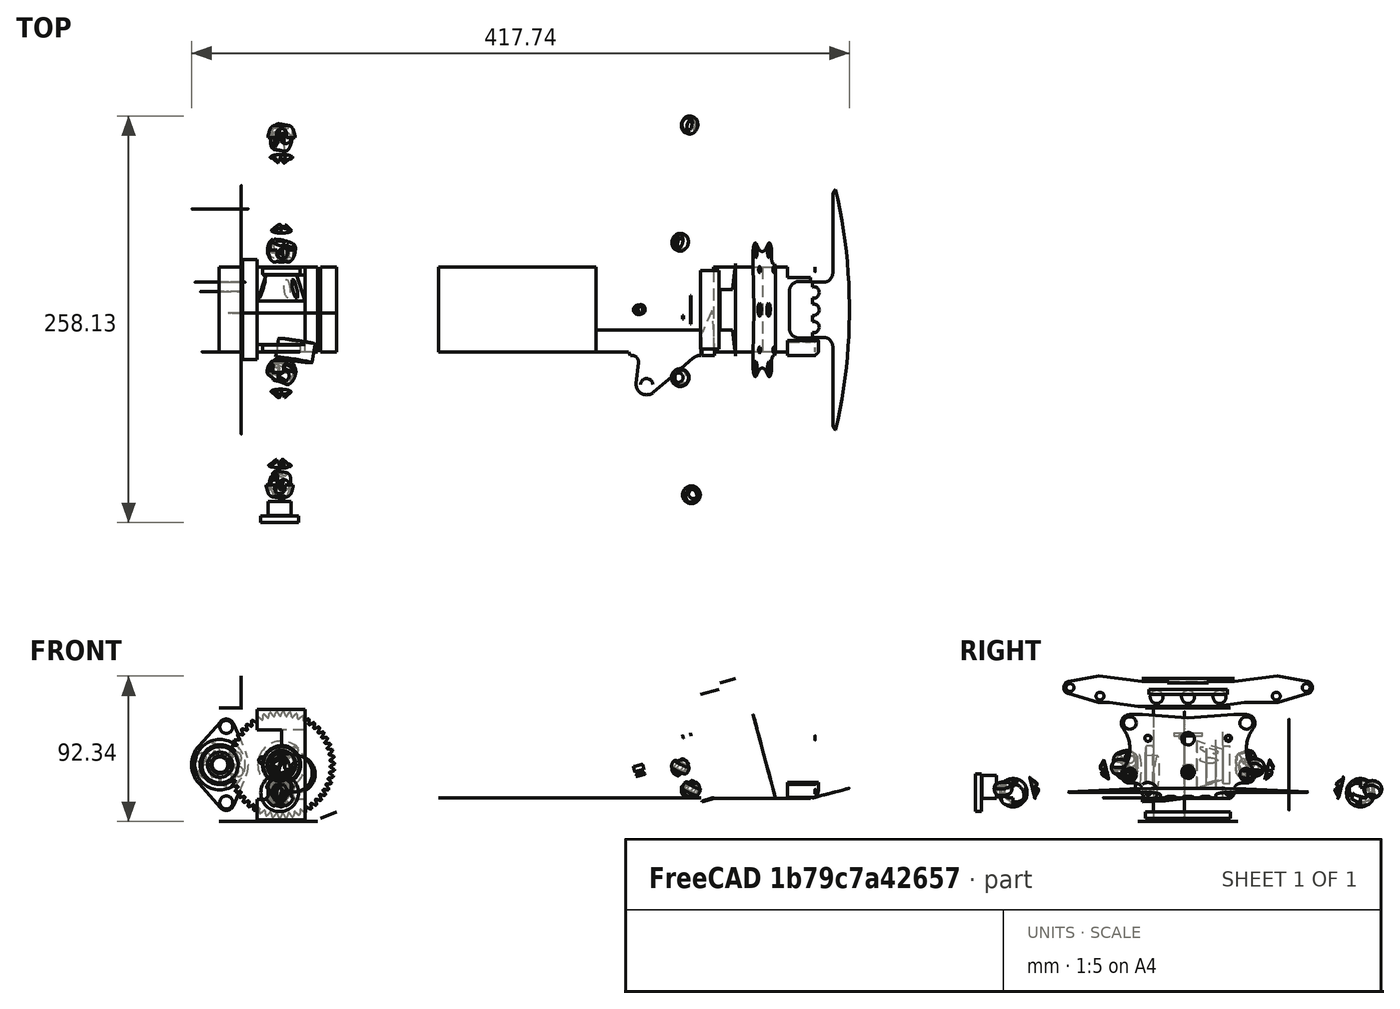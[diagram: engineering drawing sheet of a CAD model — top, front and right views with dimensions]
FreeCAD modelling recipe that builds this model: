
FCSTD DOCUMENT  (FreeCAD 2023.131R26244 +5365 (Git))
Label: Tarmo5
License: All rights reserved
LicenseURL: http://en.wikipedia.org/wiki/All_rights_reserved
objects: App::FeaturePython×327, Part::FeaturePython×279, App::Link×79, App::LinkElement×17, App::DocumentObjectGroupPython×15
note: 277 computed .brp shape members not serialized (recipe doc carries the construction recipe); baked Part::Feature solids carry a one-line shape summary decoded from their .brp
EXTERNAL_REF file=Tarmo5_parts/B03.fcstd obj=Solid
EXTERNAL_REF file=Tarmo5_parts/Part 1.fcstd obj=Solid
EXTERNAL_REF file=Tarmo5_parts/B08-T.fcstd obj=Solid
EXTERNAL_REF file=Tarmo5_parts/DRIVE ASSEMBLY _1_.fcstd obj=Link001
EXTERNAL_REF file=Tarmo5_parts/NOSE ASSEMBLY _1_.fcstd obj=Link
EXTERNAL_REF file=Tarmo5_parts/NOSE ASSEMBLY _1_.fcstd obj=Link002
EXTERNAL_REF file=Tarmo5_parts/NOSE ASSEMBLY _1_.fcstd obj=Link005
EXTERNAL_REF file=Tarmo5_parts/DRIVE ASSEMBLY _1_.fcstd obj=Link002
EXTERNAL_REF file=Tarmo5_parts/NOSE ASSEMBLY _1_.fcstd obj=Link015
EXTERNAL_REF file=Tarmo5_parts/DRIVE ASSEMBLY _1_.fcstd obj=Link009
EXTERNAL_REF file=Tarmo5_parts/DRIVE ASSEMBLY _1_.fcstd obj=Link024
EXTERNAL_REF file=Tarmo5_parts/DRIVE ASSEMBLY _1_.fcstd obj=Link027
EXTERNAL_REF file=Tarmo5_parts/NOSE ASSEMBLY _1__parts/Front Sus _1_.fcstd obj=Link001
EXTERNAL_REF file=Tarmo5_parts/NOSE ASSEMBLY _1__parts/Front Sus _1_.fcstd obj=Link005
EXTERNAL_REF file=Tarmo5_parts/DRIVE ASSEMBLY _1_.fcstd obj=Link
EXTERNAL_REF file=Tarmo5_parts/NOSE ASSEMBLY _1_.fcstd obj=Link008
EXTERNAL_REF file=Tarmo5_parts/DRIVE ASSEMBLY _1_.fcstd obj=Link004
EXTERNAL_REF file=Tarmo5_parts/DRIVE ASSEMBLY _1_.fcstd obj=Link012
EXTERNAL_REF file=Tarmo5_parts/DRIVE ASSEMBLY _1_.fcstd obj=Link029
EXTERNAL_REF file=Tarmo5_parts/DRIVE ASSEMBLY _1_.fcstd obj=Link011
EXTERNAL_REF file=Tarmo5_parts/DRIVE ASSEMBLY _1_.fcstd obj=Link019
EXTERNAL_REF file=Tarmo5_parts/DRIVE ASSEMBLY _1_.fcstd obj=Link005
EXTERNAL_REF file=Tarmo5_parts/DRIVE ASSEMBLY _1_.fcstd obj=Link007
EXTERNAL_REF file=Tarmo5_parts/DRIVE ASSEMBLY _1_.fcstd obj=Link018
EXTERNAL_REF file=Tarmo5_parts/DRIVE ASSEMBLY _1_.fcstd obj=Link016
EXTERNAL_REF file=Tarmo5_parts/DRIVE ASSEMBLY _1_.fcstd obj=Link014
EXTERNAL_REF file=Tarmo5_parts/NOSE ASSEMBLY _1__parts/Front Sus _1_.fcstd obj=Link012
EXTERNAL_REF file=Tarmo5_parts/NOSE ASSEMBLY _1__parts/Front Sus _1_.fcstd obj=Link013
EXTERNAL_REF file=Tarmo5_parts/NOSE ASSEMBLY _1__parts/Front Sus _1_.fcstd obj=Link019
EXTERNAL_REF file=Tarmo5_parts/NOSE ASSEMBLY _1__parts/Front Sus _1_.fcstd obj=Link010
EXTERNAL_REF file=Tarmo5_parts/NOSE ASSEMBLY _1__parts/Front Sus _1_.fcstd obj=Link004
EXTERNAL_REF file=Tarmo5_parts/NOSE ASSEMBLY _1__parts/Front Sus _1_.fcstd obj=Link003
EXTERNAL_REF file=Tarmo5_parts/DRIVE ASSEMBLY _1_.fcstd obj=Link015
EXTERNAL_REF file=Tarmo5_parts/NOSE ASSEMBLY _1__parts/Front Sus _1_.fcstd obj=Link015
EXTERNAL_REF file=Tarmo5_parts/NOSE ASSEMBLY _1__parts/Front Sus _1_.fcstd obj=Link008
EXTERNAL_REF file=Tarmo5_parts/NOSE ASSEMBLY _1_.fcstd obj=Link006
EXTERNAL_REF file=Tarmo5_parts/NOSE ASSEMBLY _1_.fcstd obj=Link011
EXTERNAL_REF file=Tarmo5_parts/NOSE ASSEMBLY _1__parts/Link Assembly _1_.fcstd obj=Link
EXTERNAL_REF file=Tarmo5_parts/NOSE ASSEMBLY _1__parts/Link Assembly _1_.fcstd obj=Link001
EXTERNAL_REF file=Tarmo5_parts/NOSE ASSEMBLY _1__parts/Link Assembly _1_.fcstd obj=Link002
EXTERNAL_REF file=Tarmo5_parts/NOSE ASSEMBLY _1__parts/Link Assembly _2_.fcstd obj=Link
EXTERNAL_REF file=Tarmo5_parts/NOSE ASSEMBLY _1__parts/Link Assembly _2_.fcstd obj=Link001
EXTERNAL_REF file=Tarmo5_parts/NOSE ASSEMBLY _1__parts/Link Assembly _2_.fcstd obj=Link002
EXTERNAL_REF file=Tarmo5_parts/NOSE ASSEMBLY _1_.fcstd obj=Link010
EXTERNAL_REF file=Tarmo5_parts/NOSE ASSEMBLY _1_.fcstd obj=Link003
EXTERNAL_REF file=Tarmo5_parts/NOSE ASSEMBLY _1_.fcstd obj=Link013
EXTERNAL_REF file=Tarmo5_parts/NOSE ASSEMBLY _1__parts/Front Sus _1_.fcstd obj=Link017
EXTERNAL_REF file=Tarmo5_parts/NOSE ASSEMBLY _1__parts/Front Sus _1_.fcstd obj=Link014
EXTERNAL_REF file=Tarmo5_parts/NOSE ASSEMBLY _1__parts/Front Sus _1_.fcstd obj=Link002
EXTERNAL_REF file=Tarmo5_parts/NOSE ASSEMBLY _1__parts/Front Sus _1_.fcstd obj=Link
EXTERNAL_REF file=Tarmo5_parts/NOSE ASSEMBLY _1__parts/Front Sus _1_.fcstd obj=Link018
EXTERNAL_REF file=Tarmo5_parts/NOSE ASSEMBLY _1__parts/Front Sus _1_.fcstd obj=Link011
EXTERNAL_REF file=Tarmo5_parts/NOSE ASSEMBLY _1__parts/Front Sus _1_.fcstd obj=Link007
EXTERNAL_REF file=Tarmo5_parts/NOSE ASSEMBLY _1__parts/Front Sus _1_.fcstd obj=Link006
EXTERNAL_REF file=Tarmo5_parts/DRIVE ASSEMBLY _1_.fcstd obj=Link017
EXTERNAL_REF file=Tarmo5_parts/DRIVE ASSEMBLY _1_.fcstd obj=Link010
EXTERNAL_REF file=Tarmo5_parts/DRIVE ASSEMBLY _1_.fcstd obj=Link006
EXTERNAL_REF file=Tarmo5_parts/DRIVE ASSEMBLY _1_.fcstd obj=Link003
EXTERNAL_REF file=Tarmo5_parts/DRIVE ASSEMBLY _1_.fcstd obj=Link022
EXTERNAL_REF file=Tarmo5_parts/DRIVE ASSEMBLY _1_.fcstd obj=Link032
EXTERNAL_REF file=Tarmo5_parts/DRIVE ASSEMBLY _1_.fcstd obj=Link008
EXTERNAL_REF file=Tarmo5_parts/DRIVE ASSEMBLY _1__parts/DOGBONE _1_.fcstd obj=Link
EXTERNAL_REF file=Tarmo5_parts/DRIVE ASSEMBLY _1__parts/DOGBONE _1_.fcstd obj=Link001
EXTERNAL_REF file=Tarmo5_parts/DRIVE ASSEMBLY _1__parts/DOGBONE _1_.fcstd obj=Link002
EXTERNAL_REF file=Tarmo5_parts/DRIVE ASSEMBLY _1__parts/DOGBONE _1_.fcstd obj=Link003
EXTERNAL_REF file=Tarmo5_parts/DRIVE ASSEMBLY _1__parts/DOGBONE _1_.fcstd obj=Link004
EXTERNAL_REF file=Tarmo5_parts/DRIVE ASSEMBLY _1__parts/DOGBONE _1_.fcstd obj=Link005
EXTERNAL_REF file=Tarmo5_parts/DRIVE ASSEMBLY _1__parts/DOGBONE _1_.fcstd obj=Link006
EXTERNAL_REF file=Tarmo5_parts/DRIVE ASSEMBLY _1_.fcstd obj=Link023
EXTERNAL_REF file=Tarmo5_parts/DRIVE ASSEMBLY _1_.fcstd obj=Link020
EXTERNAL_REF file=Tarmo5_parts/Fasteners/M4x16Screws.FCStd obj=Link
EXTERNAL_REF file=Tarmo5_parts/NOSE ASSEMBLY _1__parts/Front Sus _1_.fcstd obj=Link009
EXTERNAL_REF file=Tarmo5_parts/Fasteners/M4x35Screws.FCStd obj=Screw
EXTERNAL_REF file=Tarmo5_parts/Fasteners/M4xScrews.FCStd obj=Screw
EXTERNAL_REF file=Tarmo5_parts/Fasteners/M4x45Screws.FCStd obj=Screw
EXTERNAL_REF file=Tarmo5_parts/Fasteners/M4x16Screws.FCStd obj=Screw
EXTERNAL_REF file=Tarmo5_parts/Fasteners/M3_Nut.FCStd obj=Nut

FEATURE [App::Link] Link  label="B03"
  AutoLinkLabel = true
  AutoPlacement = true
  LinkPlacement = pos=(-50.1198,8.13855,-13.564) rot=(0,0,1;1.5708rad)
  LinkedObject = -> <external Tarmo5_parts/B03.fcstd>#Solid
  Placement = pos=(-50.1198,8.13855,-13.564) rot=(0,0,1;1.5708rad)
  SyncGroupVisibility = false
  TreeRank = 1
  _LinkVersion = 1
FEATURE [App::Link] Link001  label="Part 1"
  AutoLinkLabel = true
  AutoPlacement = true
  LinkPlacement = pos=(103.215,30.1385,-27.0233) rot=(0,0,-1;1.5708rad)
  LinkedObject = -> <external Tarmo5_parts/Part 1.fcstd>#Solid
  Placement = pos=(103.215,30.1385,-27.0233) rot=(0,0,-1;1.5708rad)
  SyncGroupVisibility = false
  TreeRank = 641
  _LinkVersion = 1
FEATURE [App::Link] Link002  label="B08-T"
  AutoLinkLabel = true
  AutoPlacement = true
  LinkPlacement = pos=(-32.1198,-28.8615,-5.56404) rot=(-0.57735,-0.57735,-0.57735;2.0944rad)
  LinkedObject = -> <external Tarmo5_parts/B08-T.fcstd>#Solid
  Placement = pos=(-32.1198,-28.8615,-5.56404) rot=(-0.57735,-0.57735,-0.57735;2.0944rad)
  SyncGroupVisibility = false
  TreeRank = 5
  _LinkVersion = 1
FEATURE [App::Link] Link005  label="B02"
  AutoLinkLabel = false
  AutoPlacement = true
  LinkPlacement = pos=(-105.52,8.13855,-13.564) rot=(0,0,1;1.5708rad)
  LinkedObject = -> <external Tarmo5_parts/DRIVE ASSEMBLY _1_.fcstd>#Link001
  Placement = pos=(-105.52,8.13855,-13.564) rot=(0,0,1;1.5708rad)
  SyncGroupVisibility = false
  TreeRank = 17
  _LinkOwner = 2515
  _LinkVersion = 1
FEATURE [App::Link] Link006  label="B04"
  AutoLinkLabel = false
  AutoPlacement = true
  LinkPlacement = pos=(127.88,8.13855,-9.06404) rot=(0,0,1;1.5708rad)
  LinkedObject = -> <external Tarmo5_parts/NOSE ASSEMBLY _1_.fcstd>#Link
  Placement = pos=(127.88,8.13855,-9.06404) rot=(0,0,1;1.5708rad)
  SyncGroupVisibility = false
  TreeRank = 18
  _LinkOwner = 2515
  _LinkVersion = 1
FEATURE [App::Link] Link007  label="B05"
  AutoLinkLabel = false
  AutoPlacement = true
  LinkPlacement = pos=(129.622,8.13853,-9.37807) rot=(0,0,1;1.5708rad)
  LinkedObject = -> <external Tarmo5_parts/NOSE ASSEMBLY _1_.fcstd>#Link002
  Placement = pos=(129.622,8.13853,-9.37807) rot=(0,0,1;1.5708rad)
  SyncGroupVisibility = false
  TreeRank = 19
  _LinkOwner = 2515
  _LinkVersion = 1
FEATURE [App::Link] Link008  label="B06"
  AutoLinkLabel = false
  AutoPlacement = true
  LinkPlacement = pos=(125.481,8.13853,-9.37807) rot=(0,0,1;1.5708rad)
  LinkedObject = -> <external Tarmo5_parts/NOSE ASSEMBLY _1_.fcstd>#Link005
  Placement = pos=(125.481,8.13853,-9.37807) rot=(0,0,1;1.5708rad)
  SyncGroupVisibility = false
  TreeRank = 20
  _LinkOwner = 2515
  _LinkVersion = 1
FEATURE [App::Link] Link009  label="A01"
  AutoLinkLabel = false
  AutoPlacement = true
  LinkPlacement = pos=(-110.52,40.1385,31.436) rot=(0,0,1;0rad)
  LinkedObject = -> <external Tarmo5_parts/DRIVE ASSEMBLY _1_.fcstd>#Link002
  Placement = pos=(-110.52,40.1385,31.436) rot=(0,0,1;0rad)
  SyncGroupVisibility = false
  TreeRank = 21
  _LinkOwner = 2515
  _LinkVersion = 1
FEATURE [App::Link] Link010  label="A002"
  AutoLinkLabel = false
  AutoPlacement = true
  LinkPlacement = pos=(195.547,-23.8615,32.0753) rot=(-0.130526,0,0.991445;3.14159rad)
  LinkedObject = -> <external Tarmo5_parts/NOSE ASSEMBLY _1_.fcstd>#Link015
  Placement = pos=(195.547,-23.8615,32.0753) rot=(-0.130526,0,0.991445;3.14159rad)
  SyncGroupVisibility = false
  TreeRank = 22
  _LinkOwner = 2515
  _LinkVersion = 1
FEATURE [App::Link] Link011  label="B13-T"
  AutoLinkLabel = false
  AutoPlacement = true
  LinkPlacement = pos=(-105.52,8.13855,-13.564) rot=(0,0,-1;1.5708rad)
  LinkedObject = -> <external Tarmo5_parts/DRIVE ASSEMBLY _1_.fcstd>#Link009
  Placement = pos=(-105.52,8.13855,-13.564) rot=(0,0,-1;1.5708rad)
  SyncGroupVisibility = false
  TreeRank = 23
  _LinkOwner = 2515
  _LinkVersion = 1
FEATURE [App::Link] Link012  label="B12-T"
  AutoLinkLabel = false
  AutoPlacement = true
  LinkPlacement = pos=(-65.1198,8.13855,-13.564) rot=(0,0,-1;1.5708rad)
  LinkedObject = -> <external Tarmo5_parts/DRIVE ASSEMBLY _1_.fcstd>#Link024
  Placement = pos=(-65.1198,8.13855,-13.564) rot=(0,0,-1;1.5708rad)
  SyncGroupVisibility = false
  TreeRank = 24
  _LinkOwner = 2515
  _LinkVersion = 1
FEATURE [App::Link] Link013  label="B01"
  AutoLinkLabel = false
  AutoPlacement = true
  LinkPlacement = pos=(-105.52,8.13855,-13.564) rot=(0,0,1;3.14159rad)
  LinkedObject = -> <external Tarmo5_parts/DRIVE ASSEMBLY _1_.fcstd>#Link027
  Placement = pos=(-105.52,8.13855,-13.564) rot=(0,0,1;3.14159rad)
  SyncGroupVisibility = false
  TreeRank = 25
  _LinkOwner = 2515
  _LinkVersion = 1
FEATURE [App::Link] Link014  label="B11-T"
  AutoLinkLabel = false
  AutoPlacement = true
  LinkPlacement = pos=(181.617,8.13853,-38.0407) rot=(0,1,0;6.02139rad)
  LinkedObject = -> <external Tarmo5_parts/NOSE ASSEMBLY _1__parts/Front Sus _1_.fcstd>#Link001
  Placement = pos=(181.617,8.13853,-38.0407) rot=(0,1,0;6.02139rad)
  SyncGroupVisibility = false
  TreeRank = 26
  _LinkOwner = 2515
  _LinkVersion = 1
FEATURE [App::Link] Link015  label="B10-T"
  AutoLinkLabel = false
  AutoPlacement = true
  LinkPlacement = pos=(220.627,8.13853,-38.3547) rot=(0,1,0;6.02139rad)
  LinkedObject = -> <external Tarmo5_parts/NOSE ASSEMBLY _1__parts/Front Sus _1_.fcstd>#Link005
  Placement = pos=(220.627,8.13853,-38.3547) rot=(0,1,0;6.02139rad)
  SyncGroupVisibility = false
  TreeRank = 27
  _LinkOwner = 2515
  _LinkVersion = 1
FEATURE [App::Link] Link016  label="B09"
  AutoLinkLabel = false
  AutoPlacement = true
  LinkPlacement = pos=(-129.02,72.1385,-13.564) rot=(0,0.707107,0.707107;3.14159rad)
  LinkedObject = -> <external Tarmo5_parts/DRIVE ASSEMBLY _1_.fcstd>#Link
  Placement = pos=(-129.02,72.1385,-13.564) rot=(0,0.707107,0.707107;3.14159rad)
  SyncGroupVisibility = false
  TreeRank = 28
  _LinkOwner = 2515
  _LinkVersion = 1
FEATURE [App::Link] Link017  label="B07-T"
  AutoLinkLabel = false
  AutoPlacement = true
  LinkPlacement = pos=(244.221,8.13853,-35.5564) rot=(-0.129428,0.129428,0.983106;4.69535rad)
  LinkedObject = -> <external Tarmo5_parts/NOSE ASSEMBLY _1_.fcstd>#Link008
  Placement = pos=(244.221,8.13853,-35.5564) rot=(-0.129428,0.129428,0.983106;4.69535rad)
  SyncGroupVisibility = false
  TreeRank = 29
  _LinkOwner = 2515
  _LinkVersion = 1
FEATURE [App::Link] Link019  label="Part 003"
  AutoLinkLabel = false
  AutoPlacement = true
  LinkPlacement = pos=(-101.02,33.6385,3.43596) rot=(-0.57735,-0.57735,-0.57735;4.18879rad)
  LinkedObject = -> <external Tarmo5_parts/DRIVE ASSEMBLY _1_.fcstd>#Link012
  Placement = pos=(-101.02,33.6385,3.43596) rot=(-0.57735,-0.57735,-0.57735;4.18879rad)
  SyncGroupVisibility = false
  TreeRank = 31
  _LinkOwner = 2515
  _LinkVersion = 1
FEATURE [App::Link] Link020  label="Part 004"
  AutoLinkLabel = false
  AutoPlacement = true
  LinkPlacement = pos=(-129.02,-13.6115,-13.564) rot=(0,1,0;3.14159rad)
  LinkedObject = -> <external Tarmo5_parts/DRIVE ASSEMBLY _1_.fcstd>#Link029
  Placement = pos=(-129.02,-13.6115,-13.564) rot=(0,1,0;3.14159rad)
  SyncGroupVisibility = false
  TreeRank = 32
  _LinkOwner = 2515
  _LinkVersion = 1
FEATURE [App::Link] Link021  label="Part 005"
  AutoLinkLabel = false
  AutoPlacement = true
  LinkPlacement = pos=(-90.0198,-18.8615,-13.564) rot=(0,0,1;3.14159rad)
  LinkedObject = -> <external Tarmo5_parts/DRIVE ASSEMBLY _1_.fcstd>#Link011
  Placement = pos=(-90.0198,-18.8615,-13.564) rot=(0,0,1;3.14159rad)
  SyncGroupVisibility = false
  TreeRank = 33
  _LinkOwner = 2515
  _LinkVersion = 1
FEATURE [App::Link] Link022  label="Part 006"
  AutoLinkLabel = false
  AutoPlacement = true
  LinkPlacement = pos=(-90.0198,35.1385,-13.564) rot=(0,0,1;0rad)
  LinkedObject = -> <external Tarmo5_parts/DRIVE ASSEMBLY _1_.fcstd>#Link019
  Placement = pos=(-90.0198,35.1385,-13.564) rot=(0,0,1;0rad)
  SyncGroupVisibility = false
  TreeRank = 34
  _LinkOwner = 2515
  _LinkVersion = 1
FEATURE [App::Link] Link026  label="A02"
  AutoLinkLabel = false
  AutoPlacement = true
  LinkPlacement = pos=(-105.52,-67.8076,-39.4513) rot=(-0.116949,0.116949,-0.986228;4.69852rad)
  LinkedObject = -> <external Tarmo5_parts/DRIVE ASSEMBLY _1_.fcstd>#Link005
  Placement = pos=(-105.52,-67.8076,-39.4513) rot=(-0.116949,0.116949,-0.986228;4.69852rad)
  SyncGroupVisibility = false
  TreeRank = 102
  _LinkOwner = 2604
  _LinkVersion = 1
FEATURE [App::Link] Link027  label="A003"
  AutoLinkLabel = false
  AutoPlacement = true
  LinkPlacement = pos=(-75.5198,84.0847,-5.45132) rot=(-0.116949,-0.116949,-0.986228;1.58466rad)
  LinkedObject = -> <external Tarmo5_parts/DRIVE ASSEMBLY _1_.fcstd>#Link007
  Placement = pos=(-75.5198,84.0847,-5.45132) rot=(-0.116949,-0.116949,-0.986228;1.58466rad)
  SyncGroupVisibility = false
  TreeRank = 113
  _LinkOwner = 2604
  _LinkVersion = 1
FEATURE [App::Link] Link028  label="A004"
  AutoLinkLabel = false
  AutoPlacement = true
  LinkPlacement = pos=(-105.52,84.0847,-39.4513) rot=(0.704634,-0.704634,0.083557;2.97487rad)
  LinkedObject = -> <external Tarmo5_parts/DRIVE ASSEMBLY _1_.fcstd>#Link018
  Placement = pos=(-105.52,84.0847,-39.4513) rot=(0.704634,-0.704634,0.083557;2.97487rad)
  SyncGroupVisibility = false
  TreeRank = 114
  _LinkOwner = 2604
  _LinkVersion = 1
FEATURE [App::Link] Link029  label="A03"
  AutoLinkLabel = false
  AutoPlacement = true
  LinkPlacement = pos=(-89.9198,137.031,-31.3386) rot=(0,0,-1;3.14159rad)
  LinkedObject = -> <external Tarmo5_parts/DRIVE ASSEMBLY _1_.fcstd>#Link016
  Placement = pos=(-89.9198,137.031,-31.3386) rot=(0,0,-1;3.14159rad)
  SyncGroupVisibility = false
  TreeRank = 117
  _LinkVersion = 1
FEATURE [App::Link] Link030  label="A005"
  AutoLinkLabel = false
  AutoPlacement = true
  LinkPlacement = pos=(-75.5198,-67.8076,-5.45132) rot=(-0.704634,-0.704634,-0.083557;2.97487rad)
  LinkedObject = -> <external Tarmo5_parts/DRIVE ASSEMBLY _1_.fcstd>#Link014
  Placement = pos=(-75.5198,-67.8076,-5.45132) rot=(-0.704634,-0.704634,-0.083557;2.97487rad)
  SyncGroupVisibility = false
  TreeRank = 116
  _LinkOwner = 2604
  _LinkVersion = 1
FEATURE [App::Link] Link031  label="A006"
  AutoLinkLabel = false
  AutoPlacement = true
  LinkPlacement = pos=(214.469,82.3563,-29.2816) rot=(-0.028523,0.22455,0.974045;4.65926rad)
  LinkedObject = -> <external Tarmo5_parts/NOSE ASSEMBLY _1__parts/Front Sus _1_.fcstd>#Link012
  Placement = pos=(214.469,82.3563,-29.2816) rot=(-0.028523,0.22455,0.974045;4.65926rad)
  SyncGroupVisibility = false
  TreeRank = 118
  _LinkOwner = 2604
  _LinkVersion = 1
FEATURE [App::Link] Link032  label="A007"
  AutoLinkLabel = false
  AutoPlacement = true
  LinkPlacement = pos=(176.691,82.3563,-4.20474) rot=(0.688224,-0.706955,0.162977;3.18299rad)
  LinkedObject = -> <external Tarmo5_parts/NOSE ASSEMBLY _1__parts/Front Sus _1_.fcstd>#Link013
  Placement = pos=(176.691,82.3563,-4.20474) rot=(0.688224,-0.706955,0.162977;3.18299rad)
  SyncGroupVisibility = false
  TreeRank = 119
  _LinkOwner = 2604
  _LinkVersion = 1
FEATURE [App::Link] Link033  label="A008"
  AutoLinkLabel = false
  AutoPlacement = true
  LinkPlacement = pos=(214.469,-66.0793,-29.2816) rot=(-0.688224,-0.706955,-0.162977;3.18299rad)
  LinkedObject = -> <external Tarmo5_parts/NOSE ASSEMBLY _1__parts/Front Sus _1_.fcstd>#Link019
  Placement = pos=(214.469,-66.0793,-29.2816) rot=(-0.688224,-0.706955,-0.162977;3.18299rad)
  SyncGroupVisibility = false
  TreeRank = 120
  _LinkOwner = 2604
  _LinkVersion = 1
FEATURE [App::Link] Link034  label="A009"
  AutoLinkLabel = false
  AutoPlacement = true
  LinkPlacement = pos=(176.691,-66.0793,-4.20474) rot=(0.028523,0.22455,-0.974045;4.65926rad)
  LinkedObject = -> <external Tarmo5_parts/NOSE ASSEMBLY _1__parts/Front Sus _1_.fcstd>#Link010
  Placement = pos=(176.691,-66.0793,-4.20474) rot=(0.028523,0.22455,-0.974045;4.65926rad)
  SyncGroupVisibility = false
  TreeRank = 121
  _LinkOwner = 2604
  _LinkVersion = 1
FEATURE [App::Link] Link035  label="A04"
  AutoLinkLabel = false
  AutoPlacement = true
  LinkPlacement = pos=(196.986,114.574,-24.3075) rot=(0.129428,-0.129428,-0.983106;1.58783rad)
  LinkedObject = -> <external Tarmo5_parts/NOSE ASSEMBLY _1__parts/Front Sus _1_.fcstd>#Link004
  Placement = pos=(196.986,114.574,-24.3075) rot=(0.129428,-0.129428,-0.983106;1.58783rad)
  SyncGroupVisibility = false
  TreeRank = 171
  _LinkOwner = 2604
  _LinkVersion = 1
FEATURE [App::Link] Link036  label="A010"
  AutoLinkLabel = false
  AutoPlacement = true
  LinkPlacement = pos=(198.145,-98.2971,-23.997) rot=(-0.129428,-0.129428,0.983106;1.58783rad)
  LinkedObject = -> <external Tarmo5_parts/NOSE ASSEMBLY _1__parts/Front Sus _1_.fcstd>#Link003
  Placement = pos=(198.145,-98.2971,-23.997) rot=(-0.129428,-0.129428,0.983106;1.58783rad)
  SyncGroupVisibility = false
  TreeRank = 172
  _LinkOwner = 2604
  _LinkVersion = 1
FEATURE [App::Link] Link037  label="A011"
  AutoLinkLabel = false
  AutoPlacement = true
  LinkPlacement = pos=(-91.1198,-120.754,-31.3386) rot=(0,0,1;0rad)
  LinkedObject = -> <external Tarmo5_parts/DRIVE ASSEMBLY _1_.fcstd>#Link015
  Placement = pos=(-91.1198,-120.754,-31.3386) rot=(0,0,1;0rad)
  SyncGroupVisibility = false
  TreeRank = 194
  _LinkOwner = 2604
  _LinkVersion = 1
FEATURE [App::Link] Link038  label="A06"
  AutoLinkLabel = false
  AutoPlacement = true
  LinkPlacement = pos=(197.199,153.573,-24.0435) rot=(-0.130526,-0.000714,0.991445;3.13074rad)
  LinkedObject = -> <external Tarmo5_parts/NOSE ASSEMBLY _1__parts/Front Sus _1_.fcstd>#Link015
  Placement = pos=(197.199,153.573,-24.0435) rot=(-0.130526,-0.000714,0.991445;3.13074rad)
  SyncGroupVisibility = false
  TreeRank = 217
  _LinkOwner = 2604
  _LinkVersion = 1
FEATURE [App::Link] Link039  label="A05"
  AutoLinkLabel = false
  AutoPlacement = true
  LinkPlacement = pos=(198.312,-125.295,-23.7451) rot=(0.130526,-0.001139,-0.991444;3.12429rad)
  LinkedObject = -> <external Tarmo5_parts/NOSE ASSEMBLY _1__parts/Front Sus _1_.fcstd>#Link008
  Placement = pos=(198.312,-125.295,-23.7451) rot=(0.130526,-0.001139,-0.991444;3.12429rad)
  SyncGroupVisibility = false
  TreeRank = 218
  _LinkOwner = 2604
  _LinkVersion = 1
FEATURE [App::Link] Link040  label="A08"
  AutoLinkLabel = false
  AutoPlacement = true
  LinkPlacement = pos=(143.307,55.6385,-39.5909) rot=(-0.763566,-0.637858,-0.100525;3.30915rad)
  LinkedObject = -> <external Tarmo5_parts/NOSE ASSEMBLY _1_.fcstd>#Link006
  Placement = pos=(143.307,55.6385,-39.5909) rot=(-0.763566,-0.637858,-0.100525;3.30915rad)
  SyncGroupVisibility = false
  TreeRank = 229
  _LinkOwner = 2604
  _LinkVersion = 1
FEATURE [App::Link] Link041  label="A07"
  AutoLinkLabel = false
  AutoPlacement = true
  LinkPlacement = pos=(136.707,-39.3615,-14.9598) rot=(0.128989,-0.153039,-0.979766;1.42083rad)
  LinkedObject = -> <external Tarmo5_parts/NOSE ASSEMBLY _1_.fcstd>#Link011
  Placement = pos=(136.707,-39.3615,-14.9598) rot=(0.128989,-0.153039,-0.979766;1.42083rad)
  SyncGroupVisibility = false
  TreeRank = 230
  _LinkOwner = 2604
  _LinkVersion = 1
FEATURE [App::Link] Link042  label="A10B"
  AutoLinkLabel = false
  AutoPlacement = true
  LinkPlacement = pos=(165.392,-102.99,-26.1097) rot=(-0.872256,0.482265,-0.081178;2.90119rad)
  LinkedObject = -> <external Tarmo5_parts/NOSE ASSEMBLY _1__parts/Link Assembly _1_.fcstd>#Link
  Placement = pos=(165.392,-102.99,-26.1097) rot=(-0.872256,0.482265,-0.081178;2.90119rad)
  SyncGroupVisibility = false
  TreeRank = 243
  _LinkOwner = 2604
  _LinkVersion = 1
FEATURE [App::Link] Link043  label="A10C"
  AutoLinkLabel = false
  AutoPlacement = true
  LinkPlacement = pos=(239.877,-64.8807,2.27137) rot=(-0.130489,-0.024029,0.991159;2.78053rad)
  LinkedObject = -> <external Tarmo5_parts/NOSE ASSEMBLY _1__parts/Link Assembly _1_.fcstd>#Link001
  Placement = pos=(239.877,-64.8807,2.27137) rot=(-0.130489,-0.024029,0.991159;2.78053rad)
  SyncGroupVisibility = false
  TreeRank = 244
  _LinkOwner = 2604
  _LinkVersion = 1
FEATURE [App::Link] Link044  label="A10A"
  AutoLinkLabel = false
  AutoPlacement = true
  LinkPlacement = pos=(169.83,-116.855,-32.9007) rot=(0.272191,0.12914,0.953538;1.75269rad)
  LinkedObject = -> <external Tarmo5_parts/NOSE ASSEMBLY _1__parts/Link Assembly _1_.fcstd>#Link002
  Placement = pos=(169.83,-116.855,-32.9007) rot=(0.272191,0.12914,0.953538;1.75269rad)
  SyncGroupVisibility = false
  TreeRank = 245
  _LinkOwner = 2604
  _LinkVersion = 1
FEATURE [App::Link] Link045  label="A10B001"
  AutoLinkLabel = false
  AutoPlacement = true
  LinkPlacement = pos=(169.064,117.99,-24.9878) rot=(0.672816,0.73881,0.038452;2.86114rad)
  LinkedObject = -> <external Tarmo5_parts/NOSE ASSEMBLY _1__parts/Link Assembly _2_.fcstd>#Link
  Placement = pos=(169.064,117.99,-24.9878) rot=(0.672816,0.73881,0.038452;2.86114rad)
  SyncGroupVisibility = false
  TreeRank = 266
  _LinkOwner = 2604
  _LinkVersion = 1
FEATURE [App::Link] Link046  label="A10A001"
  AutoLinkLabel = false
  AutoPlacement = true
  LinkPlacement = pos=(172.12,132.781,-32.4739) rot=(-0.288488,0.473392,0.832271;4.53461rad)
  LinkedObject = -> <external Tarmo5_parts/NOSE ASSEMBLY _1__parts/Link Assembly _2_.fcstd>#Link001
  Placement = pos=(172.12,132.781,-32.4739) rot=(-0.288488,0.473392,0.832271;4.53461rad)
  SyncGroupVisibility = false
  TreeRank = 267
  _LinkOwner = 2604
  _LinkVersion = 1
FEATURE [App::Link] Link047  label="A10C001"
  AutoLinkLabel = false
  AutoPlacement = true
  LinkPlacement = pos=(232.844,6.5176,0.386769) rot=(-0.130435,-0.037382,0.990752;2.58826rad)
  LinkedObject = -> <external Tarmo5_parts/NOSE ASSEMBLY _1__parts/Link Assembly _2_.fcstd>#Link002
  Placement = pos=(232.844,6.5176,0.386769) rot=(-0.130435,-0.037382,0.990752;2.58826rad)
  SyncGroupVisibility = false
  TreeRank = 268
  _LinkOwner = 2604
  _LinkVersion = 1
FEATURE [App::Link] Link048  label="A09"
  AutoLinkLabel = false
  AutoPlacement = true
  LinkPlacement = pos=(115.686,8.22588,-13.3971) rot=(-0.704063,0.704063,-0.092692;2.95674rad)
  LinkedObject = -> <external Tarmo5_parts/NOSE ASSEMBLY _1_.fcstd>#Link010
  Placement = pos=(115.686,8.22588,-13.3971) rot=(-0.704063,0.704063,-0.092692;2.95674rad)
  SyncGroupVisibility = false
  TreeRank = 289
  _LinkOwner = 2604
  _LinkVersion = 1
FEATURE [App::Link] Link049  label="Servo"
  AutoLinkLabel = false
  AutoPlacement = true
  LinkPlacement = pos=(136.466,8.13884,24.575) rot=(-0.991445,-6e-06,-0.130526;3.14159rad)
  LinkedObject = -> <external Tarmo5_parts/NOSE ASSEMBLY _1_.fcstd>#Link003
  Placement = pos=(136.466,8.13884,24.575) rot=(-0.991445,-6e-06,-0.130526;3.14159rad)
  SyncGroupVisibility = false
  TreeRank = 300
  _LinkOwner = 2604
  _LinkVersion = 1
FEATURE [App::Link] Link050  label="Servo Horn"
  AutoLinkLabel = false
  AutoPlacement = true
  LinkPlacement = pos=(137.108,8.39062,-16.4571) rot=(0.706946,-0.701117,0.093071;3.32568rad)
  LinkedObject = -> <external Tarmo5_parts/NOSE ASSEMBLY _1_.fcstd>#Link013
  Placement = pos=(137.108,8.39062,-16.4571) rot=(0.706946,-0.701117,0.093071;3.32568rad)
  SyncGroupVisibility = false
  TreeRank = 301
  _LinkOwner = 2604
  _LinkVersion = 1
FEATURE [App::Link] Link051  label="Part 007"
  AutoLinkLabel = false
  AutoPlacement = true
  LinkPlacement = pos=(198.338,-126.789,-23.7383) rot=(-0.008707,-0.997773,0.066137;0.262377rad)
  LinkedObject = -> <external Tarmo5_parts/NOSE ASSEMBLY _1__parts/Front Sus _1_.fcstd>#Link017
  Placement = pos=(198.338,-126.789,-23.7383) rot=(-0.008707,-0.997773,0.066137;0.262377rad)
  SyncGroupVisibility = false
  TreeRank = 329
  _LinkOwner = 2604
  _LinkVersion = 1
FEATURE [App::Link] Link052  label="C10"
  AutoLinkLabel = false
  AutoPlacement = true
  LinkPlacement = pos=(198.422,-131.788,-23.7157) rot=(0.982995,-0.120975,0.138151;1.58565rad)
  LinkedObject = -> <external Tarmo5_parts/NOSE ASSEMBLY _1__parts/Front Sus _1_.fcstd>#Link014
  Placement = pos=(198.422,-131.788,-23.7157) rot=(0.982995,-0.120975,0.138151;1.58565rad)
  SyncGroupVisibility = false
  TreeRank = 330
  _LinkOwner = 2604
  _LinkVersion = 1
FEATURE [App::Link] Link053  label="Part 008"
  AutoLinkLabel = false
  AutoPlacement = true
  LinkPlacement = pos=(198.287,-123.797,-23.7518) rot=(-0.991408,-0.008652,-0.130521;3.14387rad)
  LinkedObject = -> <external Tarmo5_parts/NOSE ASSEMBLY _1__parts/Front Sus _1_.fcstd>#Link002
  Placement = pos=(198.287,-123.797,-23.7518) rot=(-0.991408,-0.008652,-0.130521;3.14387rad)
  SyncGroupVisibility = false
  TreeRank = 331
  _LinkOwner = 2604
  _LinkVersion = 1
FEATURE [App::Link] Link054  label="C09"
  AutoLinkLabel = false
  AutoPlacement = true
  LinkPlacement = pos=(197.984,-105.8,-23.8331) rot=(0.982995,-0.120975,0.138151;1.58565rad)
  LinkedObject = -> <external Tarmo5_parts/NOSE ASSEMBLY _1__parts/Front Sus _1_.fcstd>#Link
  Placement = pos=(197.984,-105.8,-23.8331) rot=(0.982995,-0.120975,0.138151;1.58565rad)
  SyncGroupVisibility = false
  TreeRank = 332
  _LinkOwner = 2604
  _LinkVersion = 1
FEATURE [App::Link] Link055  label="Part 009"
  AutoLinkLabel = false
  AutoPlacement = true
  LinkPlacement = pos=(197.056,140.075,-24.0818) rot=(0.005468,-0.999122,-0.041536;0.262023rad)
  LinkedObject = -> <external Tarmo5_parts/NOSE ASSEMBLY _1__parts/Front Sus _1_.fcstd>#Link018
  Placement = pos=(197.056,140.075,-24.0818) rot=(0.005468,-0.999122,-0.041536;0.262023rad)
  SyncGroupVisibility = false
  TreeRank = 353
  _LinkOwner = 2604
  _LinkVersion = 1
FEATURE [App::Link] Link056  label="C011"
  AutoLinkLabel = false
  AutoPlacement = true
  LinkPlacement = pos=(196.866,122.076,-24.1328) rot=(-0.983054,-0.124129,-0.134897;1.58645rad)
  LinkedObject = -> <external Tarmo5_parts/NOSE ASSEMBLY _1__parts/Front Sus _1_.fcstd>#Link011
  Placement = pos=(196.866,122.076,-24.1328) rot=(-0.983054,-0.124129,-0.134897;1.58645rad)
  SyncGroupVisibility = false
  TreeRank = 354
  _LinkOwner = 2604
  _LinkVersion = 1
FEATURE [App::Link] Link057  label="C012"
  AutoLinkLabel = false
  AutoPlacement = true
  LinkPlacement = pos=(197.172,151.067,-24.0506) rot=(0.983101,-0.134709,0.123956;1.58928rad)
  LinkedObject = -> <external Tarmo5_parts/NOSE ASSEMBLY _1__parts/Front Sus _1_.fcstd>#Link007
  Placement = pos=(197.172,151.067,-24.0506) rot=(0.983101,-0.134709,0.123956;1.58928rad)
  SyncGroupVisibility = false
  TreeRank = 355
  _LinkOwner = 2604
  _LinkVersion = 1
FEATURE [App::Link] Link058  label="Part 010"
  AutoLinkLabel = false
  AutoPlacement = true
  LinkPlacement = pos=(197.087,143.068,-24.0733) rot=(0.991431,-0.005426,0.130522;3.14302rad)
  LinkedObject = -> <external Tarmo5_parts/NOSE ASSEMBLY _1__parts/Front Sus _1_.fcstd>#Link006
  Placement = pos=(197.087,143.068,-24.0733) rot=(0.991431,-0.005426,0.130522;3.14302rad)
  SyncGroupVisibility = false
  TreeRank = 356
  _LinkOwner = 2604
  _LinkVersion = 1
FEATURE [App::Link] Link059  label="C08"
  AutoLinkLabel = false
  AutoPlacement = true
  LinkPlacement = pos=(-129.02,7.63855,-13.564) rot=(0,1,0;3.24631rad)
  LinkedObject = -> <external Tarmo5_parts/DRIVE ASSEMBLY _1_.fcstd>#Link017
  Placement = pos=(-129.02,7.63855,-13.564) rot=(0,1,0;3.24631rad)
  SyncGroupVisibility = false
  TreeRank = 407
  _LinkOwner = 2604
  _LinkVersion = 1
FEATURE [App::Link] Link060  label="C07"
  AutoLinkLabel = false
  AutoPlacement = true
  LinkPlacement = pos=(-90.0198,5.93855,-13.564) rot=(0,-1,0;1.3439rad)
  LinkedObject = -> <external Tarmo5_parts/DRIVE ASSEMBLY _1_.fcstd>#Link010
  Placement = pos=(-90.0198,5.93855,-13.564) rot=(0,-1,0;1.3439rad)
  SyncGroupVisibility = false
  TreeRank = 408
  _LinkOwner = 2604
  _LinkVersion = 1
FEATURE [App::Link] Link061  label="C06"
  AutoLinkLabel = false
  AutoPlacement = true
  LinkPlacement = pos=(-90.0198,30.1385,-13.564) rot=(0.664391,-0.528481,0.528481;1.96874rad)
  LinkedObject = -> <external Tarmo5_parts/DRIVE ASSEMBLY _1_.fcstd>#Link006
  Placement = pos=(-90.0198,30.1385,-13.564) rot=(0.664391,-0.528481,0.528481;1.96874rad)
  SyncGroupVisibility = false
  TreeRank = 409
  _LinkOwner = 2604
  _LinkVersion = 1
FEATURE [App::Link] Link062  label="D3542 OUTRUNNER"
  AutoLinkLabel = false
  AutoPlacement = true
  LinkPlacement = pos=(-129.02,64.1385,-13.564) rot=(0.211541,-0.211541,-0.954201;1.61766rad)
  LinkedObject = -> <external Tarmo5_parts/DRIVE ASSEMBLY _1_.fcstd>#Link003
  Placement = pos=(-129.02,64.1385,-13.564) rot=(0.211541,-0.211541,-0.954201;1.61766rad)
  SyncGroupVisibility = false
  TreeRank = 410
  _LinkOwner = 2604
  _LinkVersion = 1
FEATURE [App::Link] Link065  label="Part 011"
  AutoLinkLabel = false
  AutoPlacement = true
  LinkPlacement = pos=(-91.1198,-119.006,-31.3386) rot=(-1,0,0;3.14159rad)
  LinkedObject = -> <external Tarmo5_parts/DRIVE ASSEMBLY _1_.fcstd>#Link022
  Placement = pos=(-91.1198,-119.006,-31.3386) rot=(-1,0,0;3.14159rad)
  SyncGroupVisibility = false
  TreeRank = 458
  _LinkOwner = 2604
  _LinkVersion = 1
FEATURE [App::Link] Link066  label="Part 012"
  AutoLinkLabel = false
  AutoPlacement = true
  LinkPlacement = pos=(-91.1198,-127.502,-31.3386) rot=(1,0,0;3.14159rad)
  LinkedObject = -> <external Tarmo5_parts/DRIVE ASSEMBLY _1_.fcstd>#Link032
  Placement = pos=(-91.1198,-127.502,-31.3386) rot=(1,0,0;3.14159rad)
  SyncGroupVisibility = false
  TreeRank = 459
  _LinkOwner = 2604
  _LinkVersion = 1
FEATURE [App::Link] Link067  label="C013"
  AutoLinkLabel = false
  AutoPlacement = true
  ElementCount = 2
  LinkPlacement = pos=(-91.1198,-131.308,-27.5677) rot=(1,0,0;4.71239rad)
  LinkedObject = -> <external Tarmo5_parts/DRIVE ASSEMBLY _1_.fcstd>#Link008
  Placement = pos=(-91.1198,-131.308,-27.5677) rot=(1,0,0;4.71239rad)
  PlacementList = 2 placements: [(6.23402e-10,3.7709,0.806459),(1.2,3.7709,275.087)]
  ScaleList = (2) [(1,1,1),(1,1,1)]
  ShowElement = false
  SyncGroupVisibility = false
  TreeRank = 465
  _LinkOwner = 2604
  _LinkVersion = 1
FEATURE [App::Link] Link068  label="C03"
  AutoLinkLabel = false
  AutoPlacement = true
  ElementCount = 2
  LinkPlacement = pos=(-90.0198,-31.6115,-13.564) rot=(0.08311,0.784722,-0.614251;3.61941rad)
  LinkedObject = -> <external Tarmo5_parts/DRIVE ASSEMBLY _1__parts/DOGBONE _1_.fcstd>#Link
  Placement = pos=(-90.0198,-31.6115,-13.564) rot=(0.08311,0.784722,-0.614251;3.61941rad)
  PlacementList = 2 placements: [(1.63425e-13,2.27374e-13,3.2685e-13),(31.5345,21.3507,-67.7848)]
  ScaleList = (2) [(1,1,1),(1,1,1)]
  ShowElement = false
  SyncGroupVisibility = false
  TreeRank = 487
  _LinkOwner = 2604
  _LinkVersion = 1
FEATURE [App::Link] Link069  label="C01"
  AutoLinkLabel = false
  AutoPlacement = true
  ElementCount = 2
  LinkPlacement = pos=(-78.9832,-182.181,-30.0249) rot=(-0.535007,-0.652659,0.536473;4.2015rad)
  LinkedObject = -> <external Tarmo5_parts/DRIVE ASSEMBLY _1__parts/DOGBONE _1_.fcstd>#Link001
  Placement = pos=(-78.9832,-182.181,-30.0249) rot=(-0.535007,-0.652659,0.536473;4.2015rad)
  PlacementList = 2 placements: [(6.28741,-0.124123,-81.8466),(-3.75052,21.6598,-230.123)]
  ScaleList = (2) [(1,1,1),(1,1,1)]
  ShowElement = false
  SyncGroupVisibility = false
  TreeRank = 488
  _LinkOwner = 2604
  _LinkVersion = 1
FEATURE [App::Link] Link070  label="C02"
  AutoLinkLabel = false
  AutoPlacement = true
  ElementCount = 2
  LinkPlacement = pos=(-71.0198,-78.6115,-13.564) rot=(0.57735,0.57735,0.57735;4.18879rad)
  LinkedObject = -> <external Tarmo5_parts/DRIVE ASSEMBLY _1__parts/DOGBONE _1_.fcstd>#Link002
  Placement = pos=(-71.0198,-78.6115,-13.564) rot=(0.57735,0.57735,0.57735;4.18879rad)
  PlacementList = 2 placements: [(-1.85986e-06,-19,45),(-17.7746,-18.9,194.144)]
  ScaleList = (2) [(1,1,1),(1,1,1)]
  ShowElement = false
  SyncGroupVisibility = false
  TreeRank = 489
  _LinkOwner = 2604
  _LinkVersion = 1
FEATURE [App::Link] Link071  label="C04"
  AutoLinkLabel = false
  AutoPlacement = true
  ElementCount = 2
  LinkPlacement = pos=(-35.6542,-70.9422,-31.2599) rot=(0.174827,0.03262,0.984059;1.61771rad)
  LinkedObject = -> <external Tarmo5_parts/DRIVE ASSEMBLY _1__parts/DOGBONE _1_.fcstd>#Link003
  Placement = pos=(-35.6542,-70.9422,-31.2599) rot=(0.174827,0.03262,0.984059;1.61771rad)
  PlacementList = 2 placements: [(9.89894,55.2841,-3.25512),(157.091,47.5022,-26.1414)]
  ScaleList = (2) [(1,1,1),(1,1,1)]
  ShowElement = false
  SyncGroupVisibility = false
  TreeRank = 490
  _LinkOwner = 2604
  _LinkVersion = 1
FEATURE [App::Link] Link072  label="C014"
  AutoLinkLabel = false
  AutoPlacement = true
  ElementCount = 2
  LinkPlacement = pos=(-89.0665,-94.904,-23.0056) rot=(0.71216,-0.69051,-0.126585;3.09426rad)
  LinkedObject = -> <external Tarmo5_parts/DRIVE ASSEMBLY _1__parts/DOGBONE _1_.fcstd>#Link004
  Placement = pos=(-89.0665,-94.904,-23.0056) rot=(0.71216,-0.69051,-0.126585;3.09426rad)
  PlacementList = 2 placements: [(-23.2067,0.356799,4.09623),(-170.988,-6.6925,23.0211)]
  ScaleList = (2) [(1,1,1),(1,1,1)]
  ShowElement = false
  SyncGroupVisibility = false
  TreeRank = 491
  _LinkOwner = 2604
  _LinkVersion = 1
FEATURE [App::Link] Link073  label="C05-T"
  AutoLinkLabel = false
  AutoPlacement = true
  ElementCount = 2
  LinkPlacement = pos=(-53.3169,-66.7774,-26.774) rot=(0.686881,-0.546101,0.47955;2.08315rad)
  LinkedObject = -> <external Tarmo5_parts/DRIVE ASSEMBLY _1__parts/DOGBONE _1_.fcstd>#Link005
  Placement = pos=(-53.3169,-66.7774,-26.774) rot=(0.686881,-0.546101,0.47955;2.08315rad)
  PlacementList = 2 placements: [(-3.69226,37.3216,-0.502317),(-24.5243,29.9171,-148.014)]
  ScaleList = (2) [(1,1,1),(1,1,1)]
  ShowElement = false
  SyncGroupVisibility = false
  TreeRank = 492
  _LinkOwner = 2604
  _LinkVersion = 1
FEATURE [App::Link] Link074  label="C015"
  AutoLinkLabel = false
  AutoPlacement = true
  ElementCount = 2
  LinkPlacement = pos=(-63.5869,-118.494,-34.4712) rot=(0.573172,0.471159,-0.670435;4.4733rad)
  LinkedObject = -> <external Tarmo5_parts/DRIVE ASSEMBLY _1__parts/DOGBONE _1_.fcstd>#Link006
  Placement = pos=(-63.5869,-118.494,-34.4712) rot=(0.573172,0.471159,-0.670435;4.4733rad)
  PlacementList = 2 placements: [(10.5396,6.35403,29.2626),(228.055,14.2978,64.7921)]
  ScaleList = (2) [(1,1,1),(1,1,1)]
  ShowElement = false
  SyncGroupVisibility = false
  TreeRank = 493
  _LinkOwner = 2604
  _LinkVersion = 1
FEATURE [App::Link] Link075  label="Part 013"
  AutoLinkLabel = false
  AutoPlacement = true
  LinkPlacement = pos=(-89.9198,143.779,-31.3386) rot=(0,0,1;0rad)
  LinkedObject = -> <external Tarmo5_parts/DRIVE ASSEMBLY _1_.fcstd>#Link023
  Placement = pos=(-89.9198,143.779,-31.3386) rot=(0,0,1;0rad)
  SyncGroupVisibility = false
  TreeRank = 543
  _LinkOwner = 2604
  _LinkVersion = 1
FEATURE [App::Link] Link076  label="Part 014"
  AutoLinkLabel = false
  AutoPlacement = true
  LinkPlacement = pos=(-89.9198,130.283,-31.3386) rot=(1,0,0;3.14159rad)
  LinkedObject = -> <external Tarmo5_parts/DRIVE ASSEMBLY _1_.fcstd>#Link020
  Placement = pos=(-89.9198,130.283,-31.3386) rot=(1,0,0;3.14159rad)
  SyncGroupVisibility = false
  TreeRank = 544
  _LinkOwner = 2604
  _LinkVersion = 1
FEATURE [App::LinkElement] Link078_i0
  LinkPlacement = pos=(-1.8135,46.0887,40.5345) rot=(-0.229004,-0.968754,-0.095249;0.538514rad)
  LinkedObject = -> <external Tarmo5_parts/Fasteners/M4x16Screws.FCStd>#Link
  Placement = pos=(-1.8135,46.0887,40.5345) rot=(-0.229004,-0.968754,-0.095249;0.538514rad)
  TreeRank = 613
  _LinkOwner = 3179
  _LinkVersion = 1
FEATURE [App::LinkElement] Link078_i1
  LinkPlacement = pos=(12.6572,119.041,22.0713) rot=(-0.150043,-0.814814,0.55997;0.635415rad)
  LinkedObject = -> <external Tarmo5_parts/Fasteners/M4x16Screws.FCStd>#Link
  Placement = pos=(12.6572,119.041,22.0713) rot=(-0.150043,-0.814814,0.55997;0.635415rad)
  TreeRank = 614
  _LinkOwner = 3179
  _LinkVersion = 1
FEATURE [App::LinkElement] Link078_i2
  LinkPlacement = pos=(-0.898395,277.98,41.2918) rot=(0.232064,-0.969116,0.083426;0.538761rad)
  LinkedObject = -> <external Tarmo5_parts/Fasteners/M4x16Screws.FCStd>#Link
  Placement = pos=(-0.898395,277.98,41.2918) rot=(0.232064,-0.969116,0.083426;0.538761rad)
  TreeRank = 615
  _LinkOwner = 3179
  _LinkVersion = 1
FEATURE [App::LinkElement] Link078_i3
  LinkPlacement = pos=(12.6915,205.011,22.0912) rot=(-0.192085,-0.670224,0.71687;0.760651rad)
  LinkedObject = -> <external Tarmo5_parts/Fasteners/M4x16Screws.FCStd>#Link
  Placement = pos=(12.6915,205.011,22.0912) rot=(-0.192085,-0.670224,0.71687;0.760651rad)
  TreeRank = 616
  _LinkOwner = 3179
  _LinkVersion = 1
FEATURE [App::Link] Link078  label="M4x16-Screw"
  AutoLinkLabel = false
  AutoPlacement = true
  ElementCount = 4
  ElementList = -> [Link078_i0,Link078_i1,Link078_i2,Link078_i3]
  LinkPlacement = pos=(182,-154,-2.20537e-06) rot=(0,1,0;3.40339rad)
  LinkedObject = -> <external Tarmo5_parts/Fasteners/M4x16Screws.FCStd>#Link
  Placement = pos=(182,-154,-2.20537e-06) rot=(0,1,0;3.40339rad)
  SyncGroupVisibility = false
  TreeRank = 612
  _LinkOwner = 2604
  _LinkVersion = 1
FEATURE [App::LinkElement] Link079_i0
  LinkPlacement = pos=(-47.1788,-14.9409,58.1246) rot=(2e-06,-1,-1.1e-05;0.276038rad)
  LinkedObject = -> <external Tarmo5_parts/NOSE ASSEMBLY _1__parts/Front Sus _1_.fcstd>#Link009
  Placement = pos=(-47.1788,-14.9409,58.1246) rot=(2e-06,-1,-1.1e-05;0.276038rad)
  TreeRank = 642
  _LinkOwner = 3207
  _LinkVersion = 1
FEATURE [App::LinkElement] Link079_i1
  LinkPlacement = pos=(-319.054,52.3243,-7.09025) rot=(0.093271,-0.708462,-0.699559;0.372036rad)
  LinkedObject = -> <external Tarmo5_parts/NOSE ASSEMBLY _1__parts/Front Sus _1_.fcstd>#Link009
  Placement = pos=(-319.054,52.3243,-7.09025) rot=(0.093271,-0.708462,-0.699559;0.372036rad)
  TreeRank = 643
  _LinkOwner = 3207
  _LinkVersion = 1
FEATURE [App::LinkElement] Link079_i2
  LinkPlacement = pos=(-133.46,-14.9409,381.686) rot=(0,-1,0;3.38923rad)
  LinkedObject = -> <external Tarmo5_parts/NOSE ASSEMBLY _1__parts/Front Sus _1_.fcstd>#Link009
  Placement = pos=(-133.46,-14.9409,381.686) rot=(0,-1,0;3.38923rad)
  TreeRank = 644
  _LinkOwner = 3207
  _LinkVersion = 1
FEATURE [App::LinkElement] Link079_i3
  LinkPlacement = pos=(-404.479,52.6349,303.15) rot=(-0.130506,-0.991295,-0.0174;3.4044rad)
  LinkedObject = -> <external Tarmo5_parts/NOSE ASSEMBLY _1__parts/Front Sus _1_.fcstd>#Link009
  Placement = pos=(-404.479,52.6349,303.15) rot=(-0.130506,-0.991295,-0.0174;3.4044rad)
  TreeRank = 645
  _LinkOwner = 3207
  _LinkVersion = 1
FEATURE [App::Link] Link079  label="Wheel 110mm"
  AutoLinkLabel = false
  AutoPlacement = true
  ElementCount = 4
  ElementList = -> [Link079_i0,Link079_i1,Link079_i2,Link079_i3]
  LinkPlacement = pos=(222.834,244.028,-1.70666) rot=(0.965497,0.001647,0.260409;1.5708rad)
  LinkedObject = -> <external Tarmo5_parts/NOSE ASSEMBLY _1__parts/Front Sus _1_.fcstd>#Link009
  Placement = pos=(222.834,244.028,-1.70666) rot=(0.965497,0.001647,0.260409;1.5708rad)
  SyncGroupVisibility = false
  TreeRank = 640
  _LinkOwner = 2604
  _LinkVersion = 1
FEATURE [App::Link] Link080  label="Link080(M4x35-Screw)"
  AutoLinkLabel = true
  AutoPlacement = true
  ElementCount = 5
  LinkPlacement = pos=(246.532,19.1385,-28.7256) rot=(0.704063,0.704063,0.092692;2.95674rad)
  LinkedObject = -> <external Tarmo5_parts/Fasteners/M4x35Screws.FCStd>#Screw
  Placement = pos=(246.532,19.1385,-28.7256) rot=(0.704063,0.704063,0.092692;2.95674rad)
  PlacementList = 5 placements: [(-5.68434e-14,2.84217e-14,5.68434e-14),(-11,0,7.10543e-14),(-22,-2.84217e-14,7.10543e-14),(-16.5,-7.5,7.10543e-14),(-5.5,-7.5,5.68434e-14)]
  ScaleList = (5) [(1,1,1),(1,1,1),(1,1,1),(1,1,1),(1,1,1)]
  ShowElement = false
  SyncGroupVisibility = false
  TreeRank = 666
  _LinkVersion = 1
FEATURE [App::Link] Link081  label="Link081(M4x45-Screw)"
  AutoLinkLabel = true
  AutoPlacement = true
  ElementCount = 4
  LinkPlacement = pos=(205.229,-28.8615,11.383) rot=(0.519988,0.519988,0.677661;1.95044rad)
  LinkedObject = -> <external Tarmo5_parts/Fasteners/M4xScrews.FCStd>#Screw
  Placement = pos=(205.229,-28.8615,11.383) rot=(0.519988,0.519988,0.677661;1.95044rad)
  PlacementList = 4 placements: [(0,0,0),(74,-34,0),(74,-1.37052e-06,2.84217e-14),(7.10543e-15,-34,-2.84217e-14)]
  ScaleList = (4) [(1,1,1),(1,1,1),(1,1,1),(1,1,1)]
  ShowElement = false
  SyncGroupVisibility = false
  TreeRank = 689
  _LinkVersion = 1
FEATURE [App::LinkElement] Link082_i0
  LinkPlacement = pos=(8.53e-14,78,2.8137e-12) rot=(0,0,1;0rad)
  LinkedObject = -> <external Tarmo5_parts/Fasteners/M4x45Screws.FCStd>#Screw
  Placement = pos=(8.53e-14,78,2.8137e-12) rot=(0,0,1;0rad)
  TreeRank = 729
  _LinkOwner = 3291
  _LinkVersion = 1
FEATURE [App::LinkElement] Link082_i1
  LinkPlacement = pos=(-34,78,2.8137e-12) rot=(0,0,1;0rad)
  LinkedObject = -> <external Tarmo5_parts/Fasteners/M4x45Screws.FCStd>#Screw
  Placement = pos=(-34,78,2.8137e-12) rot=(0,0,1;0rad)
  TreeRank = 730
  _LinkOwner = 3291
  _LinkVersion = 1
FEATURE [App::LinkElement] Link082_i2
  LinkPlacement = pos=(7.1e-15,7.1e-15,1.42e-14) rot=(0,0,1;0rad)
  LinkedObject = -> <external Tarmo5_parts/Fasteners/M4x45Screws.FCStd>#Screw
  Placement = pos=(7.1e-15,7.1e-15,1.42e-14) rot=(0,0,1;0rad)
  TreeRank = 731
  _LinkOwner = 3291
  _LinkVersion = 1
FEATURE [App::LinkElement] Link082_i3
  LinkPlacement = pos=(-34,3.55e-14,1.42e-14) rot=(0,0,1;0rad)
  LinkedObject = -> <external Tarmo5_parts/Fasteners/M4x45Screws.FCStd>#Screw
  Placement = pos=(-34,3.55e-14,1.42e-14) rot=(0,0,1;0rad)
  TreeRank = 732
  _LinkOwner = 3291
  _LinkVersion = 1
FEATURE [App::Link] Link082  label="Link082(M4x50-Screw)"
  AutoLinkLabel = true
  AutoPlacement = true
  ElementCount = 4
  ElementList = -> [Link082_i0,Link082_i1,Link082_i2,Link082_i3]
  LinkPlacement = pos=(-110.52,-30.8615,3.43596) rot=(0,-1,0;1.5708rad)
  LinkedObject = -> <external Tarmo5_parts/Fasteners/M4x45Screws.FCStd>#Screw
  Placement = pos=(-110.52,-30.8615,3.43596) rot=(0,-1,0;1.5708rad)
  SyncGroupVisibility = false
  TreeRank = 720
  _LinkVersion = 1
FEATURE [App::Link] Link083  label="Link083(M4x16-Screw)"
  AutoLinkLabel = true
  AutoPlacement = true
  ElementCount = 3
  LinkPlacement = pos=(-111.52,-11.8615,29.436) rot=(0,-1,0;1.5708rad)
  LinkedObject = -> <external Tarmo5_parts/Fasteners/M4x16Screws.FCStd>#Screw
  Placement = pos=(-111.52,-11.8615,29.436) rot=(0,-1,0;1.5708rad)
  PlacementList = 3 placements: [(-1.24345e-13,-1.77636e-14,-1.93268e-12),(-9.23706e-14,20,-1.1795e-12),(-1.42109e-14,40,-4.9738e-13)]
  ScaleList = (3) [(1,1,1),(1,1,1),(1,1,1)]
  ShowElement = false
  SyncGroupVisibility = false
  TreeRank = 738
  _LinkVersion = 1
FEATURE [App::Link] Link084  label="Link084(M4x16-Screw)"
  AutoLinkLabel = true
  AutoPlacement = true
  ElementCount = 3
  LinkPlacement = pos=(197.03,-11.8615,30.4023) rot=(0.608761,0,0.793353;3.14159rad)
  LinkedObject = -> <external Tarmo5_parts/Fasteners/M4x16Screws.FCStd>#Screw
  Placement = pos=(197.03,-11.8615,30.4023) rot=(0.608761,0,0.793353;3.14159rad)
  PlacementList = 3 placements: [(-2.84217e-14,-40,-2.84217e-14),(-1.1724e-13,-20,2.84217e-14),(-2.84217e-14,1.77636e-15,-2.84217e-14)]
  ScaleList = (3) [(1,1,1),(1,1,1),(1,1,1)]
  ShowElement = false
  SyncGroupVisibility = false
  TreeRank = 747
  _LinkVersion = 1
FEATURE [App::LinkElement] Link018_i0
  LinkedObject = -> <external Tarmo5_parts/DRIVE ASSEMBLY _1_.fcstd>#Link004
  TreeRank = 758
  _LinkOwner = 2529
  _LinkVersion = 1
FEATURE [App::LinkElement] Link018_i1
  LinkPlacement = pos=(51,-0.25,0) rot=(0,0,1;0rad)
  LinkedObject = -> <external Tarmo5_parts/DRIVE ASSEMBLY _1_.fcstd>#Link004
  Placement = pos=(51,-0.25,0) rot=(0,0,1;0rad)
  TreeRank = 759
  _LinkOwner = 2529
  _LinkVersion = 1
FEATURE [App::Link] Link018  label="Part 002"
  AutoLinkLabel = false
  AutoPlacement = true
  ElementCount = 2
  ElementList = -> [Link018_i0,Link018_i1]
  LinkPlacement = pos=(-101.02,-17.3615,-30.564) rot=(0.57735,0.57735,0.57735;2.0944rad)
  LinkedObject = -> <external Tarmo5_parts/DRIVE ASSEMBLY _1_.fcstd>#Link004
  Placement = pos=(-101.02,-17.3615,-30.564) rot=(0.57735,0.57735,0.57735;2.0944rad)
  SyncGroupVisibility = false
  TreeRank = 30
  _LinkOwner = 2515
  _LinkVersion = 1
FEATURE [Part::FeaturePython] Parts  # WARN: FeaturePython — macro-defined, semantics opaque (R4)
  Group = -> [Link,Link002,Link005,Link006,Link007,Link008,Link009,Link010,Link011,Link012,Link013,Link014,Link015,Link016,Link017,Link018,Link019,Link020,Link021,Link022]
  GroupMode = 0
  InvalidShape = false
  TreeRank = 16
  ValidateShape = true
  _LinkVersion = 1
FEATURE [App::LinkElement] Link085_i0
  LinkedObject = -> <external Tarmo5_parts/Fasteners/M3_Nut.FCStd>#Nut
  TreeRank = 770
  _LinkOwner = 3338
  _LinkVersion = 1
FEATURE [App::LinkElement] Link085_i1
  LinkPlacement = pos=(34,51,-1.42e-14) rot=(0,1,0;3.14159rad)
  LinkedObject = -> <external Tarmo5_parts/Fasteners/M3_Nut.FCStd>#Nut
  Placement = pos=(34,51,-1.42e-14) rot=(0,1,0;3.14159rad)
  TreeRank = 771
  _LinkOwner = 3338
  _LinkVersion = 1
FEATURE [App::LinkElement] Link085_i2
  LinkPlacement = pos=(0,51,-1.42e-14) rot=(0,0,1;0rad)
  LinkedObject = -> <external Tarmo5_parts/Fasteners/M3_Nut.FCStd>#Nut
  Placement = pos=(0,51,-1.42e-14) rot=(0,0,1;0rad)
  TreeRank = 772
  _LinkOwner = 3338
  _LinkVersion = 1
FEATURE [App::Link] Link085  label="Link085(M3-Nut)"
  AutoLinkLabel = true
  AutoPlacement = true
  ElementCount = 3
  ElementList = -> [Link085_i0,Link085_i1,Link085_i2]
  LinkPlacement = pos=(-86.0198,-17.3615,-30.564) rot=(0,-1,0;1.5708rad)
  LinkedObject = -> <external Tarmo5_parts/Fasteners/M3_Nut.FCStd>#Nut
  Placement = pos=(-86.0198,-17.3615,-30.564) rot=(0,-1,0;1.5708rad)
  SyncGroupVisibility = false
  TreeRank = 760
  _LinkVersion = 1
FEATURE [App::Link] Link086  label="Link086(Chassis)"
  AutoLinkLabel = true
  AutoPlacement = true
  LinkedObject = -> Assembly
  SyncGroupVisibility = false
  TreeRank = 802
  _LinkVersion = 1
FEATURE [Part::FeaturePython] Assembly  label="Chassis"  # WARN: FeaturePython — macro-defined, semantics opaque (R4)
  AutoRelax = true
  BuildShape = 1
  Freeze = false
  Group = -> [Constraints,Elements,Parts]
  InvalidShape = false
  TreeRank = 13
  ValidateShape = true
  Verbose = false
  _LinkVersion = 1
  _SolverType = 1
  _Version = 1
FEATURE [App::FeaturePython] Constraints  # WARN: FeaturePython — macro-defined, semantics opaque (R4)
  Group = -> [Constraint,Constraint001,Constraint002,Constraint003,Constraint004,Constraint005,Constraint006,Constraint007,Constraint008,Constraint009,Constraint010,Constraint011,Constraint060,Constraint061]
  TreeRank = 14
  _LinkVersion = 1
  _Version = 1
FEATURE [App::FeaturePython] Elements  # WARN: FeaturePython — macro-defined, semantics opaque (R4)
  Group = -> [_Element,_Element001,_Element002,_Element003,_Element004,_Element005,_Element006,_Element007,_Element008,_Element009,_Element010,_Element011,_Element012,_Element013,_Element014,_Element015,_Element016,_Element017,_Element018,_Element019,_Element020,Element,Element001,Element002,Element003,Element004,Element005,Element006,Element007,Element008,Element009,Element010,Element011,Element012,Element013,+36 more]
  TreeRank = 15
  _LinkVersion = 1
FEATURE [App::FeaturePython] Constraint  label="Locked"  # WARN: FeaturePython — macro-defined, semantics opaque (R4)
  Disabled = false
  Group = -> [ElementLink]
  TreeRank = 38
  _ConstraintType = 0
  _LinkVersion = 1
  _Parent = -> Constraints
FEATURE [App::FeaturePython] ElementLink  label="_Element"  # link proxy (typed FeaturePython)
  LinkTransform = true
  LinkedObject = -> _Element
  TreeRank = 39
  _LinkVersion = 1
  _Parent = -> Constraint
FEATURE [Part::FeaturePython] _Element  # link proxy (typed FeaturePython)
  Detach = false
  InvalidShape = false
  LinkTransform = true
  LinkedObject = -> Link [Face17]
  TreeRank = 40
  ValidateShape = true
  _LinkVersion = 1
  _Parent = -> Elements
FEATURE [App::FeaturePython] Constraint001  label="AttachmentOffset"  # WARN: FeaturePython — macro-defined, semantics opaque (R4)
  Cascade = false
  Disabled = false
  Group = -> [ElementLink001,ElementLink002]
  Multiply = false
  TreeRank = 41
  _ConstraintType = 0
  _LinkVersion = 1
  _Parent = -> Constraints
FEATURE [App::FeaturePython] ElementLink001  label="_Element"  # link proxy (typed FeaturePython)
  LinkTransform = true
  LinkedObject = -> _Element
  TreeRank = 42
  _LinkVersion = 1
  _Parent = -> Constraint001
FEATURE [App::FeaturePython] ElementLink002  label="_Element001"  # link proxy (typed FeaturePython)
  LinkTransform = true
  LinkedObject = -> _Element001
  Offset = pos=(-33.5,83.3327,-1.42e-14) rot=(0,0,1;0rad)
  Placement = pos=(-83.3327,33.5,3.34e-13) rot=(0,0,1;0rad)
  TreeRank = 43
  _LinkVersion = 1
  _OffsetAdded = true
  _Parent = -> Constraint001
FEATURE [Part::FeaturePython] _Element001  # link proxy (typed FeaturePython)
  Detach = false
  InvalidShape = false
  LinkTransform = true
  LinkedObject = -> Link006 [Face4]
  TreeRank = 44
  ValidateShape = true
  _LinkVersion = 1
  _Parent = -> Elements
FEATURE [App::FeaturePython] Constraint002  label="AttachmentOffset001"  # WARN: FeaturePython — macro-defined, semantics opaque (R4)
  Cascade = false
  Disabled = false
  Group = -> [ElementLink003,ElementLink004]
  Multiply = false
  TreeRank = 45
  _ConstraintType = 0
  _LinkVersion = 1
  _Parent = -> Constraints
FEATURE [App::FeaturePython] ElementLink003  label="_Element002"  # link proxy (typed FeaturePython)
  LinkTransform = true
  LinkedObject = -> _Element002
  TreeRank = 46
  _LinkVersion = 1
  _Parent = -> Constraint002
FEATURE [Part::FeaturePython] _Element002  # link proxy (typed FeaturePython)
  Detach = false
  InvalidShape = false
  LinkTransform = true
  LinkedObject = -> Link [Face63]
  TreeRank = 47
  ValidateShape = true
  _LinkVersion = 1
  _Parent = -> Elements
FEATURE [App::FeaturePython] ElementLink004  label="_Element003"  # link proxy (typed FeaturePython)
  LinkTransform = true
  LinkedObject = -> _Element003
  Offset = pos=(-1.78e-14,11,-4) rot=(-0.185814,-0.185814,-0.964856;1.60657rad)
  Placement = pos=(-70.971,79.2584,3.4776) rot=(-0.185814,-0.185814,0.964856;1.60657rad)
  TreeRank = 48
  _LinkVersion = 1
  _OffsetAdded = true
  _Parent = -> Constraint002
FEATURE [Part::FeaturePython] _Element003  # link proxy (typed FeaturePython)
  Detach = false
  InvalidShape = false
  LinkTransform = true
  LinkedObject = -> Link012 [Face12]
  TreeRank = 49
  ValidateShape = true
  _LinkVersion = 1
  _Parent = -> Elements
FEATURE [App::FeaturePython] Constraint003  label="AttachmentOffset002"  # WARN: FeaturePython — macro-defined, semantics opaque (R4)
  Cascade = false
  Disabled = false
  Group = -> [ElementLink005,ElementLink006]
  Multiply = false
  TreeRank = 50
  _ConstraintType = 0
  _LinkVersion = 1
  _Parent = -> Constraints
FEATURE [App::FeaturePython] ElementLink005  label="_Element002"  # link proxy (typed FeaturePython)
  LinkTransform = true
  LinkedObject = -> _Element002
  TreeRank = 51
  _LinkVersion = 1
  _Parent = -> Constraint003
FEATURE [App::FeaturePython] ElementLink006  label="_Element004"  # link proxy (typed FeaturePython)
  LinkTransform = true
  LinkedObject = -> _Element004
  Offset = pos=(-4.796e-13,-30.2,-4) rot=(0.185814,-0.185814,0.964856;1.60657rad)
  Placement = pos=(-86.0839,-82.1813,-2.56756) rot=(0.185814,-0.185814,-0.964856;1.60657rad)
  TreeRank = 52
  _LinkVersion = 1
  _OffsetAdded = true
  _Parent = -> Constraint003
FEATURE [Part::FeaturePython] _Element004  # link proxy (typed FeaturePython)
  Detach = false
  InvalidShape = false
  LinkTransform = true
  LinkedObject = -> Link005 [Face17]
  TreeRank = 53
  ValidateShape = true
  _LinkVersion = 1
  _Parent = -> Elements
FEATURE [App::FeaturePython] Constraint004  label="AttachmentOffset003"  # WARN: FeaturePython — macro-defined, semantics opaque (R4)
  Cascade = false
  Disabled = false
  Group = -> [ElementLink007,ElementLink008]
  Multiply = false
  TreeRank = 54
  _ConstraintType = 0
  _LinkVersion = 1
  _Parent = -> Constraints
FEATURE [App::FeaturePython] ElementLink007  label="_Element002"  # link proxy (typed FeaturePython)
  LinkTransform = true
  LinkedObject = -> _Element002
  TreeRank = 55
  _LinkVersion = 1
  _Parent = -> Constraint004
FEATURE [App::FeaturePython] ElementLink008  label="_Element005"  # link proxy (typed FeaturePython)
  LinkTransform = true
  LinkedObject = -> _Element005
  Offset = pos=(4.814e-13,49.9,-4) rot=(-0.185814,-0.185814,-0.964856;1.60657rad)
  Placement = pos=(-70.971,118.158,3.4776) rot=(-0.185814,-0.185814,0.964856;1.60657rad)
  TreeRank = 56
  _LinkVersion = 1
  _OffsetAdded = true
  _Parent = -> Constraint004
FEATURE [Part::FeaturePython] _Element005  # link proxy (typed FeaturePython)
  Detach = false
  InvalidShape = false
  LinkTransform = true
  LinkedObject = -> Link011 [Face14]
  TreeRank = 57
  ValidateShape = true
  _LinkVersion = 1
  _Parent = -> Elements
FEATURE [App::FeaturePython] Constraint005  label="AttachmentOffset004"  # WARN: FeaturePython — macro-defined, semantics opaque (R4)
  Cascade = false
  Disabled = false
  Group = -> [ElementLink009,ElementLink010]
  Multiply = false
  TreeRank = 58
  _ConstraintType = 0
  _LinkVersion = 1
  _Parent = -> Constraints
FEATURE [App::FeaturePython] ElementLink009  label="_Element002"  # link proxy (typed FeaturePython)
  LinkTransform = true
  LinkedObject = -> _Element002
  TreeRank = 59
  _LinkVersion = 1
  _Parent = -> Constraint005
FEATURE [App::FeaturePython] ElementLink010  label="_Element006"  # link proxy (typed FeaturePython)
  LinkTransform = true
  LinkedObject = -> _Element006
  Offset = pos=(61.9,-4.885e-13,-4) rot=(0.189108,0,0.981956;3.14159rad)
  Placement = pos=(-191.82,16.2771,-44.862) rot=(-0.189108,0,0.981956;3.14159rad)
  TreeRank = 60
  _LinkVersion = 1
  _OffsetAdded = true
  _Parent = -> Constraint005
FEATURE [Part::FeaturePython] _Element006  # link proxy (typed FeaturePython)
  Detach = false
  InvalidShape = false
  LinkTransform = true
  LinkedObject = -> Link013 [Face2]
  TreeRank = 61
  ValidateShape = true
  _LinkVersion = 1
  _Parent = -> Elements
FEATURE [App::FeaturePython] Constraint006  label="AttachmentOffset005"  # WARN: FeaturePython — macro-defined, semantics opaque (R4)
  Cascade = false
  Disabled = false
  Group = -> [ElementLink011,ElementLink012]
  Multiply = false
  TreeRank = 62
  _ConstraintType = 0
  _LinkVersion = 1
  _Parent = -> Constraints
FEATURE [App::FeaturePython] ElementLink011  label="_Element002"  # link proxy (typed FeaturePython)
  LinkTransform = true
  LinkedObject = -> _Element002
  TreeRank = 63
  _LinkVersion = 1
  _Parent = -> Constraint006
FEATURE [App::FeaturePython] ElementLink012  label="_Element007"  # link proxy (typed FeaturePython)
  LinkTransform = true
  LinkedObject = -> _Element007
  Offset = pos=(-68.9,-32,-64) rot=(0.964856,-0.185814,-0.185814;1.60657rad)
  Placement = pos=(32.8805,21.7026,69.3317) rot=(-0.964856,-0.185814,-0.185814;1.60657rad)
  TreeRank = 64
  _LinkVersion = 1
  _OffsetAdded = true
  _Parent = -> Constraint006
FEATURE [Part::FeaturePython] _Element007  # link proxy (typed FeaturePython)
  Detach = false
  InvalidShape = false
  LinkTransform = true
  LinkedObject = -> Link016 [Face14]
  TreeRank = 65
  ValidateShape = true
  _LinkVersion = 1
  _Parent = -> Elements
FEATURE [App::FeaturePython] Constraint007  label="AttachmentOffset006"  # WARN: FeaturePython — macro-defined, semantics opaque (R4)
  Cascade = false
  Disabled = false
  Group = -> [ElementLink013,ElementLink014]
  Multiply = false
  TreeRank = 66
  _ConstraintType = 0
  _LinkVersion = 1
  _Parent = -> Constraints
FEATURE [App::FeaturePython] ElementLink013  label="_Element008"  # link proxy (typed FeaturePython)
  LinkTransform = true
  LinkedObject = -> _Element008
  TreeRank = 67
  _LinkVersion = 1
  _Parent = -> Constraint007
FEATURE [Part::FeaturePython] _Element008  # link proxy (typed FeaturePython)
  Detach = false
  InvalidShape = false
  LinkTransform = true
  LinkedObject = -> Link009 [Face3]
  TreeRank = 68
  ValidateShape = true
  _LinkVersion = 1
  _Parent = -> Elements
FEATURE [App::FeaturePython] ElementLink014  label="_Element009"  # link proxy (typed FeaturePython)
  LinkTransform = true
  LinkedObject = -> _Element009
  Offset = pos=(-6.5,-1.0338e-12,10.6723) rot=(0.707107,0,-0.707107;3.14159rad)
  Placement = pos=(-137.956,16.2771,155.128) rot=(0.707107,0,0.707107;3.14159rad)
  TreeRank = 69
  _LinkVersion = 1
  _OffsetAdded = true
  _Parent = -> Constraint007
FEATURE [Part::FeaturePython] _Element009  # link proxy (typed FeaturePython)
  Detach = false
  InvalidShape = false
  LinkTransform = true
  LinkedObject = -> Link013 [Face22]
  TreeRank = 70
  ValidateShape = true
  _LinkVersion = 1
  _Parent = -> Elements
FEATURE [App::FeaturePython] Constraint008  label="AttachmentOffset007"  # WARN: FeaturePython — macro-defined, semantics opaque (R4)
  Cascade = false
  Disabled = false
  Group = -> [ElementLink015,ElementLink016,ElementLink017,ElementLink018,ElementLink019,ElementLink020]
  Multiply = false
  TreeRank = 71
  _ConstraintType = 0
  _LinkVersion = 1
  _Parent = -> Constraints
FEATURE [App::FeaturePython] ElementLink015  label="_Element"  # link proxy (typed FeaturePython)
  LinkTransform = true
  LinkedObject = -> _Element
  TreeRank = 72
  _LinkVersion = 1
  _Parent = -> Constraint008
FEATURE [App::FeaturePython] ElementLink016  label="_Element010"  # link proxy (typed FeaturePython)
  LinkTransform = true
  LinkedObject = -> _Element010
  Offset = pos=(15.6373,-116.689,-31.9246) rot=(0.013687,0.130514,-0.991352;3.13799rad)
  Placement = pos=(225.463,-0.712898,46.4511) rot=(-0.130514,-0.013687,0.991352;3.13799rad)
  TreeRank = 73
  _LinkVersion = 1
  _OffsetAdded = true
  _Parent = -> Constraint008
FEATURE [Part::FeaturePython] _Element010  # link proxy (typed FeaturePython)
  Detach = false
  InvalidShape = false
  LinkTransform = true
  LinkedObject = -> Link014 [Face12]
  TreeRank = 74
  ValidateShape = true
  _LinkVersion = 1
  _Parent = -> Elements
FEATURE [App::FeaturePython] ElementLink017  label="_Element011"  # link proxy (typed FeaturePython)
  LinkTransform = true
  LinkedObject = -> _Element011
  Offset = pos=(-1.28836e-05,140.148,-0.314032) rot=(0,0,1;0rad)
  Placement = pos=(-140.148,1.28836e-05,0.314032) rot=(0,0,1;0rad)
  TreeRank = 75
  _LinkVersion = 1
  _OffsetAdded = true
  _Parent = -> Constraint008
FEATURE [Part::FeaturePython] _Element011  # link proxy (typed FeaturePython)
  Detach = false
  InvalidShape = false
  LinkTransform = true
  LinkedObject = -> Link007 [Face7]
  TreeRank = 76
  ValidateShape = true
  _LinkVersion = 1
  _Parent = -> Elements
FEATURE [App::FeaturePython] ElementLink018  label="_Element012"  # link proxy (typed FeaturePython)
  LinkTransform = true
  LinkedObject = -> _Element012
  Offset = pos=(159.815,1.28836e-05,-0.312925) rot=(0,0,-1;1.5708rad)
  Placement = pos=(68.0187,-211.557,0.312925) rot=(0,0,1;1.5708rad)
  TreeRank = 77
  _LinkVersion = 1
  _OffsetAdded = true
  _Parent = -> Constraint008
FEATURE [Part::FeaturePython] _Element012  # link proxy (typed FeaturePython)
  Detach = false
  InvalidShape = false
  LinkTransform = true
  LinkedObject = -> Link015 [Face3]
  TreeRank = 78
  ValidateShape = true
  _LinkVersion = 1
  _Parent = -> Elements
FEATURE [App::FeaturePython] ElementLink019  label="_Element013"  # link proxy (typed FeaturePython)
  LinkTransform = true
  LinkedObject = -> _Element013
  Offset = pos=(-1.28836e-05,175.03,-0.314032) rot=(0,0,1;0rad)
  Placement = pos=(-175.03,1.28836e-05,0.314032) rot=(0,0,1;0rad)
  TreeRank = 79
  _LinkVersion = 1
  _OffsetAdded = true
  _Parent = -> Constraint008
FEATURE [Part::FeaturePython] _Element013  # link proxy (typed FeaturePython)
  Detach = false
  InvalidShape = false
  LinkTransform = true
  LinkedObject = -> Link008 [Face4]
  TreeRank = 80
  ValidateShape = true
  _LinkVersion = 1
  _Parent = -> Elements
FEATURE [App::FeaturePython] ElementLink020  label="_Element014"  # link proxy (typed FeaturePython)
  LinkTransform = true
  LinkedObject = -> _Element014
  Offset = pos=(-1.28836e-05,-193.096,48.6694) rot=(-1,0,0;3.40339rad)
  Placement = pos=(301.87,1.28836e-05,-132.118) rot=(0,1,0;3.40339rad)
  TreeRank = 81
  _LinkVersion = 1
  _OffsetAdded = true
  _Parent = -> Constraint008
FEATURE [Part::FeaturePython] _Element014  # link proxy (typed FeaturePython)
  Detach = false
  InvalidShape = false
  LinkTransform = true
  LinkedObject = -> Link017 [Face1]
  TreeRank = 82
  ValidateShape = true
  _LinkVersion = 1
  _Parent = -> Elements
FEATURE [App::FeaturePython] Constraint009  label="AttachmentOffset008"  # WARN: FeaturePython — macro-defined, semantics opaque (R4)
  Cascade = false
  Disabled = false
  Group = -> [ElementLink021,ElementLink022]
  Multiply = false
  TreeRank = 83
  _ConstraintType = 0
  _LinkVersion = 1
  _Parent = -> Constraints
FEATURE [App::FeaturePython] ElementLink021  label="_Element015"  # link proxy (typed FeaturePython)
  LinkTransform = true
  LinkedObject = -> _Element015
  TreeRank = 84
  _LinkVersion = 1
  _Parent = -> Constraint009
FEATURE [Part::FeaturePython] _Element015  # link proxy (typed FeaturePython)
  Detach = false
  InvalidShape = false
  LinkTransform = true
  LinkedObject = -> Link007 [Face11]
  TreeRank = 85
  ValidateShape = true
  _LinkVersion = 1
  _Parent = -> Elements
FEATURE [App::FeaturePython] ElementLink022  label="_Element016"  # link proxy (typed FeaturePython)
  LinkTransform = true
  LinkedObject = -> _Element016
  Offset = pos=(-12.9409,-9.24e-14,4) rot=(0,0,1;3.14159rad)
  Placement = pos=(369.468,16.2771,94.8576) rot=(-0.258819,0,0.965926;3.14159rad)
  TreeRank = 86
  _LinkVersion = 1
  _OffsetAdded = true
  _Parent = -> Constraint009
FEATURE [Part::FeaturePython] _Element016  # link proxy (typed FeaturePython)
  Detach = false
  InvalidShape = false
  LinkTransform = true
  LinkedObject = -> Link010 [Face1]
  TreeRank = 87
  ValidateShape = true
  _LinkVersion = 1
  _Parent = -> Elements
FEATURE [App::FeaturePython] Constraint010  label="AttachmentOffset009"  # WARN: FeaturePython — macro-defined, semantics opaque (R4)
  Cascade = false
  Disabled = false
  Group = -> [ElementLink023,ElementLink024]
  Multiply = false
  TreeRank = 88
  _ConstraintType = 0
  _LinkVersion = 1
  _Parent = -> Constraints
FEATURE [App::FeaturePython] ElementLink023  label="_Element017"  # link proxy (typed FeaturePython)
  LinkTransform = true
  LinkedObject = -> _Element017
  TreeRank = 89
  _LinkVersion = 1
  _Parent = -> Constraint010
FEATURE [Part::FeaturePython] _Element017  # link proxy (typed FeaturePython)
  Detach = false
  InvalidShape = false
  LinkTransform = true
  LinkedObject = -> Link019 [Face2]
  TreeRank = 90
  ValidateShape = true
  _LinkVersion = 1
  _Parent = -> Elements
FEATURE [App::FeaturePython] ElementLink024  label="_Element018"  # link proxy (typed FeaturePython)
  LinkTransform = true
  LinkedObject = -> _Element018
  Offset = pos=(-25.5,3,-34.2031) rot=(0,0.991445,-0.130526;3.14159rad)
  Placement = pos=(456.163,41.7771,67.5579) rot=(-0.130526,0,0.991445;3.14159rad)
  TreeRank = 91
  _LinkVersion = 1
  _OffsetAdded = true
  _Parent = -> Constraint010
FEATURE [Part::FeaturePython] _Element018  # link proxy (typed FeaturePython)
  Detach = false
  InvalidShape = false
  LinkTransform = true
  LinkedObject = -> Link015 [Face5]
  TreeRank = 92
  ValidateShape = true
  _LinkVersion = 1
  _Parent = -> Elements
FEATURE [App::FeaturePython] Constraint011  label="AttachmentOffset010"  # WARN: FeaturePython — macro-defined, semantics opaque (R4)
  Cascade = false
  Disabled = false
  Group = -> [ElementLink025,ElementLink026]
  Multiply = false
  TreeRank = 93
  _ConstraintType = 0
  _LinkVersion = 1
  _Parent = -> Constraints
FEATURE [App::FeaturePython] ElementLink025  label="_Element019"  # link proxy (typed FeaturePython)
  LinkTransform = true
  LinkedObject = -> _Element019
  TreeRank = 94
  _LinkVersion = 1
  _Parent = -> Constraint011
FEATURE [Part::FeaturePython] _Element019  # link proxy (typed FeaturePython)
  Detach = false
  InvalidShape = false
  LinkTransform = true
  LinkedObject = -> Link018 [Face2]
  TreeRank = 95
  ValidateShape = true
  _LinkVersion = 1
  _Parent = -> Elements
FEATURE [App::FeaturePython] ElementLink026  label="_Element020"  # link proxy (typed FeaturePython)
  LinkTransform = true
  LinkedObject = -> _Element020
  Offset = pos=(-0.314032,1.28836e-05,17.4991) rot=(0,0,1;1.5708rad)
  Placement = pos=(17.4991,-48.2395,-13.2026) rot=(1,0,0;1.5708rad)
  TreeRank = 96
  _LinkVersion = 1
  _OffsetAdded = true
  _Parent = -> Constraint011
FEATURE [Part::FeaturePython] _Element020  # link proxy (typed FeaturePython)
  Detach = false
  InvalidShape = false
  LinkTransform = true
  LinkedObject = -> Link008 [Face15]
  TreeRank = 97
  ValidateShape = true
  _LinkVersion = 1
  _Parent = -> Elements
FEATURE [Part::FeaturePython] Assembly001  label="tarmo5"  # WARN: FeaturePython — macro-defined, semantics opaque (R4)
  AutoRelax = true
  BuildShape = 0
  Freeze = false
  Group = -> [Constraints001,Elements001,Parts001]
  InvalidShape = false
  TreeRank = 98
  ValidateShape = true
  Verbose = false
  _LinkVersion = 1
  _SolverType = 1
  _Version = 1
FEATURE [App::FeaturePython] Constraints001  # WARN: FeaturePython — macro-defined, semantics opaque (R4)
  Group = -> [Constraint012,Constraint013,Group001,Group002,Group004,Group007,Group008,Group010,Group012,Group014,Constraint107,Constraint110,Constraint111]
  TreeRank = 99
  _LinkVersion = 1
  _Version = 1
FEATURE [App::FeaturePython] Elements001  # WARN: FeaturePython — macro-defined, semantics opaque (R4)
  Group = -> [_Element021,_Element022,_Element023,_Element024,_Element025,_Element026,_Element027,_Element028,_Element029,_Element030,_Element031,_Element032,_Element033,_Element034,_Element035,_Element036,_Element037,_Element038,_Element039,_Element040,_Element041,_Element042,_Element043,_Element044,_Element045,_Element046,_Element047,_Element048,_Element049,_Element050,_Element051,_Element052,_Element053,+171 more]
  TreeRank = 100
  _LinkVersion = 1
FEATURE [Part::FeaturePython] Parts001  # WARN: FeaturePython — macro-defined, semantics opaque (R4)
  Group = -> [Assembly,Group,Group003,Group005,Group006,Group009,Group011,Group013]
  GroupMode = 0
  InvalidShape = false
  TreeRank = 101
  ValidateShape = true
  _LinkVersion = 1
FEATURE [App::FeaturePython] Constraint012  label="PlaneCoincident"  # WARN: FeaturePython — macro-defined, semantics opaque (R4)
  Angle = 0
  AnglePitch = 0
  AngleRoll = 0
  Cascade = false
  Disabled = false
  Group = -> [ElementLink027,ElementLink028]
  LockAngle = false
  Multiply = false
  OffsetX = 0
  OffsetY = 0
  TreeRank = 112
  _ConstraintType = 35
  _LinkVersion = 1
  _Parent = -> Constraints001
FEATURE [App::FeaturePython] ElementLink027  label="_Element021"  # link proxy (typed FeaturePython)
  LinkTransform = true
  LinkedObject = -> _Element021
  TreeRank = 104
  _LinkVersion = 1
  _Parent = -> Constraint012
FEATURE [Part::FeaturePython] _Element021  # link proxy (typed FeaturePython)
  Detach = false
  InvalidShape = false
  LinkTransform = true
  LinkedObject = -> Link026 [Edge39]
  TreeRank = 105
  ValidateShape = true
  _LinkVersion = 1
  _Parent = -> Elements001
FEATURE [App::FeaturePython] ElementLink028  label="_Element022"  # link proxy (typed FeaturePython)
  LinkTransform = true
  LinkedObject = -> _Element022
  TreeRank = 106
  _LinkVersion = 1
  _Parent = -> Constraint012
FEATURE [Part::FeaturePython] Element  # link proxy (typed FeaturePython)
  Detach = false
  InvalidShape = false
  LinkTransform = true
  LinkedObject = -> Link011 [Edge63]
  TreeRank = 107
  ValidateShape = true
  _LinkVersion = 1
  _Parent = -> Elements
FEATURE [Part::FeaturePython] _Element022  # link proxy (typed FeaturePython)
  Detach = false
  InvalidShape = false
  LinkTransform = true
  LinkedObject = -> Assembly [1.$Element.]
  TreeRank = 108
  ValidateShape = true
  _LinkVersion = 1
  _Parent = -> Elements001
FEATURE [App::FeaturePython] Constraint013  label="Locked001"  # WARN: FeaturePython — macro-defined, semantics opaque (R4)
  Disabled = false
  Group = -> [ElementLink029]
  TreeRank = 109
  _ConstraintType = 0
  _LinkVersion = 1
  _Parent = -> Constraints001
FEATURE [App::FeaturePython] ElementLink029  label="_Element023"  # link proxy (typed FeaturePython)
  LinkTransform = true
  LinkedObject = -> _Element023
  TreeRank = 110
  _LinkVersion = 1
  _Parent = -> Constraint013
FEATURE [Part::FeaturePython] _Element023  # link proxy (typed FeaturePython)
  Detach = false
  InvalidShape = false
  LinkTransform = true
  LinkedObject = -> Assembly [1.$_Element.]
  TreeRank = 111
  ValidateShape = true
  _LinkVersion = 1
  _Parent = -> Elements001
FEATURE [App::FeaturePython] Constraint014  label="PlaneCoincident001"  # WARN: FeaturePython — macro-defined, semantics opaque (R4)
  Angle = 0
  AnglePitch = 0
  AngleRoll = 0
  Cascade = false
  Disabled = false
  Group = -> [ElementLink030,ElementLink031]
  LockAngle = false
  Multiply = false
  OffsetX = 0
  OffsetY = 0
  TreeRank = 122
  _ConstraintType = 35
  _LinkVersion = 1
  _Parent = -> Constraints001
FEATURE [App::FeaturePython] ElementLink030  label="_Element024"  # link proxy (typed FeaturePython)
  LinkTransform = true
  LinkedObject = -> _Element024
  TreeRank = 123
  _LinkVersion = 1
  _Parent = -> Constraint014
FEATURE [Part::FeaturePython] _Element024  # link proxy (typed FeaturePython)
  Detach = false
  InvalidShape = false
  LinkTransform = true
  LinkedObject = -> Link030 [Edge38]
  TreeRank = 124
  ValidateShape = true
  _LinkVersion = 1
  _Parent = -> Elements001
FEATURE [App::FeaturePython] ElementLink031  label="_Element025"  # link proxy (typed FeaturePython)
  LinkTransform = true
  LinkedObject = -> _Element025
  TreeRank = 125
  _LinkVersion = 1
  _Parent = -> Constraint014
FEATURE [Part::FeaturePython] Element001  # link proxy (typed FeaturePython)
  Detach = false
  InvalidShape = false
  LinkTransform = true
  LinkedObject = -> Link011 [Edge61]
  TreeRank = 126
  ValidateShape = true
  _LinkVersion = 1
  _Parent = -> Elements
FEATURE [Part::FeaturePython] _Element025  # link proxy (typed FeaturePython)
  Detach = false
  InvalidShape = false
  LinkTransform = true
  LinkedObject = -> Assembly [1.$Element001.]
  TreeRank = 127
  ValidateShape = true
  _LinkVersion = 1
  _Parent = -> Elements001
FEATURE [App::FeaturePython] Constraint015  label="PlaneCoincident002"  # WARN: FeaturePython — macro-defined, semantics opaque (R4)
  Angle = 0
  AnglePitch = 0
  AngleRoll = 0
  Cascade = false
  Disabled = false
  Group = -> [ElementLink032,ElementLink033]
  LockAngle = false
  Multiply = false
  OffsetX = 0
  OffsetY = 0
  TreeRank = 128
  _ConstraintType = 35
  _LinkVersion = 1
  _Parent = -> Constraints001
FEATURE [App::FeaturePython] ElementLink032  label="_Element026"  # link proxy (typed FeaturePython)
  LinkTransform = true
  LinkedObject = -> _Element026
  TreeRank = 129
  _LinkVersion = 1
  _Parent = -> Constraint015
FEATURE [Part::FeaturePython] _Element026  # link proxy (typed FeaturePython)
  Detach = false
  InvalidShape = false
  LinkTransform = true
  LinkedObject = -> Link027 [Edge38]
  TreeRank = 130
  ValidateShape = true
  _LinkVersion = 1
  _Parent = -> Elements001
FEATURE [App::FeaturePython] ElementLink033  label="_Element027"  # link proxy (typed FeaturePython)
  LinkTransform = true
  LinkedObject = -> _Element027
  TreeRank = 131
  _LinkVersion = 1
  _Parent = -> Constraint015
FEATURE [Part::FeaturePython] Element002  # link proxy (typed FeaturePython)
  Detach = false
  InvalidShape = false
  LinkTransform = true
  LinkedObject = -> Link011 [Edge64]
  TreeRank = 132
  ValidateShape = true
  _LinkVersion = 1
  _Parent = -> Elements
FEATURE [Part::FeaturePython] _Element027  # link proxy (typed FeaturePython)
  Detach = false
  InvalidShape = false
  LinkTransform = true
  LinkedObject = -> Assembly [1.$Element002.]
  TreeRank = 133
  ValidateShape = true
  _LinkVersion = 1
  _Parent = -> Elements001
FEATURE [App::FeaturePython] Constraint016  label="PlaneCoincident003"  # WARN: FeaturePython — macro-defined, semantics opaque (R4)
  Angle = 0
  AnglePitch = 0
  AngleRoll = 0
  Cascade = false
  Disabled = false
  Group = -> [ElementLink034,ElementLink035]
  LockAngle = false
  Multiply = false
  OffsetX = 0
  OffsetY = 0
  TreeRank = 134
  _ConstraintType = 35
  _LinkVersion = 1
  _Parent = -> Constraints001
FEATURE [App::FeaturePython] ElementLink034  label="_Element028"  # link proxy (typed FeaturePython)
  LinkTransform = true
  LinkedObject = -> _Element028
  TreeRank = 135
  _LinkVersion = 1
  _Parent = -> Constraint016
FEATURE [Part::FeaturePython] Element003  # link proxy (typed FeaturePython)
  Detach = false
  InvalidShape = false
  LinkTransform = true
  LinkedObject = -> Link011 [Edge66]
  TreeRank = 136
  ValidateShape = true
  _LinkVersion = 1
  _Parent = -> Elements
FEATURE [Part::FeaturePython] _Element028  # link proxy (typed FeaturePython)
  Detach = false
  InvalidShape = false
  LinkTransform = true
  LinkedObject = -> Assembly [1.$Element003.]
  TreeRank = 137
  ValidateShape = true
  _LinkVersion = 1
  _Parent = -> Elements001
FEATURE [App::FeaturePython] ElementLink035  label="_Element029"  # link proxy (typed FeaturePython)
  LinkTransform = true
  LinkedObject = -> _Element029
  TreeRank = 138
  _LinkVersion = 1
  _Parent = -> Constraint016
FEATURE [Part::FeaturePython] _Element029  # link proxy (typed FeaturePython)
  Detach = false
  InvalidShape = false
  LinkTransform = true
  LinkedObject = -> Link028 [Edge39]
  TreeRank = 139
  ValidateShape = true
  _LinkVersion = 1
  _Parent = -> Elements001
FEATURE [App::FeaturePython] Constraint017  label="PlaneCoincident004"  # WARN: FeaturePython — macro-defined, semantics opaque (R4)
  Angle = 0
  AnglePitch = 0
  AngleRoll = 0
  Cascade = false
  Disabled = false
  Group = -> [ElementLink036,ElementLink037]
  LockAngle = false
  Multiply = false
  OffsetX = 0
  OffsetY = 0
  TreeRank = 140
  _ConstraintType = 35
  _LinkVersion = 1
  _Parent = -> Constraints001
FEATURE [App::FeaturePython] ElementLink036  label="_Element030"  # link proxy (typed FeaturePython)
  LinkTransform = true
  LinkedObject = -> _Element030
  TreeRank = 141
  _LinkVersion = 1
  _Parent = -> Constraint017
FEATURE [Part::FeaturePython] _Element030  # link proxy (typed FeaturePython)
  Detach = false
  InvalidShape = false
  LinkTransform = true
  LinkedObject = -> Link034 [Edge39]
  TreeRank = 142
  ValidateShape = true
  _LinkVersion = 1
  _Parent = -> Elements001
FEATURE [App::FeaturePython] ElementLink037  label="_Element031"  # link proxy (typed FeaturePython)
  LinkTransform = true
  LinkedObject = -> _Element031
  TreeRank = 143
  _LinkVersion = 1
  _Parent = -> Constraint017
FEATURE [Part::FeaturePython] Element004  # link proxy (typed FeaturePython)
  Detach = false
  InvalidShape = false
  LinkTransform = true
  LinkedObject = -> Link014 [Edge81]
  TreeRank = 144
  ValidateShape = true
  _LinkVersion = 1
  _Parent = -> Elements
FEATURE [Part::FeaturePython] _Element031  # link proxy (typed FeaturePython)
  Detach = false
  InvalidShape = false
  LinkTransform = true
  LinkedObject = -> Assembly [1.$Element004.]
  TreeRank = 145
  ValidateShape = true
  _LinkVersion = 1
  _Parent = -> Elements001
FEATURE [App::FeaturePython] Constraint018  label="PlaneCoincident005"  # WARN: FeaturePython — macro-defined, semantics opaque (R4)
  Angle = 0
  AnglePitch = 0
  AngleRoll = 0
  Cascade = false
  Disabled = false
  Group = -> [ElementLink038,ElementLink039]
  LockAngle = false
  Multiply = false
  OffsetX = 0
  OffsetY = 0
  TreeRank = 146
  _ConstraintType = 35
  _LinkVersion = 1
  _Parent = -> Constraints001
FEATURE [App::FeaturePython] ElementLink038  label="_Element032"  # link proxy (typed FeaturePython)
  LinkTransform = true
  LinkedObject = -> _Element032
  TreeRank = 147
  _LinkVersion = 1
  _Parent = -> Constraint018
FEATURE [Part::FeaturePython] _Element032  # link proxy (typed FeaturePython)
  Detach = false
  InvalidShape = false
  LinkTransform = true
  LinkedObject = -> Link033 [Edge38]
  TreeRank = 148
  ValidateShape = true
  _LinkVersion = 1
  _Parent = -> Elements001
FEATURE [App::FeaturePython] ElementLink039  label="_Element033"  # link proxy (typed FeaturePython)
  LinkTransform = true
  LinkedObject = -> _Element033
  TreeRank = 149
  _LinkVersion = 1
  _Parent = -> Constraint018
FEATURE [Part::FeaturePython] Element005  # link proxy (typed FeaturePython)
  Detach = false
  InvalidShape = false
  LinkTransform = true
  LinkedObject = -> Link014 [Edge82]
  TreeRank = 150
  ValidateShape = true
  _LinkVersion = 1
  _Parent = -> Elements
FEATURE [Part::FeaturePython] _Element033  # link proxy (typed FeaturePython)
  Detach = false
  InvalidShape = false
  LinkTransform = true
  LinkedObject = -> Assembly [1.$Element005.]
  TreeRank = 151
  ValidateShape = true
  _LinkVersion = 1
  _Parent = -> Elements001
FEATURE [App::FeaturePython] Constraint019  label="PlaneCoincident006"  # WARN: FeaturePython — macro-defined, semantics opaque (R4)
  Angle = 0
  AnglePitch = 0
  AngleRoll = 0
  Cascade = false
  Disabled = false
  Group = -> [ElementLink040,ElementLink041]
  LockAngle = false
  Multiply = false
  OffsetX = 0
  OffsetY = 0
  TreeRank = 152
  _ConstraintType = 35
  _LinkVersion = 1
  _Parent = -> Constraints001
FEATURE [App::FeaturePython] ElementLink040  label="_Element034"  # link proxy (typed FeaturePython)
  LinkTransform = true
  LinkedObject = -> _Element034
  TreeRank = 153
  _LinkVersion = 1
  _Parent = -> Constraint019
FEATURE [Part::FeaturePython] _Element034  # link proxy (typed FeaturePython)
  Detach = false
  InvalidShape = false
  LinkTransform = true
  LinkedObject = -> Link032 [Edge39]
  TreeRank = 154
  ValidateShape = true
  _LinkVersion = 1
  _Parent = -> Elements001
FEATURE [App::FeaturePython] ElementLink041  label="_Element035"  # link proxy (typed FeaturePython)
  LinkTransform = true
  LinkedObject = -> _Element035
  TreeRank = 155
  _LinkVersion = 1
  _Parent = -> Constraint019
FEATURE [Part::FeaturePython] Element006  # link proxy (typed FeaturePython)
  Detach = false
  InvalidShape = false
  LinkTransform = true
  LinkedObject = -> Link014 [Edge85]
  TreeRank = 156
  ValidateShape = true
  _LinkVersion = 1
  _Parent = -> Elements
FEATURE [Part::FeaturePython] _Element035  # link proxy (typed FeaturePython)
  Detach = false
  InvalidShape = false
  LinkTransform = true
  LinkedObject = -> Assembly [1.$Element006.]
  TreeRank = 157
  ValidateShape = true
  _LinkVersion = 1
  _Parent = -> Elements001
FEATURE [App::FeaturePython] Constraint020  label="PlaneCoincident007"  # WARN: FeaturePython — macro-defined, semantics opaque (R4)
  Angle = 0
  AnglePitch = 0
  AngleRoll = 0
  Cascade = false
  Disabled = false
  Group = -> [ElementLink042,ElementLink043]
  LockAngle = false
  Multiply = false
  OffsetX = 0
  OffsetY = 0
  TreeRank = 158
  _ConstraintType = 35
  _LinkVersion = 1
  _Parent = -> Constraints001
FEATURE [App::FeaturePython] ElementLink042  label="_Element036"  # link proxy (typed FeaturePython)
  LinkTransform = true
  LinkedObject = -> _Element036
  TreeRank = 159
  _LinkVersion = 1
  _Parent = -> Constraint020
FEATURE [Part::FeaturePython] _Element036  # link proxy (typed FeaturePython)
  Detach = false
  InvalidShape = false
  LinkTransform = true
  LinkedObject = -> Link031 [Edge38]
  TreeRank = 160
  ValidateShape = true
  _LinkVersion = 1
  _Parent = -> Elements001
FEATURE [App::FeaturePython] ElementLink043  label="_Element037"  # link proxy (typed FeaturePython)
  LinkTransform = true
  LinkedObject = -> _Element037
  TreeRank = 161
  _LinkVersion = 1
  _Parent = -> Constraint020
FEATURE [Part::FeaturePython] Element007  # link proxy (typed FeaturePython)
  Detach = false
  InvalidShape = false
  LinkTransform = true
  LinkedObject = -> Link014 [Edge86]
  TreeRank = 162
  ValidateShape = true
  _LinkVersion = 1
  _Parent = -> Elements
FEATURE [Part::FeaturePython] _Element037  # link proxy (typed FeaturePython)
  Detach = false
  InvalidShape = false
  LinkTransform = true
  LinkedObject = -> Assembly [1.$Element007.]
  TreeRank = 163
  ValidateShape = true
  _LinkVersion = 1
  _Parent = -> Elements001
FEATURE [Part::FeaturePython] Element008  # link proxy (typed FeaturePython)
  Detach = false
  InvalidShape = false
  LinkTransform = true
  LinkedObject = -> Link009 [Edge37]
  TreeRank = 166
  ValidateShape = true
  _LinkVersion = 1
  _Parent = -> Elements
FEATURE [Part::FeaturePython] _Element038  # link proxy (typed FeaturePython)
  Detach = false
  InvalidShape = false
  LinkTransform = true
  LinkedObject = -> Assembly [1.$Element008.]
  TreeRank = 167
  ValidateShape = true
  _LinkVersion = 1
  _Parent = -> Elements001
FEATURE [Part::FeaturePython] _Element039  label="_Element009"  # link proxy (typed FeaturePython)
  Detach = false
  InvalidShape = false
  LinkTransform = true
  LinkedObject = -> Link026 [Edge98]
  TreeRank = 169
  ValidateShape = true
  _LinkVersion = 1
  _Parent = -> Elements001
FEATURE [App::DocumentObjectGroupPython] Group  label="Suspension Arm"  # scripted group (container) (typed FeaturePython)
  ClaimAllChildren = true
  ExportMode = 0
  Group = -> [Link026,Link027,Link028,Link030,Link031,Link032,Link033,Link034]
  TreeRank = 170
  _GroupVersion = 1
  _Parent = -> Parts001
FEATURE [App::FeaturePython] Constraint021  label="PlaneCoincident008"  # WARN: FeaturePython — macro-defined, semantics opaque (R4)
  Angle = 0
  AnglePitch = 0
  AngleRoll = 0
  Cascade = false
  Disabled = false
  Group = -> [ElementLink044,ElementLink045]
  LockAngle = false
  Multiply = false
  OffsetX = 0
  OffsetY = 0
  TreeRank = 173
  _ConstraintType = 35
  _LinkVersion = 1
  _Parent = -> Constraints001
FEATURE [App::FeaturePython] ElementLink044  label="_Element040"  # link proxy (typed FeaturePython)
  LinkTransform = true
  LinkedObject = -> _Element040
  TreeRank = 174
  _LinkVersion = 1
  _Parent = -> Constraint021
FEATURE [Part::FeaturePython] _Element040  # link proxy (typed FeaturePython)
  Detach = false
  InvalidShape = false
  LinkTransform = true
  LinkedObject = -> Link036 [Edge32]
  TreeRank = 175
  ValidateShape = true
  _LinkVersion = 1
  _Parent = -> Elements001
FEATURE [App::FeaturePython] ElementLink045  label="_Element041"  # link proxy (typed FeaturePython)
  LinkTransform = true
  LinkedObject = -> _Element041
  TreeRank = 176
  _LinkVersion = 1
  _Parent = -> Constraint021
FEATURE [Part::FeaturePython] _Element041  # link proxy (typed FeaturePython)
  Detach = false
  InvalidShape = false
  LinkTransform = true
  LinkedObject = -> Link034 [Edge109]
  TreeRank = 177
  ValidateShape = true
  _LinkVersion = 1
  _Parent = -> Elements001
FEATURE [App::FeaturePython] Constraint022  label="PlaneCoincident009"  # WARN: FeaturePython — macro-defined, semantics opaque (R4)
  Angle = 0
  AnglePitch = 0
  AngleRoll = 0
  Cascade = false
  Disabled = false
  Group = -> [ElementLink046,ElementLink047]
  LockAngle = false
  Multiply = false
  OffsetX = 0
  OffsetY = 0
  TreeRank = 178
  _ConstraintType = 35
  _LinkVersion = 1
  _Parent = -> Constraints001
FEATURE [App::FeaturePython] ElementLink046  label="_Element042"  # link proxy (typed FeaturePython)
  LinkTransform = true
  LinkedObject = -> _Element042
  TreeRank = 179
  _LinkVersion = 1
  _Parent = -> Constraint022
FEATURE [Part::FeaturePython] _Element042  # link proxy (typed FeaturePython)
  Detach = false
  InvalidShape = false
  LinkTransform = true
  LinkedObject = -> Link036 [Edge31]
  TreeRank = 180
  ValidateShape = true
  _LinkVersion = 1
  _Parent = -> Elements001
FEATURE [App::FeaturePython] ElementLink047  label="_Element043"  # link proxy (typed FeaturePython)
  LinkTransform = true
  LinkedObject = -> _Element043
  TreeRank = 181
  _LinkVersion = 1
  _Parent = -> Constraint022
FEATURE [Part::FeaturePython] _Element043  # link proxy (typed FeaturePython)
  Detach = false
  InvalidShape = false
  LinkTransform = true
  LinkedObject = -> Link033 [Edge105]
  TreeRank = 182
  ValidateShape = true
  _LinkVersion = 1
  _Parent = -> Elements001
FEATURE [App::FeaturePython] Constraint023  label="PlaneCoincident010"  # WARN: FeaturePython — macro-defined, semantics opaque (R4)
  Angle = 0
  AnglePitch = 0
  AngleRoll = 0
  Cascade = false
  Disabled = false
  Group = -> [ElementLink048,ElementLink049]
  LockAngle = false
  Multiply = false
  OffsetX = 0
  OffsetY = 0
  TreeRank = 183
  _ConstraintType = 35
  _LinkVersion = 1
  _Parent = -> Constraints001
FEATURE [App::FeaturePython] ElementLink048  label="_Element044"  # link proxy (typed FeaturePython)
  LinkTransform = true
  LinkedObject = -> _Element044
  TreeRank = 184
  _LinkVersion = 1
  _Parent = -> Constraint023
FEATURE [Part::FeaturePython] _Element044  # link proxy (typed FeaturePython)
  Detach = false
  InvalidShape = false
  LinkTransform = true
  LinkedObject = -> Link035 [Edge32]
  TreeRank = 185
  ValidateShape = true
  _LinkVersion = 1
  _Parent = -> Elements001
FEATURE [App::FeaturePython] ElementLink049  label="_Element045"  # link proxy (typed FeaturePython)
  LinkTransform = true
  LinkedObject = -> _Element045
  TreeRank = 186
  _LinkVersion = 1
  _Parent = -> Constraint023
FEATURE [Part::FeaturePython] _Element045  # link proxy (typed FeaturePython)
  Detach = false
  InvalidShape = false
  LinkTransform = true
  LinkedObject = -> Link032 [Edge105]
  TreeRank = 187
  ValidateShape = true
  _LinkVersion = 1
  _Parent = -> Elements001
FEATURE [App::FeaturePython] Constraint024  label="PlaneCoincident011"  # WARN: FeaturePython — macro-defined, semantics opaque (R4)
  Angle = 0
  AnglePitch = 0
  AngleRoll = 0
  Cascade = false
  Disabled = false
  Group = -> [ElementLink050,ElementLink051]
  LockAngle = false
  Multiply = false
  OffsetX = 0
  OffsetY = 0
  TreeRank = 188
  _ConstraintType = 35
  _LinkVersion = 1
  _Parent = -> Constraints001
FEATURE [App::FeaturePython] ElementLink050  label="_Element046"  # link proxy (typed FeaturePython)
  LinkTransform = true
  LinkedObject = -> _Element046
  TreeRank = 189
  _LinkVersion = 1
  _Parent = -> Constraint024
FEATURE [Part::FeaturePython] _Element046  # link proxy (typed FeaturePython)
  Detach = false
  InvalidShape = false
  LinkTransform = true
  LinkedObject = -> Link035 [Edge31]
  TreeRank = 190
  ValidateShape = true
  _LinkVersion = 1
  _Parent = -> Elements001
FEATURE [App::FeaturePython] ElementLink051  label="_Element047"  # link proxy (typed FeaturePython)
  LinkTransform = true
  LinkedObject = -> _Element047
  TreeRank = 191
  _LinkVersion = 1
  _Parent = -> Constraint024
FEATURE [Part::FeaturePython] _Element047  # link proxy (typed FeaturePython)
  Detach = false
  InvalidShape = false
  LinkTransform = true
  LinkedObject = -> Link031 [Edge109]
  TreeRank = 192
  ValidateShape = true
  _LinkVersion = 1
  _Parent = -> Elements001
FEATURE [App::DocumentObjectGroupPython] Group001  label="Suspension Arm Cstr"  # scripted group (container) (typed FeaturePython)
  ClaimAllChildren = true
  ExportMode = 0
  Group = -> [Constraint020,Constraint014,Constraint015,Constraint016,Constraint017,Constraint018,Constraint019]
  TreeRank = 193
  _GroupVersion = 1
  _Parent = -> Constraints001
FEATURE [App::FeaturePython] Constraint025  label="PlaneCoincident012"  # WARN: FeaturePython — macro-defined, semantics opaque (R4)
  Angle = 0
  AnglePitch = 0
  AngleRoll = 0
  Cascade = false
  Disabled = false
  Group = -> [ElementLink052,ElementLink053]
  LockAngle = false
  Multiply = false
  OffsetX = 0
  OffsetY = 0
  TreeRank = 195
  _ConstraintType = 35
  _LinkVersion = 1
  _Parent = -> Constraints001
FEATURE [App::FeaturePython] ElementLink052  label="_Element048"  # link proxy (typed FeaturePython)
  LinkTransform = true
  LinkedObject = -> _Element048
  TreeRank = 196
  _LinkVersion = 1
  _Parent = -> Constraint025
FEATURE [Part::FeaturePython] _Element048  # link proxy (typed FeaturePython)
  Detach = false
  InvalidShape = false
  LinkTransform = true
  LinkedObject = -> Link029 [Edge41]
  TreeRank = 197
  ValidateShape = true
  _LinkVersion = 1
  _Parent = -> Elements001
FEATURE [App::FeaturePython] ElementLink053  label="_Element049"  # link proxy (typed FeaturePython)
  LinkTransform = true
  LinkedObject = -> _Element049
  TreeRank = 198
  _LinkVersion = 1
  _Parent = -> Constraint025
FEATURE [Part::FeaturePython] _Element049  # link proxy (typed FeaturePython)
  Detach = false
  InvalidShape = false
  LinkTransform = true
  LinkedObject = -> Link027 [Edge105]
  TreeRank = 199
  ValidateShape = true
  _LinkVersion = 1
  _Parent = -> Elements001
FEATURE [App::FeaturePython] Constraint026  label="PlaneCoincident013"  # WARN: FeaturePython — macro-defined, semantics opaque (R4)
  Angle = 0
  AnglePitch = 0
  AngleRoll = 0
  Cascade = false
  Disabled = false
  Group = -> [ElementLink054,ElementLink055]
  LockAngle = false
  Multiply = false
  OffsetX = 0
  OffsetY = 0
  TreeRank = 200
  _ConstraintType = 35
  _LinkVersion = 1
  _Parent = -> Constraints001
FEATURE [App::FeaturePython] ElementLink054  label="_Element050"  # link proxy (typed FeaturePython)
  LinkTransform = true
  LinkedObject = -> _Element050
  TreeRank = 201
  _LinkVersion = 1
  _Parent = -> Constraint026
FEATURE [Part::FeaturePython] _Element050  # link proxy (typed FeaturePython)
  Detach = false
  InvalidShape = false
  LinkTransform = true
  LinkedObject = -> Link028 [Edge109]
  TreeRank = 202
  ValidateShape = true
  _LinkVersion = 1
  _Parent = -> Elements001
FEATURE [App::FeaturePython] ElementLink055  label="_Element051"  # link proxy (typed FeaturePython)
  LinkTransform = true
  LinkedObject = -> _Element051
  TreeRank = 203
  _LinkVersion = 1
  _Parent = -> Constraint026
FEATURE [Part::FeaturePython] _Element051  # link proxy (typed FeaturePython)
  Detach = false
  InvalidShape = false
  LinkTransform = true
  LinkedObject = -> Link029 [Edge51]
  TreeRank = 204
  ValidateShape = true
  _LinkVersion = 1
  _Parent = -> Elements001
FEATURE [App::FeaturePython] Constraint027  label="PlaneCoincident014"  # WARN: FeaturePython — macro-defined, semantics opaque (R4)
  Angle = 0
  AnglePitch = 0
  AngleRoll = 0
  Cascade = false
  Disabled = false
  Group = -> [ElementLink056,ElementLink057]
  LockAngle = false
  Multiply = false
  OffsetX = 0
  OffsetY = 0
  TreeRank = 205
  _ConstraintType = 35
  _LinkVersion = 1
  _Parent = -> Constraints001
FEATURE [App::FeaturePython] ElementLink056  label="_Element052"  # link proxy (typed FeaturePython)
  LinkTransform = true
  LinkedObject = -> _Element052
  TreeRank = 206
  _LinkVersion = 1
  _Parent = -> Constraint027
FEATURE [Part::FeaturePython] _Element052  # link proxy (typed FeaturePython)
  Detach = false
  InvalidShape = false
  LinkTransform = true
  LinkedObject = -> Link037 [Edge41]
  TreeRank = 207
  ValidateShape = true
  _LinkVersion = 1
  _Parent = -> Elements001
FEATURE [App::FeaturePython] ElementLink057  label="_Element053"  # link proxy (typed FeaturePython)
  LinkTransform = true
  LinkedObject = -> _Element053
  TreeRank = 208
  _LinkVersion = 1
  _Parent = -> Constraint027
FEATURE [Part::FeaturePython] _Element053  # link proxy (typed FeaturePython)
  Detach = false
  InvalidShape = false
  LinkTransform = true
  LinkedObject = -> Link030 [Edge109]
  TreeRank = 209
  ValidateShape = true
  _LinkVersion = 1
  _Parent = -> Elements001
FEATURE [App::FeaturePython] Constraint028  label="PlaneCoincident015"  # WARN: FeaturePython — macro-defined, semantics opaque (R4)
  Angle = 0
  AnglePitch = 0
  AngleRoll = 0
  Cascade = false
  Disabled = false
  Group = -> [ElementLink058,ElementLink059]
  LockAngle = false
  Multiply = false
  OffsetX = 0
  OffsetY = 0
  TreeRank = 210
  _ConstraintType = 35
  _LinkVersion = 1
  _Parent = -> Constraints001
FEATURE [App::FeaturePython] ElementLink058  label="_Element054"  # link proxy (typed FeaturePython)
  LinkTransform = true
  LinkedObject = -> _Element054
  TreeRank = 211
  _LinkVersion = 1
  _Parent = -> Constraint028
FEATURE [Part::FeaturePython] _Element054  # link proxy (typed FeaturePython)
  Detach = false
  InvalidShape = false
  LinkTransform = true
  LinkedObject = -> Link037 [Edge51]
  TreeRank = 212
  ValidateShape = true
  _LinkVersion = 1
  _Parent = -> Elements001
FEATURE [App::FeaturePython] ElementLink059  label="_Element055"  # link proxy (typed FeaturePython)
  LinkTransform = true
  LinkedObject = -> _Element055
  TreeRank = 213
  _LinkVersion = 1
  _Parent = -> Constraint028
FEATURE [Part::FeaturePython] _Element055  # link proxy (typed FeaturePython)
  Detach = false
  InvalidShape = false
  LinkTransform = true
  LinkedObject = -> Link026 [Edge105]
  TreeRank = 214
  ValidateShape = true
  _LinkVersion = 1
  _Parent = -> Elements001
FEATURE [App::DocumentObjectGroupPython] Group002  label="moyeux Cstr"  # scripted group (container) (typed FeaturePython)
  ClaimAllChildren = true
  ExportMode = 0
  Group = -> [Constraint021,Constraint022,Constraint023,Constraint024,Constraint025,Constraint026,Constraint027,Constraint028,Constraint065,Constraint066,Constraint067]
  TreeRank = 215
  _GroupVersion = 1
  _Parent = -> Constraints001
FEATURE [App::DocumentObjectGroupPython] Group003  label="Moyeux"  # scripted group (container) (typed FeaturePython)
  ClaimAllChildren = true
  ExportMode = 0
  Group = -> [Link035,Link036,Link029,Link037,Link065,Link066]
  TreeRank = 216
  _GroupVersion = 1
  _Parent = -> Parts001
FEATURE [App::FeaturePython] Constraint029  label="Direction angle"  # WARN: FeaturePython — macro-defined, semantics opaque (R4)
  Angle = 1
  AnglePitch = 0
  AngleRoll = 0
  Cascade = false
  Disabled = false
  Group = -> [ElementLink060,ElementLink061]
  LockAngle = true
  Multiply = false
  OffsetX = 0
  OffsetY = 0
  TreeRank = 219
  _ConstraintType = 35
  _LinkVersion = 1
  _Parent = -> Constraints001
FEATURE [App::FeaturePython] ElementLink060  label="_Element056"  # link proxy (typed FeaturePython)
  LinkTransform = true
  LinkedObject = -> _Element056
  TreeRank = 220
  _LinkVersion = 1
  _Parent = -> Constraint029
FEATURE [Part::FeaturePython] _Element056  # link proxy (typed FeaturePython)
  Detach = false
  InvalidShape = false
  LinkTransform = true
  LinkedObject = -> Link036 [Edge61]
  TreeRank = 221
  ValidateShape = true
  _LinkVersion = 1
  _Parent = -> Elements001
FEATURE [App::FeaturePython] ElementLink061  label="_Element057"  # link proxy (typed FeaturePython)
  LinkTransform = true
  LinkedObject = -> _Element057
  TreeRank = 222
  _LinkVersion = 1
  _Parent = -> Constraint029
FEATURE [Part::FeaturePython] _Element057  # link proxy (typed FeaturePython)
  Detach = false
  InvalidShape = false
  LinkTransform = true
  LinkedObject = -> Link039 [Edge31]
  TreeRank = 223
  ValidateShape = true
  _LinkVersion = 1
  _Parent = -> Elements001
FEATURE [App::FeaturePython] Constraint030  label="PlaneCoincident017"  # WARN: FeaturePython — macro-defined, semantics opaque (R4)
  Angle = 0
  AnglePitch = 0
  AngleRoll = 0
  Cascade = false
  Disabled = false
  Group = -> [ElementLink062,ElementLink063]
  LockAngle = false
  Multiply = false
  OffsetX = 0
  OffsetY = 0
  TreeRank = 224
  _ConstraintType = 35
  _LinkVersion = 1
  _Parent = -> Constraints001
FEATURE [App::FeaturePython] ElementLink062  label="_Element058"  # link proxy (typed FeaturePython)
  LinkTransform = true
  LinkedObject = -> _Element058
  TreeRank = 225
  _LinkVersion = 1
  _Parent = -> Constraint030
FEATURE [Part::FeaturePython] _Element058  # link proxy (typed FeaturePython)
  Detach = false
  InvalidShape = false
  LinkTransform = true
  LinkedObject = -> Link038 [Edge31]
  TreeRank = 226
  ValidateShape = true
  _LinkVersion = 1
  _Parent = -> Elements001
FEATURE [App::FeaturePython] ElementLink063  label="_Element059"  # link proxy (typed FeaturePython)
  LinkTransform = true
  LinkedObject = -> _Element059
  TreeRank = 227
  _LinkVersion = 1
  _Parent = -> Constraint030
FEATURE [Part::FeaturePython] _Element059  # link proxy (typed FeaturePython)
  Detach = false
  InvalidShape = false
  LinkTransform = true
  LinkedObject = -> Link035 [Edge61]
  TreeRank = 228
  ValidateShape = true
  _LinkVersion = 1
  _Parent = -> Elements001
FEATURE [App::FeaturePython] Constraint031  label="PlaneCoincident018"  # WARN: FeaturePython — macro-defined, semantics opaque (R4)
  Angle = 0
  AnglePitch = 0
  AngleRoll = 0
  Cascade = false
  Disabled = false
  Group = -> [ElementLink064,ElementLink065]
  LockAngle = false
  Multiply = false
  OffsetX = 0
  OffsetY = 0
  TreeRank = 231
  _ConstraintType = 35
  _LinkVersion = 1
  _Parent = -> Constraints001
FEATURE [App::FeaturePython] ElementLink064  label="_Element060"  # link proxy (typed FeaturePython)
  LinkTransform = true
  LinkedObject = -> _Element060
  TreeRank = 232
  _LinkVersion = 1
  _Parent = -> Constraint031
FEATURE [Part::FeaturePython] _Element060  # link proxy (typed FeaturePython)
  Detach = false
  InvalidShape = false
  LinkTransform = true
  LinkedObject = -> Link041 [Edge27]
  TreeRank = 233
  ValidateShape = true
  _LinkVersion = 1
  _Parent = -> Elements001
FEATURE [App::FeaturePython] ElementLink065  label="_Element061"  # link proxy (typed FeaturePython)
  LinkTransform = true
  LinkedObject = -> _Element061
  TreeRank = 234
  _LinkVersion = 1
  _Parent = -> Constraint031
FEATURE [Part::FeaturePython] Element009  # link proxy (typed FeaturePython)
  Detach = false
  InvalidShape = false
  LinkTransform = true
  LinkedObject = -> Link006 [Edge133]
  TreeRank = 235
  ValidateShape = true
  _LinkVersion = 1
  _Parent = -> Elements
FEATURE [Part::FeaturePython] _Element061  # link proxy (typed FeaturePython)
  Detach = false
  InvalidShape = false
  LinkTransform = true
  LinkedObject = -> Assembly [1.$Element009.]
  TreeRank = 236
  ValidateShape = true
  _LinkVersion = 1
  _Parent = -> Elements001
FEATURE [App::FeaturePython] Constraint032  label="PlaneCoincident019"  # WARN: FeaturePython — macro-defined, semantics opaque (R4)
  Angle = 0
  AnglePitch = 0
  AngleRoll = 0
  Cascade = false
  Disabled = false
  Group = -> [ElementLink066,ElementLink067]
  LockAngle = false
  Multiply = false
  OffsetX = 0
  OffsetY = 0
  TreeRank = 237
  _ConstraintType = 35
  _LinkVersion = 1
  _Parent = -> Constraints001
FEATURE [App::FeaturePython] ElementLink066  label="_Element062"  # link proxy (typed FeaturePython)
  LinkTransform = true
  LinkedObject = -> _Element062
  TreeRank = 238
  _LinkVersion = 1
  _Parent = -> Constraint032
FEATURE [Part::FeaturePython] _Element062  # link proxy (typed FeaturePython)
  Detach = false
  InvalidShape = false
  LinkTransform = true
  LinkedObject = -> Link040 [Edge27]
  TreeRank = 239
  ValidateShape = true
  _LinkVersion = 1
  _Parent = -> Elements001
FEATURE [App::FeaturePython] ElementLink067  label="_Element063"  # link proxy (typed FeaturePython)
  LinkTransform = true
  LinkedObject = -> _Element063
  TreeRank = 240
  _LinkVersion = 1
  _Parent = -> Constraint032
FEATURE [Part::FeaturePython] Element010  # link proxy (typed FeaturePython)
  Detach = false
  InvalidShape = false
  LinkTransform = true
  LinkedObject = -> Link006 [Edge150]
  TreeRank = 241
  ValidateShape = true
  _LinkVersion = 1
  _Parent = -> Elements
FEATURE [Part::FeaturePython] _Element063  # link proxy (typed FeaturePython)
  Detach = false
  InvalidShape = false
  LinkTransform = true
  LinkedObject = -> Assembly [1.$Element010.]
  TreeRank = 242
  ValidateShape = true
  _LinkVersion = 1
  _Parent = -> Elements001
FEATURE [App::FeaturePython] Constraint033  label="PlaneCoincident020"  # WARN: FeaturePython — macro-defined, semantics opaque (R4)
  Angle = 0
  AnglePitch = 0
  AngleRoll = 0
  Cascade = false
  Disabled = false
  Group = -> [ElementLink068,ElementLink069]
  LockAngle = false
  Multiply = false
  OffsetX = 0
  OffsetY = 0
  TreeRank = 246
  _ConstraintType = 35
  _LinkVersion = 1
  _Parent = -> Constraints001
FEATURE [App::FeaturePython] ElementLink068  label="_Element064"  # link proxy (typed FeaturePython)
  LinkTransform = true
  LinkedObject = -> _Element064
  TreeRank = 247
  _LinkVersion = 1
  _Parent = -> Constraint033
FEATURE [Part::FeaturePython] _Element064  # link proxy (typed FeaturePython)
  Detach = false
  InvalidShape = false
  LinkTransform = true
  LinkedObject = -> Link043 [Edge6]
  TreeRank = 248
  ValidateShape = true
  _LinkVersion = 1
  _Parent = -> Elements001
FEATURE [App::FeaturePython] ElementLink069  label="_Element065"  # link proxy (typed FeaturePython)
  LinkTransform = true
  LinkedObject = -> _Element065
  TreeRank = 249
  _LinkVersion = 1
  _Parent = -> Constraint033
FEATURE [Part::FeaturePython] _Element065  # link proxy (typed FeaturePython)
  Detach = false
  InvalidShape = false
  LinkTransform = true
  LinkedObject = -> Link041 [Edge58]
  TreeRank = 250
  ValidateShape = true
  _LinkVersion = 1
  _Parent = -> Elements001
FEATURE [App::FeaturePython] Constraint034  label="PointsCoincident"  # WARN: FeaturePython — macro-defined, semantics opaque (R4)
  Disabled = false
  Group = -> [ElementLink070,ElementLink071]
  TreeRank = 251
  _ConstraintType = 1
  _LinkVersion = 1
  _Parent = -> Constraints001
FEATURE [App::FeaturePython] ElementLink070  label="_Element066"  # link proxy (typed FeaturePython)
  LinkTransform = true
  LinkedObject = -> _Element066
  TreeRank = 252
  _LinkVersion = 1
  _Parent = -> Constraint034
FEATURE [Part::FeaturePython] _Element066  # link proxy (typed FeaturePython)
  Detach = false
  InvalidShape = false
  LinkTransform = true
  LinkedObject = -> Link044 [Face6]
  TreeRank = 253
  ValidateShape = true
  _LinkVersion = 1
  _Parent = -> Elements001
FEATURE [App::FeaturePython] ElementLink071  label="_Element067"  # link proxy (typed FeaturePython)
  LinkTransform = true
  LinkedObject = -> _Element067
  TreeRank = 254
  _LinkVersion = 1
  _Parent = -> Constraint034
FEATURE [Part::FeaturePython] _Element067  # link proxy (typed FeaturePython)
  Detach = false
  InvalidShape = false
  LinkTransform = true
  LinkedObject = -> Link043 [Face1]
  TreeRank = 255
  ValidateShape = true
  _LinkVersion = 1
  _Parent = -> Elements001
FEATURE [App::FeaturePython] Constraint035  label="PlaneCoincident021"  # WARN: FeaturePython — macro-defined, semantics opaque (R4)
  Angle = 0
  AnglePitch = 0
  AngleRoll = 0
  Cascade = false
  Disabled = false
  Group = -> [ElementLink072,ElementLink073]
  LockAngle = false
  Multiply = false
  OffsetX = 0
  OffsetY = 0
  TreeRank = 256
  _ConstraintType = 35
  _LinkVersion = 1
  _Parent = -> Constraints001
FEATURE [App::FeaturePython] ElementLink072  label="_Element068"  # link proxy (typed FeaturePython)
  LinkTransform = true
  LinkedObject = -> _Element068
  TreeRank = 257
  _LinkVersion = 1
  _Parent = -> Constraint035
FEATURE [Part::FeaturePython] _Element068  # link proxy (typed FeaturePython)
  Detach = false
  InvalidShape = false
  LinkTransform = true
  LinkedObject = -> Link042 [Edge6]
  TreeRank = 258
  ValidateShape = true
  _LinkVersion = 1
  _Parent = -> Elements001
FEATURE [App::FeaturePython] ElementLink073  label="_Element069"  # link proxy (typed FeaturePython)
  LinkTransform = true
  LinkedObject = -> _Element069
  TreeRank = 259
  _LinkVersion = 1
  _Parent = -> Constraint035
FEATURE [Part::FeaturePython] _Element069  # link proxy (typed FeaturePython)
  Detach = false
  InvalidShape = false
  LinkTransform = true
  LinkedObject = -> Link039 [Edge124]
  TreeRank = 260
  ValidateShape = true
  _LinkVersion = 1
  _Parent = -> Elements001
FEATURE [App::FeaturePython] Constraint036  label="PointsCoincident001"  # WARN: FeaturePython — macro-defined, semantics opaque (R4)
  Disabled = false
  Group = -> [ElementLink074,ElementLink075]
  TreeRank = 261
  _ConstraintType = 1
  _LinkVersion = 1
  _Parent = -> Constraints001
FEATURE [App::FeaturePython] ElementLink074  label="_Element070"  # link proxy (typed FeaturePython)
  LinkTransform = true
  LinkedObject = -> _Element070
  TreeRank = 262
  _LinkVersion = 1
  _Parent = -> Constraint036
FEATURE [Part::FeaturePython] _Element070  # link proxy (typed FeaturePython)
  Detach = false
  InvalidShape = false
  LinkTransform = true
  LinkedObject = -> Link044 [Face3]
  TreeRank = 263
  ValidateShape = true
  _LinkVersion = 1
  _Parent = -> Elements001
FEATURE [App::FeaturePython] ElementLink075  label="_Element071"  # link proxy (typed FeaturePython)
  LinkTransform = true
  LinkedObject = -> _Element071
  TreeRank = 264
  _LinkVersion = 1
  _Parent = -> Constraint036
FEATURE [Part::FeaturePython] _Element071  # link proxy (typed FeaturePython)
  Detach = false
  InvalidShape = false
  LinkTransform = true
  LinkedObject = -> Link042 [Face1]
  TreeRank = 265
  ValidateShape = true
  _LinkVersion = 1
  _Parent = -> Elements001
FEATURE [App::FeaturePython] Constraint037  label="PlaneCoincident022"  # WARN: FeaturePython — macro-defined, semantics opaque (R4)
  Angle = 0
  AnglePitch = 0
  AngleRoll = 0
  Cascade = false
  Disabled = false
  Group = -> [ElementLink076,ElementLink077]
  LockAngle = false
  Multiply = false
  OffsetX = 0
  OffsetY = 0
  TreeRank = 269
  _ConstraintType = 35
  _LinkVersion = 1
  _Parent = -> Constraints001
FEATURE [App::FeaturePython] ElementLink076  label="_Element072"  # link proxy (typed FeaturePython)
  LinkTransform = true
  LinkedObject = -> _Element072
  TreeRank = 270
  _LinkVersion = 1
  _Parent = -> Constraint037
FEATURE [Part::FeaturePython] _Element072  # link proxy (typed FeaturePython)
  Detach = false
  InvalidShape = false
  LinkTransform = true
  LinkedObject = -> Link045 [Edge6]
  TreeRank = 271
  ValidateShape = true
  _LinkVersion = 1
  _Parent = -> Elements001
FEATURE [App::FeaturePython] ElementLink077  label="_Element073"  # link proxy (typed FeaturePython)
  LinkTransform = true
  LinkedObject = -> _Element073
  TreeRank = 272
  _LinkVersion = 1
  _Parent = -> Constraint037
FEATURE [Part::FeaturePython] _Element073  # link proxy (typed FeaturePython)
  Detach = false
  InvalidShape = false
  LinkTransform = true
  LinkedObject = -> Link038 [Edge124]
  TreeRank = 273
  ValidateShape = true
  _LinkVersion = 1
  _Parent = -> Elements001
FEATURE [App::FeaturePython] Constraint038  label="PlaneCoincident023"  # WARN: FeaturePython — macro-defined, semantics opaque (R4)
  Angle = 0
  AnglePitch = 0
  AngleRoll = 0
  Cascade = false
  Disabled = false
  Group = -> [ElementLink078,ElementLink079]
  LockAngle = false
  Multiply = false
  OffsetX = 0
  OffsetY = 0
  TreeRank = 274
  _ConstraintType = 35
  _LinkVersion = 1
  _Parent = -> Constraints001
FEATURE [App::FeaturePython] ElementLink078  label="_Element074"  # link proxy (typed FeaturePython)
  LinkTransform = true
  LinkedObject = -> _Element074
  TreeRank = 275
  _LinkVersion = 1
  _Parent = -> Constraint038
FEATURE [Part::FeaturePython] _Element074  # link proxy (typed FeaturePython)
  Detach = false
  InvalidShape = false
  LinkTransform = true
  LinkedObject = -> Link047 [Edge6]
  TreeRank = 276
  ValidateShape = true
  _LinkVersion = 1
  _Parent = -> Elements001
FEATURE [App::FeaturePython] ElementLink079  label="_Element075"  # link proxy (typed FeaturePython)
  LinkTransform = true
  LinkedObject = -> _Element075
  TreeRank = 277
  _LinkVersion = 1
  _Parent = -> Constraint038
FEATURE [Part::FeaturePython] _Element075  # link proxy (typed FeaturePython)
  Detach = false
  InvalidShape = false
  LinkTransform = true
  LinkedObject = -> Link040 [Edge58]
  TreeRank = 278
  ValidateShape = true
  _LinkVersion = 1
  _Parent = -> Elements001
FEATURE [App::FeaturePython] Constraint039  label="PointsCoincident002"  # WARN: FeaturePython — macro-defined, semantics opaque (R4)
  Disabled = false
  Group = -> [ElementLink080,ElementLink081]
  TreeRank = 279
  _ConstraintType = 1
  _LinkVersion = 1
  _Parent = -> Constraints001
FEATURE [App::FeaturePython] ElementLink080  label="_Element076"  # link proxy (typed FeaturePython)
  LinkTransform = true
  LinkedObject = -> _Element076
  TreeRank = 280
  _LinkVersion = 1
  _Parent = -> Constraint039
FEATURE [Part::FeaturePython] _Element076  # link proxy (typed FeaturePython)
  Detach = false
  InvalidShape = false
  LinkTransform = true
  LinkedObject = -> Link046 [Face3]
  TreeRank = 281
  ValidateShape = true
  _LinkVersion = 1
  _Parent = -> Elements001
FEATURE [App::FeaturePython] ElementLink081  label="_Element077"  # link proxy (typed FeaturePython)
  LinkTransform = true
  LinkedObject = -> _Element077
  TreeRank = 282
  _LinkVersion = 1
  _Parent = -> Constraint039
FEATURE [Part::FeaturePython] _Element077  # link proxy (typed FeaturePython)
  Detach = false
  InvalidShape = false
  LinkTransform = true
  LinkedObject = -> Link045 [Face1]
  TreeRank = 283
  ValidateShape = true
  _LinkVersion = 1
  _Parent = -> Elements001
FEATURE [App::FeaturePython] Constraint040  label="PointsCoincident003"  # WARN: FeaturePython — macro-defined, semantics opaque (R4)
  Disabled = false
  Group = -> [ElementLink082,ElementLink083]
  TreeRank = 284
  _ConstraintType = 1
  _LinkVersion = 1
  _Parent = -> Constraints001
FEATURE [App::FeaturePython] ElementLink082  label="_Element078"  # link proxy (typed FeaturePython)
  LinkTransform = true
  LinkedObject = -> _Element078
  TreeRank = 285
  _LinkVersion = 1
  _Parent = -> Constraint040
FEATURE [Part::FeaturePython] _Element078  # link proxy (typed FeaturePython)
  Detach = false
  InvalidShape = false
  LinkTransform = true
  LinkedObject = -> Link046 [Face6]
  TreeRank = 286
  ValidateShape = true
  _LinkVersion = 1
  _Parent = -> Elements001
FEATURE [App::FeaturePython] ElementLink083  label="_Element079"  # link proxy (typed FeaturePython)
  LinkTransform = true
  LinkedObject = -> _Element079
  TreeRank = 287
  _LinkVersion = 1
  _Parent = -> Constraint040
FEATURE [Part::FeaturePython] _Element079  # link proxy (typed FeaturePython)
  Detach = false
  InvalidShape = false
  LinkTransform = true
  LinkedObject = -> Link047 [Face1]
  TreeRank = 288
  ValidateShape = true
  _LinkVersion = 1
  _Parent = -> Elements001
FEATURE [App::FeaturePython] Constraint041  label="PlaneCoincident024"  # WARN: FeaturePython — macro-defined, semantics opaque (R4)
  Angle = 0
  AnglePitch = 0
  AngleRoll = 0
  Cascade = false
  Disabled = false
  Group = -> [ElementLink084,ElementLink085]
  LockAngle = false
  Multiply = false
  OffsetX = 0
  OffsetY = 0
  TreeRank = 290
  _ConstraintType = 35
  _LinkVersion = 1
  _Parent = -> Constraints001
FEATURE [App::FeaturePython] ElementLink084  label="_Element080"  # link proxy (typed FeaturePython)
  LinkTransform = true
  LinkedObject = -> _Element080
  TreeRank = 291
  _LinkVersion = 1
  _Parent = -> Constraint041
FEATURE [Part::FeaturePython] _Element080  # link proxy (typed FeaturePython)
  Detach = false
  InvalidShape = false
  LinkTransform = true
  LinkedObject = -> Link048 [Edge17]
  TreeRank = 292
  ValidateShape = true
  _LinkVersion = 1
  _Parent = -> Elements001
FEATURE [App::FeaturePython] ElementLink085  label="_Element081"  # link proxy (typed FeaturePython)
  LinkTransform = true
  LinkedObject = -> _Element081
  TreeRank = 293
  _LinkVersion = 1
  _Parent = -> Constraint041
FEATURE [Part::FeaturePython] _Element081  # link proxy (typed FeaturePython)
  Detach = false
  InvalidShape = false
  LinkTransform = true
  LinkedObject = -> Link040 [Edge16]
  TreeRank = 294
  ValidateShape = true
  _LinkVersion = 1
  _Parent = -> Elements001
FEATURE [App::FeaturePython] Constraint042  label="PointsCoincident004"  # WARN: FeaturePython — macro-defined, semantics opaque (R4)
  Disabled = false
  Group = -> [ElementLink086,ElementLink087]
  TreeRank = 295
  _ConstraintType = 1
  _LinkVersion = 1
  _Parent = -> Constraints001
FEATURE [App::FeaturePython] ElementLink086  label="_Element082"  # link proxy (typed FeaturePython)
  LinkTransform = true
  LinkedObject = -> _Element082
  TreeRank = 296
  _LinkVersion = 1
  _Parent = -> Constraint042
FEATURE [Part::FeaturePython] _Element082  # link proxy (typed FeaturePython)
  Detach = false
  InvalidShape = false
  LinkTransform = true
  LinkedObject = -> Link048 [Edge20]
  TreeRank = 297
  ValidateShape = true
  _LinkVersion = 1
  _Parent = -> Elements001
FEATURE [App::FeaturePython] ElementLink087  label="_Element083"  # link proxy (typed FeaturePython)
  LinkTransform = true
  LinkedObject = -> _Element083
  TreeRank = 298
  _LinkVersion = 1
  _Parent = -> Constraint042
FEATURE [Part::FeaturePython] _Element083  # link proxy (typed FeaturePython)
  Detach = false
  InvalidShape = false
  LinkTransform = true
  LinkedObject = -> Link041 [Edge16]
  TreeRank = 299
  ValidateShape = true
  _LinkVersion = 1
  _Parent = -> Elements001
FEATURE [App::FeaturePython] Constraint043  label="PlaneCoincident025"  # WARN: FeaturePython — macro-defined, semantics opaque (R4)
  Angle = 0
  AnglePitch = 0
  AngleRoll = 0
  Cascade = false
  Disabled = false
  Group = -> [ElementLink088,ElementLink089]
  LockAngle = false
  Multiply = false
  OffsetX = 0
  OffsetY = 0
  TreeRank = 302
  _ConstraintType = 35
  _LinkVersion = 1
  _Parent = -> Constraints001
FEATURE [App::FeaturePython] ElementLink088  label="_Element084"  # link proxy (typed FeaturePython)
  LinkTransform = true
  LinkedObject = -> _Element084
  TreeRank = 303
  _LinkVersion = 1
  _Parent = -> Constraint043
FEATURE [Part::FeaturePython] _Element084  # link proxy (typed FeaturePython)
  Detach = false
  InvalidShape = false
  LinkTransform = true
  LinkedObject = -> Link050 [Edge20]
  TreeRank = 304
  ValidateShape = true
  _LinkVersion = 1
  _Parent = -> Elements001
FEATURE [App::FeaturePython] ElementLink089  label="_Element085"  # link proxy (typed FeaturePython)
  LinkTransform = true
  LinkedObject = -> _Element085
  TreeRank = 305
  _LinkVersion = 1
  _Parent = -> Constraint043
FEATURE [Part::FeaturePython] _Element085  # link proxy (typed FeaturePython)
  Detach = false
  InvalidShape = false
  LinkTransform = true
  LinkedObject = -> Link048 [Edge4]
  TreeRank = 306
  ValidateShape = true
  _LinkVersion = 1
  _Parent = -> Elements001
FEATURE [App::FeaturePython] Constraint044  label="PlaneCoincident026"  # WARN: FeaturePython — macro-defined, semantics opaque (R4)
  Angle = 0
  AnglePitch = 0
  AngleRoll = 0
  Cascade = false
  Disabled = false
  Group = -> [ElementLink090,ElementLink091]
  LockAngle = false
  Multiply = false
  OffsetX = 0
  OffsetY = 0
  TreeRank = 307
  _ConstraintType = 35
  _LinkVersion = 1
  _Parent = -> Constraints001
FEATURE [App::FeaturePython] ElementLink090  label="_Element086"  # link proxy (typed FeaturePython)
  LinkTransform = true
  LinkedObject = -> _Element086
  TreeRank = 308
  _LinkVersion = 1
  _Parent = -> Constraint044
FEATURE [Part::FeaturePython] _Element086  # link proxy (typed FeaturePython)
  Detach = false
  InvalidShape = false
  LinkTransform = true
  LinkedObject = -> Link049 [Edge97]
  TreeRank = 309
  ValidateShape = true
  _LinkVersion = 1
  _Parent = -> Elements001
FEATURE [App::FeaturePython] ElementLink091  label="_Element087"  # link proxy (typed FeaturePython)
  LinkTransform = true
  LinkedObject = -> _Element087
  TreeRank = 310
  _LinkVersion = 1
  _Parent = -> Constraint044
FEATURE [Part::FeaturePython] Element011  # link proxy (typed FeaturePython)
  Detach = false
  InvalidShape = false
  LinkTransform = true
  LinkedObject = -> Link006 [Edge51]
  TreeRank = 311
  ValidateShape = true
  _LinkVersion = 1
  _Parent = -> Elements
FEATURE [Part::FeaturePython] _Element087  # link proxy (typed FeaturePython)
  Detach = false
  InvalidShape = false
  LinkTransform = true
  LinkedObject = -> Assembly [1.$Element011.]
  TreeRank = 312
  ValidateShape = true
  _LinkVersion = 1
  _Parent = -> Elements001
FEATURE [Part::FeaturePython] _Element088  # link proxy (typed FeaturePython)
  Detach = false
  InvalidShape = false
  LinkTransform = true
  LinkedObject = -> Link049 [Face16]
  TreeRank = 315
  ValidateShape = true
  _LinkVersion = 1
  _Parent = -> Elements001
FEATURE [Part::FeaturePython] Element012  # link proxy (typed FeaturePython)
  Detach = false
  InvalidShape = false
  LinkTransform = true
  LinkedObject = -> Link006 [Vertex238]
  TreeRank = 318
  ValidateShape = true
  _LinkVersion = 1
  _Parent = -> Elements
FEATURE [Part::FeaturePython] _Element089  # link proxy (typed FeaturePython)
  Detach = false
  InvalidShape = false
  LinkTransform = true
  LinkedObject = -> Assembly [1.$Element012.]
  TreeRank = 319
  ValidateShape = true
  _LinkVersion = 1
  _Parent = -> Elements001
FEATURE [Part::FeaturePython] _Element090  # link proxy (typed FeaturePython)
  Detach = false
  InvalidShape = false
  LinkTransform = true
  LinkedObject = -> Link049 [Face3]
  TreeRank = 321
  ValidateShape = true
  _LinkVersion = 1
  _Parent = -> Elements001
FEATURE [Part::FeaturePython] _Element091  # link proxy (typed FeaturePython)
  Detach = false
  InvalidShape = false
  LinkTransform = true
  LinkedObject = -> Link050 [Face20]
  TreeRank = 324
  ValidateShape = true
  _LinkVersion = 1
  _Parent = -> Elements001
FEATURE [Part::FeaturePython] _Element092  # link proxy (typed FeaturePython)
  Detach = false
  InvalidShape = false
  LinkTransform = true
  LinkedObject = -> Link049 [Face1]
  TreeRank = 326
  ValidateShape = true
  _LinkVersion = 1
  _Parent = -> Elements001
FEATURE [App::DocumentObjectGroupPython] Group004  label="Direction Cstr"  # scripted group (container) (typed FeaturePython)
  ClaimAllChildren = true
  ExportMode = 0
  Group = -> [Constraint030,Constraint031,Constraint032,Constraint033,Constraint034,Constraint035,Constraint036,Constraint037,Constraint038,Constraint039,Constraint040,Constraint041,Constraint042,Constraint043,Constraint044]
  TreeRank = 327
  _GroupVersion = 1
  _Parent = -> Constraints001
FEATURE [App::DocumentObjectGroupPython] Group005  label="Direction"  # scripted group (container) (typed FeaturePython)
  ClaimAllChildren = true
  ExportMode = 0
  Group = -> [Link038,Link039,Link040,Link041,Link042,Link043,Link044,Link045,Link046,Link047,Link048,Link049,Link050]
  TreeRank = 328
  _GroupVersion = 1
  _Parent = -> Parts001
FEATURE [App::FeaturePython] Constraint045  label="PlaneCoincident027"  # WARN: FeaturePython — macro-defined, semantics opaque (R4)
  Angle = 0
  AnglePitch = 0
  AngleRoll = 0
  Cascade = false
  Disabled = false
  Group = -> [ElementLink092,ElementLink093]
  LockAngle = false
  Multiply = false
  OffsetX = 0
  OffsetY = 0
  TreeRank = 333
  _ConstraintType = 35
  _LinkVersion = 1
  _Parent = -> Constraints001
FEATURE [App::FeaturePython] ElementLink092  label="_Element093"  # link proxy (typed FeaturePython)
  LinkTransform = true
  LinkedObject = -> _Element093
  TreeRank = 334
  _LinkVersion = 1
  _Parent = -> Constraint045
FEATURE [Part::FeaturePython] _Element093  # link proxy (typed FeaturePython)
  Detach = false
  InvalidShape = false
  LinkTransform = true
  LinkedObject = -> Link039 [Edge107]
  TreeRank = 335
  ValidateShape = true
  _LinkVersion = 1
  _Parent = -> Elements001
FEATURE [App::FeaturePython] ElementLink093  label="_Element094"  # link proxy (typed FeaturePython)
  LinkTransform = true
  LinkedObject = -> _Element094
  TreeRank = 336
  _LinkVersion = 1
  _Parent = -> Constraint045
FEATURE [Part::FeaturePython] _Element094  # link proxy (typed FeaturePython)
  Detach = false
  InvalidShape = false
  LinkTransform = true
  LinkedObject = -> Link053 [Edge10]
  TreeRank = 337
  ValidateShape = true
  _LinkVersion = 1
  _Parent = -> Elements001
FEATURE [App::FeaturePython] Constraint046  label="PlaneCoincident028"  # WARN: FeaturePython — macro-defined, semantics opaque (R4)
  Angle = 0
  AnglePitch = 0
  AngleRoll = 0
  Cascade = false
  Disabled = false
  Group = -> [ElementLink094,ElementLink095]
  LockAngle = false
  Multiply = false
  OffsetX = 0
  OffsetY = 0
  TreeRank = 338
  _ConstraintType = 35
  _LinkVersion = 1
  _Parent = -> Constraints001
FEATURE [App::FeaturePython] ElementLink094  label="_Element095"  # link proxy (typed FeaturePython)
  LinkTransform = true
  LinkedObject = -> _Element095
  TreeRank = 339
  _LinkVersion = 1
  _Parent = -> Constraint046
FEATURE [Part::FeaturePython] _Element095  # link proxy (typed FeaturePython)
  Detach = false
  InvalidShape = false
  LinkTransform = true
  LinkedObject = -> Link039 [Edge48]
  TreeRank = 340
  ValidateShape = true
  _LinkVersion = 1
  _Parent = -> Elements001
FEATURE [App::FeaturePython] ElementLink095  label="_Element096"  # link proxy (typed FeaturePython)
  LinkTransform = true
  LinkedObject = -> _Element096
  TreeRank = 341
  _LinkVersion = 1
  _Parent = -> Constraint046
FEATURE [Part::FeaturePython] _Element096  # link proxy (typed FeaturePython)
  Detach = false
  InvalidShape = false
  LinkTransform = true
  LinkedObject = -> Link051 [Edge10]
  TreeRank = 342
  ValidateShape = true
  _LinkVersion = 1
  _Parent = -> Elements001
FEATURE [App::FeaturePython] Constraint047  label="PlaneCoincident029"  # WARN: FeaturePython — macro-defined, semantics opaque (R4)
  Angle = 0
  AnglePitch = 0
  AngleRoll = 0
  Cascade = false
  Disabled = false
  Group = -> [ElementLink096,ElementLink097]
  LockAngle = false
  Multiply = false
  OffsetX = 0
  OffsetY = 0
  TreeRank = 343
  _ConstraintType = 35
  _LinkVersion = 1
  _Parent = -> Constraints001
FEATURE [App::FeaturePython] ElementLink096  label="_Element097"  # link proxy (typed FeaturePython)
  LinkTransform = true
  LinkedObject = -> _Element097
  TreeRank = 344
  _LinkVersion = 1
  _Parent = -> Constraint047
FEATURE [Part::FeaturePython] _Element097  # link proxy (typed FeaturePython)
  Detach = false
  InvalidShape = false
  LinkTransform = true
  LinkedObject = -> Link054 [Edge2]
  TreeRank = 345
  ValidateShape = true
  _LinkVersion = 1
  _Parent = -> Elements001
FEATURE [App::FeaturePython] ElementLink097  label="_Element098"  # link proxy (typed FeaturePython)
  LinkTransform = true
  LinkedObject = -> _Element098
  TreeRank = 346
  _LinkVersion = 1
  _Parent = -> Constraint047
FEATURE [Part::FeaturePython] _Element098  # link proxy (typed FeaturePython)
  Detach = false
  InvalidShape = false
  LinkTransform = true
  LinkedObject = -> Link053 [Edge8]
  TreeRank = 347
  ValidateShape = true
  _LinkVersion = 1
  _Parent = -> Elements001
FEATURE [App::FeaturePython] Constraint048  label="PlaneCoincident030"  # WARN: FeaturePython — macro-defined, semantics opaque (R4)
  Angle = 0
  AnglePitch = 0
  AngleRoll = 0
  Cascade = false
  Disabled = false
  Group = -> [ElementLink098,ElementLink099]
  LockAngle = false
  Multiply = false
  OffsetX = 0
  OffsetY = 0
  TreeRank = 348
  _ConstraintType = 35
  _LinkVersion = 1
  _Parent = -> Constraints001
FEATURE [App::FeaturePython] ElementLink098  label="_Element099"  # link proxy (typed FeaturePython)
  LinkTransform = true
  LinkedObject = -> _Element099
  TreeRank = 349
  _LinkVersion = 1
  _Parent = -> Constraint048
FEATURE [Part::FeaturePython] _Element099  # link proxy (typed FeaturePython)
  Detach = false
  InvalidShape = false
  LinkTransform = true
  LinkedObject = -> Link052 [Edge27]
  TreeRank = 350
  ValidateShape = true
  _LinkVersion = 1
  _Parent = -> Elements001
FEATURE [App::FeaturePython] ElementLink099  label="_Element100"  # link proxy (typed FeaturePython)
  LinkTransform = true
  LinkedObject = -> _Element100
  TreeRank = 351
  _LinkVersion = 1
  _Parent = -> Constraint048
FEATURE [Part::FeaturePython] _Element100  # link proxy (typed FeaturePython)
  Detach = false
  InvalidShape = false
  LinkTransform = true
  LinkedObject = -> Link051 [Edge8]
  TreeRank = 352
  ValidateShape = true
  _LinkVersion = 1
  _Parent = -> Elements001
FEATURE [App::FeaturePython] Constraint049  label="PlaneCoincident031"  # WARN: FeaturePython — macro-defined, semantics opaque (R4)
  Angle = 0
  AnglePitch = 0
  AngleRoll = 0
  Cascade = false
  Disabled = false
  Group = -> [ElementLink100,ElementLink101]
  LockAngle = false
  Multiply = false
  OffsetX = 0
  OffsetY = 0
  TreeRank = 357
  _ConstraintType = 35
  _LinkVersion = 1
  _Parent = -> Constraints001
FEATURE [App::FeaturePython] ElementLink100  label="_Element101"  # link proxy (typed FeaturePython)
  LinkTransform = true
  LinkedObject = -> _Element101
  TreeRank = 358
  _LinkVersion = 1
  _Parent = -> Constraint049
FEATURE [Part::FeaturePython] _Element101  # link proxy (typed FeaturePython)
  Detach = false
  InvalidShape = false
  LinkTransform = true
  LinkedObject = -> Link055 [Edge10]
  TreeRank = 359
  ValidateShape = true
  _LinkVersion = 1
  _Parent = -> Elements001
FEATURE [App::FeaturePython] ElementLink101  label="_Element102"  # link proxy (typed FeaturePython)
  LinkTransform = true
  LinkedObject = -> _Element102
  TreeRank = 360
  _LinkVersion = 1
  _Parent = -> Constraint049
FEATURE [Part::FeaturePython] _Element102  # link proxy (typed FeaturePython)
  Detach = false
  InvalidShape = false
  LinkTransform = true
  LinkedObject = -> Link038 [Edge107]
  TreeRank = 361
  ValidateShape = true
  _LinkVersion = 1
  _Parent = -> Elements001
FEATURE [App::FeaturePython] Constraint050  label="PlaneCoincident032"  # WARN: FeaturePython — macro-defined, semantics opaque (R4)
  Angle = 0
  AnglePitch = 0
  AngleRoll = 0
  Cascade = false
  Disabled = false
  Group = -> [ElementLink102,ElementLink103]
  LockAngle = false
  Multiply = false
  OffsetX = 0
  OffsetY = 0
  TreeRank = 362
  _ConstraintType = 35
  _LinkVersion = 1
  _Parent = -> Constraints001
FEATURE [App::FeaturePython] ElementLink102  label="_Element103"  # link proxy (typed FeaturePython)
  LinkTransform = true
  LinkedObject = -> _Element103
  TreeRank = 363
  _LinkVersion = 1
  _Parent = -> Constraint050
FEATURE [Part::FeaturePython] _Element103  # link proxy (typed FeaturePython)
  Detach = false
  InvalidShape = false
  LinkTransform = true
  LinkedObject = -> Link058 [Edge9]
  TreeRank = 364
  ValidateShape = true
  _LinkVersion = 1
  _Parent = -> Elements001
FEATURE [App::FeaturePython] ElementLink103  label="_Element104"  # link proxy (typed FeaturePython)
  LinkTransform = true
  LinkedObject = -> _Element104
  TreeRank = 365
  _LinkVersion = 1
  _Parent = -> Constraint050
FEATURE [Part::FeaturePython] _Element104  # link proxy (typed FeaturePython)
  Detach = false
  InvalidShape = false
  LinkTransform = true
  LinkedObject = -> Link038 [Edge48]
  TreeRank = 366
  ValidateShape = true
  _LinkVersion = 1
  _Parent = -> Elements001
FEATURE [App::FeaturePython] Constraint051  label="PlaneCoincident033"  # WARN: FeaturePython — macro-defined, semantics opaque (R4)
  Angle = 0
  AnglePitch = 0
  AngleRoll = 0
  Cascade = false
  Disabled = false
  Group = -> [ElementLink104,ElementLink105]
  LockAngle = false
  Multiply = false
  OffsetX = 0
  OffsetY = 0
  TreeRank = 367
  _ConstraintType = 35
  _LinkVersion = 1
  _Parent = -> Constraints001
FEATURE [App::FeaturePython] ElementLink104  label="_Element105"  # link proxy (typed FeaturePython)
  LinkTransform = true
  LinkedObject = -> _Element105
  TreeRank = 368
  _LinkVersion = 1
  _Parent = -> Constraint051
FEATURE [Part::FeaturePython] _Element105  # link proxy (typed FeaturePython)
  Detach = false
  InvalidShape = false
  LinkTransform = true
  LinkedObject = -> Link056 [Edge2]
  TreeRank = 369
  ValidateShape = true
  _LinkVersion = 1
  _Parent = -> Elements001
FEATURE [App::FeaturePython] ElementLink105  label="_Element106"  # link proxy (typed FeaturePython)
  LinkTransform = true
  LinkedObject = -> _Element106
  TreeRank = 370
  _LinkVersion = 1
  _Parent = -> Constraint051
FEATURE [Part::FeaturePython] _Element106  # link proxy (typed FeaturePython)
  Detach = false
  InvalidShape = false
  LinkTransform = true
  LinkedObject = -> Link055 [Edge8]
  TreeRank = 371
  ValidateShape = true
  _LinkVersion = 1
  _Parent = -> Elements001
FEATURE [App::FeaturePython] Constraint052  label="PlaneCoincident034"  # WARN: FeaturePython — macro-defined, semantics opaque (R4)
  Angle = 0
  AnglePitch = 0
  AngleRoll = 0
  Cascade = false
  Disabled = false
  Group = -> [ElementLink106,ElementLink107]
  LockAngle = false
  Multiply = false
  OffsetX = 0
  OffsetY = 0
  TreeRank = 372
  _ConstraintType = 35
  _LinkVersion = 1
  _Parent = -> Constraints001
FEATURE [App::FeaturePython] ElementLink106  label="_Element107"  # link proxy (typed FeaturePython)
  LinkTransform = true
  LinkedObject = -> _Element107
  TreeRank = 373
  _LinkVersion = 1
  _Parent = -> Constraint052
FEATURE [Part::FeaturePython] _Element107  # link proxy (typed FeaturePython)
  Detach = false
  InvalidShape = false
  LinkTransform = true
  LinkedObject = -> Link057 [Edge25]
  TreeRank = 374
  ValidateShape = true
  _LinkVersion = 1
  _Parent = -> Elements001
FEATURE [App::FeaturePython] ElementLink107  label="_Element108"  # link proxy (typed FeaturePython)
  LinkTransform = true
  LinkedObject = -> _Element108
  TreeRank = 375
  _LinkVersion = 1
  _Parent = -> Constraint052
FEATURE [Part::FeaturePython] _Element108  # link proxy (typed FeaturePython)
  Detach = false
  InvalidShape = false
  LinkTransform = true
  LinkedObject = -> Link058 [Edge8]
  TreeRank = 376
  ValidateShape = true
  _LinkVersion = 1
  _Parent = -> Elements001
FEATURE [App::DocumentObjectGroupPython] Group006  label="Frt_Axis"  # scripted group (container) (typed FeaturePython)
  ClaimAllChildren = true
  ExportMode = 0
  Group = -> [Link051,Link052,Link053,Link054,Link055,Link056,Link057,Link058]
  TreeRank = 377
  _GroupVersion = 1
  _Parent = -> Parts001
FEATURE [App::DocumentObjectGroupPython] Group007  label="Frt Axis Cstr"  # scripted group (container) (typed FeaturePython)
  ClaimAllChildren = true
  ExportMode = 0
  Group = -> [Constraint045,Constraint046,Constraint047,Constraint048,Constraint049,Constraint050,Constraint051,Constraint052]
  TreeRank = 378
  _GroupVersion = 1
  _Parent = -> Constraints001
FEATURE [App::FeaturePython] Constraint053  label="Lenght FrtRH_Suspension"  # WARN: FeaturePython — macro-defined, semantics opaque (R4)
  Cascade = false
  Disabled = false
  Distance = 70
  Group = -> [ElementLink108,ElementLink109]
  TreeRank = 379
  _ConstraintType = 44
  _LinkVersion = 1
  _Parent = -> Constraints001
FEATURE [App::FeaturePython] ElementLink108  label="_Element109"  # link proxy (typed FeaturePython)
  LinkTransform = true
  LinkedObject = -> _Element109
  TreeRank = 380
  _LinkVersion = 1
  _Parent = -> Constraint053
FEATURE [Part::FeaturePython] _Element109  # link proxy (typed FeaturePython)
  Detach = false
  InvalidShape = false
  LinkTransform = true
  LinkedObject = -> Link033 [Edge96]
  TreeRank = 381
  ValidateShape = true
  _LinkVersion = 1
  _Parent = -> Elements001
FEATURE [App::FeaturePython] ElementLink109  label="_Element110"  # link proxy (typed FeaturePython)
  LinkTransform = true
  LinkedObject = -> _Element110
  TreeRank = 382
  _LinkVersion = 1
  _Parent = -> Constraint053
FEATURE [Part::FeaturePython] Element013  # link proxy (typed FeaturePython)
  Detach = false
  InvalidShape = false
  LinkTransform = true
  LinkedObject = -> Link010 [Edge38]
  TreeRank = 383
  ValidateShape = true
  _LinkVersion = 1
  _Parent = -> Elements
FEATURE [Part::FeaturePython] _Element110  # link proxy (typed FeaturePython)
  Detach = false
  InvalidShape = false
  LinkTransform = true
  LinkedObject = -> Assembly [1.$Element013.]
  TreeRank = 384
  ValidateShape = true
  _LinkVersion = 1
  _Parent = -> Elements001
FEATURE [Part::FeaturePython] _Element111  # link proxy (typed FeaturePython)
  Detach = false
  InvalidShape = false
  LinkTransform = true
  LinkedObject = -> Link031 [Edge96]
  TreeRank = 387
  ValidateShape = true
  _LinkVersion = 1
  _Parent = -> Elements001
FEATURE [Part::FeaturePython] Element014  # link proxy (typed FeaturePython)
  Detach = false
  InvalidShape = false
  LinkTransform = true
  LinkedObject = -> Link010 [Edge37]
  TreeRank = 389
  ValidateShape = true
  _LinkVersion = 1
  _Parent = -> Elements
FEATURE [Part::FeaturePython] _Element112  # link proxy (typed FeaturePython)
  Detach = false
  InvalidShape = false
  LinkTransform = true
  LinkedObject = -> Assembly [1.$Element014.]
  TreeRank = 390
  ValidateShape = true
  _LinkVersion = 1
  _Parent = -> Elements001
FEATURE [App::FeaturePython] Constraint054  label="Lenght FrtLH_Suspension"  # WARN: FeaturePython — macro-defined, semantics opaque (R4)
  Cascade = false
  Disabled = false
  Distance = 70
  Group = -> [ElementLink110,ElementLink111]
  TreeRank = 391
  _ConstraintType = 44
  _LinkVersion = 1
  _Parent = -> Constraints001
FEATURE [App::FeaturePython] ElementLink110  label="_Element111"  # link proxy (typed FeaturePython)
  LinkTransform = true
  LinkedObject = -> _Element111
  TreeRank = 392
  _LinkVersion = 1
  _Parent = -> Constraint054
FEATURE [App::FeaturePython] ElementLink111  label="_Element112"  # link proxy (typed FeaturePython)
  LinkTransform = true
  LinkedObject = -> _Element112
  TreeRank = 393
  _LinkVersion = 1
  _Parent = -> Constraint054
FEATURE [App::FeaturePython] Constraint055  label="Lenght RrRH_Suspension"  # WARN: FeaturePython — macro-defined, semantics opaque (R4)
  Cascade = false
  Disabled = false
  Distance = 75
  Group = -> [ElementLink112,ElementLink113]
  TreeRank = 394
  _ConstraintType = 44
  _LinkVersion = 1
  _Parent = -> Constraints001
FEATURE [App::FeaturePython] ElementLink112  label="_Element009"  # link proxy (typed FeaturePython)
  LinkTransform = true
  LinkedObject = -> _Element039
  TreeRank = 395
  _LinkVersion = 1
  _Parent = -> Constraint055
FEATURE [Part::FeaturePython] _Element113  # link proxy (typed FeaturePython)
  Detach = false
  InvalidShape = false
  LinkTransform = true
  LinkedObject = -> Link026 [Edge96]
  TreeRank = 396
  ValidateShape = true
  _LinkVersion = 1
  _Parent = -> Elements001
FEATURE [App::FeaturePython] ElementLink113  label="_Element114"  # link proxy (typed FeaturePython)
  LinkTransform = true
  LinkedObject = -> _Element114
  TreeRank = 397
  _LinkVersion = 1
  _Parent = -> Constraint055
FEATURE [Part::FeaturePython] Element015  # link proxy (typed FeaturePython)
  Detach = false
  InvalidShape = false
  LinkTransform = true
  LinkedObject = -> Link009 [Edge31]
  TreeRank = 398
  ValidateShape = true
  _LinkVersion = 1
  _Parent = -> Elements
FEATURE [Part::FeaturePython] _Element114  # link proxy (typed FeaturePython)
  Detach = false
  InvalidShape = false
  LinkTransform = true
  LinkedObject = -> Assembly [1.$Element015.]
  TreeRank = 399
  ValidateShape = true
  _LinkVersion = 1
  _Parent = -> Elements001
FEATURE [App::FeaturePython] Constraint056  label="Lenght RrLH_Suspension"  # WARN: FeaturePython — macro-defined, semantics opaque (R4)
  Cascade = false
  Disabled = false
  Distance = 75
  Group = -> [ElementLink114,ElementLink115]
  TreeRank = 400
  _ConstraintType = 44
  _LinkVersion = 1
  _Parent = -> Constraints001
FEATURE [App::FeaturePython] ElementLink114  label="_Element115"  # link proxy (typed FeaturePython)
  LinkTransform = true
  LinkedObject = -> _Element115
  TreeRank = 401
  _LinkVersion = 1
  _Parent = -> Constraint056
FEATURE [Part::FeaturePython] Element016  # link proxy (typed FeaturePython)
  Detach = false
  InvalidShape = false
  LinkTransform = true
  LinkedObject = -> Link009 [Edge34]
  TreeRank = 402
  ValidateShape = true
  _LinkVersion = 1
  _Parent = -> Elements
FEATURE [Part::FeaturePython] _Element115  # link proxy (typed FeaturePython)
  Detach = false
  InvalidShape = false
  LinkTransform = true
  LinkedObject = -> Assembly [1.$Element016.]
  TreeRank = 403
  ValidateShape = true
  _LinkVersion = 1
  _Parent = -> Elements001
FEATURE [App::FeaturePython] ElementLink115  label="_Element008"  # link proxy (typed FeaturePython)
  LinkTransform = true
  LinkedObject = -> _Element222
  TreeRank = 404
  _LinkVersion = 1
  _Parent = -> Constraint056
FEATURE [Part::FeaturePython] _Element116  # link proxy (typed FeaturePython)
  Detach = false
  InvalidShape = false
  LinkTransform = true
  LinkedObject = -> Link028 [Edge96]
  TreeRank = 405
  ValidateShape = true
  _LinkVersion = 1
  _Parent = -> Elements001
FEATURE [App::DocumentObjectGroupPython] Group008  label="Parametrized Constraints"  # scripted group (container) (typed FeaturePython)
  ClaimAllChildren = true
  ExportMode = 0
  Group = -> [Constraint053,Constraint054,Constraint055,Constraint056,Constraint029]
  TreeRank = 406
  _GroupVersion = 1
  _Parent = -> Constraints001
FEATURE [App::DocumentObjectGroupPython] Group009  label="PowerTrain"  # scripted group (container) (typed FeaturePython)
  ClaimAllChildren = true
  ExportMode = 0
  Group = -> [Link059,Link060,Link061,Link062]
  TreeRank = 411
  _GroupVersion = 1
  _Parent = -> Parts001
FEATURE [App::FeaturePython] Constraint057  label="PlaneCoincident035"  # WARN: FeaturePython — macro-defined, semantics opaque (R4)
  Angle = 0
  AnglePitch = 0
  AngleRoll = 0
  Cascade = false
  Disabled = false
  Group = -> [ElementLink116,ElementLink117]
  LockAngle = false
  Multiply = false
  OffsetX = 0
  OffsetY = 0
  TreeRank = 412
  _ConstraintType = 35
  _LinkVersion = 1
  _Parent = -> Constraints001
FEATURE [App::FeaturePython] ElementLink116  label="_Element117"  # link proxy (typed FeaturePython)
  LinkTransform = true
  LinkedObject = -> _Element117
  TreeRank = 413
  _LinkVersion = 1
  _Parent = -> Constraint057
FEATURE [Part::FeaturePython] _Element117  # link proxy (typed FeaturePython)
  Detach = false
  InvalidShape = false
  LinkTransform = true
  LinkedObject = -> Link062 [Edge52]
  TreeRank = 414
  ValidateShape = true
  _LinkVersion = 1
  _Parent = -> Elements001
FEATURE [App::FeaturePython] ElementLink117  label="_Element118"  # link proxy (typed FeaturePython)
  LinkTransform = true
  LinkedObject = -> _Element118
  TreeRank = 415
  _LinkVersion = 1
  _Parent = -> Constraint057
FEATURE [Part::FeaturePython] Element017  # link proxy (typed FeaturePython)
  Detach = false
  InvalidShape = false
  LinkTransform = true
  LinkedObject = -> Link016 [Edge53]
  TreeRank = 416
  ValidateShape = true
  _LinkVersion = 1
  _Parent = -> Elements
FEATURE [Part::FeaturePython] _Element118  # link proxy (typed FeaturePython)
  Detach = false
  InvalidShape = false
  LinkTransform = true
  LinkedObject = -> Assembly [1.$Element017.]
  TreeRank = 417
  ValidateShape = true
  _LinkVersion = 1
  _Parent = -> Elements001
FEATURE [App::FeaturePython] Constraint058  label="AttachmentOffset011"  # WARN: FeaturePython — macro-defined, semantics opaque (R4)
  Cascade = false
  Disabled = false
  Group = -> [ElementLink118,ElementLink119]
  Multiply = false
  TreeRank = 418
  _ConstraintType = 0
  _LinkVersion = 1
  _Parent = -> Constraints001
FEATURE [App::FeaturePython] ElementLink118  label="_Element119"  # link proxy (typed FeaturePython)
  LinkTransform = true
  LinkedObject = -> _Element119
  TreeRank = 419
  _LinkVersion = 1
  _Parent = -> Constraint058
FEATURE [Part::FeaturePython] _Element119  # link proxy (typed FeaturePython)
  Detach = false
  InvalidShape = false
  LinkTransform = true
  LinkedObject = -> Link059 [Face54]
  TreeRank = 420
  ValidateShape = true
  _LinkVersion = 1
  _Parent = -> Elements001
FEATURE [App::FeaturePython] ElementLink119  label="_Element120"  # link proxy (typed FeaturePython)
  LinkTransform = true
  LinkedObject = -> _Element120
  Offset = pos=(-5.258e-13,1.1369e-12,-6) rot=(0,0,-1;4.17134rad)
  Placement = pos=(-183.843,-6,-131.142) rot=(0,1,0;2.11185rad)
  TreeRank = 421
  _LinkVersion = 1
  _OffsetAdded = true
  _Parent = -> Constraint058
FEATURE [Part::FeaturePython] _Element120  # link proxy (typed FeaturePython)
  Detach = false
  InvalidShape = false
  LinkTransform = true
  LinkedObject = -> Link062 [Face8]
  TreeRank = 422
  ValidateShape = true
  _LinkVersion = 1
  _Parent = -> Elements001
FEATURE [App::FeaturePython] Constraint059  label="AttachmentOffset012"  # WARN: FeaturePython — macro-defined, semantics opaque (R4)
  Cascade = false
  Disabled = false
  Group = -> [ElementLink120,ElementLink121]
  Multiply = false
  TreeRank = 423
  _ConstraintType = 0
  _LinkVersion = 1
  _Parent = -> Constraints001
FEATURE [App::FeaturePython] ElementLink120  label="_Element121"  # link proxy (typed FeaturePython)
  LinkTransform = true
  LinkedObject = -> _Element121
  TreeRank = 424
  _LinkVersion = 1
  _Parent = -> Constraint059
FEATURE [Part::FeaturePython] Element018  # link proxy (typed FeaturePython)
  Detach = false
  InvalidShape = false
  LinkTransform = true
  LinkedObject = -> Link020 [Face3]
  TreeRank = 425
  ValidateShape = true
  _LinkVersion = 1
  _Parent = -> Elements
FEATURE [Part::FeaturePython] _Element121  # link proxy (typed FeaturePython)
  Detach = false
  InvalidShape = false
  LinkTransform = true
  LinkedObject = -> Assembly [1.$Element018.]
  TreeRank = 426
  ValidateShape = true
  _LinkVersion = 1
  _Parent = -> Elements001
FEATURE [App::FeaturePython] ElementLink121  label="_Element119"  # link proxy (typed FeaturePython)
  LinkTransform = true
  LinkedObject = -> _Element119
  Offset = pos=(2.7e-13,4.62e-14,-38.25) rot=(-0.052336,-0.99863,0;3.14159rad)
  Placement = pos=(-255.915,1.02709,13.4119) rot=(0.052336,0,0.99863;3.14159rad)
  TreeRank = 427
  _LinkVersion = 1
  _OffsetAdded = true
  _Parent = -> Constraint059
FEATURE [App::FeaturePython] Constraint060  label="AttachmentOffset013"  # WARN: FeaturePython — macro-defined, semantics opaque (R4)
  Cascade = false
  Disabled = false
  Group = -> [ElementLink122,ElementLink123]
  Multiply = false
  TreeRank = 428
  _ConstraintType = 0
  _LinkVersion = 1
  _Parent = -> Constraints
FEATURE [App::FeaturePython] ElementLink122  label="_Element122"  # link proxy (typed FeaturePython)
  LinkTransform = true
  LinkedObject = -> _Element122
  TreeRank = 429
  _LinkVersion = 1
  _Parent = -> Constraint060
FEATURE [Part::FeaturePython] _Element122  # link proxy (typed FeaturePython)
  Detach = false
  InvalidShape = false
  LinkTransform = true
  LinkedObject = -> Link022 [Face3]
  TreeRank = 430
  ValidateShape = true
  _LinkVersion = 1
  _Parent = -> Elements
FEATURE [App::FeaturePython] ElementLink123  label="_Element123"  # link proxy (typed FeaturePython)
  LinkTransform = true
  LinkedObject = -> _Element123
  Offset = pos=(0,7.45,2.84e-14) rot=(0.707107,-0.707107,0;3.14159rad)
  Placement = pos=(-103.584,60.2771,-96.1339) rot=(-0.707107,0,0.707107;3.14159rad)
  TreeRank = 431
  _LinkVersion = 1
  _OffsetAdded = true
  _Parent = -> Constraint060
FEATURE [Part::FeaturePython] _Element123  # link proxy (typed FeaturePython)
  Detach = false
  InvalidShape = false
  LinkTransform = true
  LinkedObject = -> Link005 [Face24]
  TreeRank = 432
  ValidateShape = true
  _LinkVersion = 1
  _Parent = -> Elements
FEATURE [App::FeaturePython] Constraint061  label="AttachmentOffset014"  # WARN: FeaturePython — macro-defined, semantics opaque (R4)
  Cascade = false
  Disabled = false
  Group = -> [ElementLink124,ElementLink125]
  Multiply = false
  TreeRank = 433
  _ConstraintType = 0
  _LinkVersion = 1
  _Parent = -> Constraints
FEATURE [App::FeaturePython] ElementLink124  label="_Element124"  # link proxy (typed FeaturePython)
  LinkTransform = true
  LinkedObject = -> _Element124
  TreeRank = 434
  _LinkVersion = 1
  _Parent = -> Constraint061
FEATURE [Part::FeaturePython] _Element124  # link proxy (typed FeaturePython)
  Detach = false
  InvalidShape = false
  LinkTransform = true
  LinkedObject = -> Link021 [Face4]
  TreeRank = 435
  ValidateShape = true
  _LinkVersion = 1
  _Parent = -> Elements
FEATURE [App::FeaturePython] ElementLink125  label="_Element125"  # link proxy (typed FeaturePython)
  LinkTransform = true
  LinkedObject = -> _Element125
  Offset = pos=(-1.78e-14,-0.3,5) rot=(0.707107,0.707107,0;3.14159rad)
  Placement = pos=(-103.584,-32.7229,-103.884) rot=(-0.707107,0,0.707107;3.14159rad)
  TreeRank = 436
  _LinkVersion = 1
  _OffsetAdded = true
  _Parent = -> Constraint061
FEATURE [Part::FeaturePython] _Element125  # link proxy (typed FeaturePython)
  Detach = false
  InvalidShape = false
  LinkTransform = true
  LinkedObject = -> Link005 [Face31]
  TreeRank = 437
  ValidateShape = true
  _LinkVersion = 1
  _Parent = -> Elements
FEATURE [App::FeaturePython] Constraint062  label="AttachmentOffset015"  # WARN: FeaturePython — macro-defined, semantics opaque (R4)
  Cascade = false
  Disabled = false
  Group = -> [ElementLink126,ElementLink127]
  Multiply = false
  TreeRank = 438
  _ConstraintType = 0
  _LinkVersion = 1
  _Parent = -> Constraints001
FEATURE [App::FeaturePython] ElementLink126  label="_Element126"  # link proxy (typed FeaturePython)
  LinkTransform = true
  LinkedObject = -> _Element126
  TreeRank = 439
  _LinkVersion = 1
  _Parent = -> Constraint062
FEATURE [Part::FeaturePython] _Element126  # link proxy (typed FeaturePython)
  Detach = false
  InvalidShape = false
  LinkTransform = true
  LinkedObject = -> Link061 [Face2]
  TreeRank = 440
  ValidateShape = true
  _LinkVersion = 1
  _Parent = -> Elements001
FEATURE [App::FeaturePython] ElementLink127  label="_Element127"  # link proxy (typed FeaturePython)
  LinkTransform = true
  LinkedObject = -> _Element127
  Offset = pos=(2.13e-14,8.1e-13,-21.2) rot=(-0.993572,-0.113203,0;3.14159rad)
  Placement = pos=(-174.681,39.0771,19.9024) rot=(0.113203,0,0.993572;3.14159rad)
  TreeRank = 441
  _LinkVersion = 1
  _OffsetAdded = true
  _Parent = -> Constraint062
FEATURE [Part::FeaturePython] Element019  # link proxy (typed FeaturePython)
  Detach = false
  InvalidShape = false
  LinkTransform = true
  LinkedObject = -> Link022 [Face2]
  TreeRank = 442
  ValidateShape = true
  _LinkVersion = 1
  _Parent = -> Elements
FEATURE [Part::FeaturePython] _Element127  # link proxy (typed FeaturePython)
  Detach = false
  InvalidShape = false
  LinkTransform = true
  LinkedObject = -> Assembly [1.$Element019.]
  TreeRank = 443
  ValidateShape = true
  _LinkVersion = 1
  _Parent = -> Elements001
FEATURE [App::FeaturePython] Constraint063  label="AttachmentOffset016"  # WARN: FeaturePython — macro-defined, semantics opaque (R4)
  Cascade = false
  Disabled = false
  Group = -> [ElementLink128,ElementLink129]
  Multiply = false
  TreeRank = 444
  _ConstraintType = 0
  _LinkVersion = 1
  _Parent = -> Constraints001
FEATURE [App::FeaturePython] ElementLink128  label="_Element128"  # link proxy (typed FeaturePython)
  LinkTransform = true
  LinkedObject = -> _Element128
  TreeRank = 445
  _LinkVersion = 1
  _Parent = -> Constraint063
FEATURE [Part::FeaturePython] _Element128  # link proxy (typed FeaturePython)
  Detach = false
  InvalidShape = false
  LinkTransform = true
  LinkedObject = -> Link060 [Face52]
  TreeRank = 446
  ValidateShape = true
  _LinkVersion = 1
  _Parent = -> Elements001
FEATURE [App::FeaturePython] ElementLink129  label="_Element129"  # link proxy (typed FeaturePython)
  LinkTransform = true
  LinkedObject = -> _Element129
  Offset = pos=(1.009e-12,-9.06e-14,24.2) rot=(0,0,1;1.3439rad)
  Placement = pos=(-82.9862,-24.2,77.1998) rot=(0,-1,0;1.3439rad)
  TreeRank = 447
  _LinkVersion = 1
  _OffsetAdded = true
  _Parent = -> Constraint063
FEATURE [Part::FeaturePython] _Element129  # link proxy (typed FeaturePython)
  Detach = false
  InvalidShape = false
  LinkTransform = true
  LinkedObject = -> Assembly [1.$_Element122.]
  TreeRank = 448
  ValidateShape = true
  _LinkVersion = 1
  _Parent = -> Elements001
FEATURE [App::DocumentObjectGroupPython] Group010  label="powerTrainCstr"  # scripted group (container) (typed FeaturePython)
  ClaimAllChildren = true
  ExportMode = 0
  Group = -> [Constraint063,Constraint057,Constraint058,Constraint059,Constraint062]
  TreeRank = 451
  _GroupVersion = 1
  _Parent = -> Constraints001
FEATURE [Part::FeaturePython] _Element130  # WARN: FeaturePython — macro-defined, semantics opaque (R4)
  Detach = false
  InvalidShape = false
  LinkTransform = true
  TreeRank = 454
  ValidateShape = true
  _LinkVersion = 1
  _Parent = -> Elements001
FEATURE [Part::FeaturePython] Element020  # link proxy (typed FeaturePython)
  Detach = false
  InvalidShape = false
  LinkTransform = true
  LinkedObject = -> Link021 [Edge10]
  TreeRank = 456
  ValidateShape = true
  _LinkVersion = 1
  _Parent = -> Elements
FEATURE [Part::FeaturePython] _Element131  # link proxy (typed FeaturePython)
  Detach = false
  InvalidShape = false
  LinkTransform = true
  LinkedObject = -> Assembly [1.$Element020.]
  TreeRank = 457
  ValidateShape = true
  _LinkVersion = 1
  _Parent = -> Elements001
FEATURE [App::FeaturePython] Constraint065  label="Attachment"  # WARN: FeaturePython — macro-defined, semantics opaque (R4)
  Cascade = false
  Disabled = false
  Group = -> [ElementLink132,ElementLink133]
  Multiply = false
  TreeRank = 460
  _ConstraintType = 45
  _LinkVersion = 1
  _Parent = -> Constraints001
FEATURE [App::FeaturePython] ElementLink132  label="_Element132"  # link proxy (typed FeaturePython)
  LinkTransform = true
  LinkedObject = -> _Element132
  TreeRank = 461
  _LinkVersion = 1
  _Parent = -> Constraint065
FEATURE [Part::FeaturePython] _Element132  # link proxy (typed FeaturePython)
  Detach = false
  InvalidShape = false
  LinkTransform = true
  LinkedObject = -> Link066 [Edge8]
  TreeRank = 462
  ValidateShape = true
  _LinkVersion = 1
  _Parent = -> Elements001
FEATURE [App::FeaturePython] ElementLink133  label="_Element133"  # link proxy (typed FeaturePython)
  LinkTransform = true
  LinkedObject = -> _Element133
  TreeRank = 463
  _LinkVersion = 1
  _Parent = -> Constraint065
FEATURE [Part::FeaturePython] _Element133  # link proxy (typed FeaturePython)
  Detach = false
  InvalidShape = false
  LinkTransform = true
  LinkedObject = -> Link037 [Edge159]
  TreeRank = 464
  ValidateShape = true
  _LinkVersion = 1
  _Parent = -> Elements001
FEATURE [App::FeaturePython] Constraint066  label="Attachment001"  # WARN: FeaturePython — macro-defined, semantics opaque (R4)
  Cascade = false
  Disabled = false
  Group = -> [ElementLink134,ElementLink135]
  Multiply = false
  TreeRank = 466
  _ConstraintType = 45
  _LinkVersion = 1
  _Parent = -> Constraints001
FEATURE [App::FeaturePython] ElementLink134  label="_Element134"  # link proxy (typed FeaturePython)
  LinkTransform = true
  LinkedObject = -> _Element134
  TreeRank = 467
  _LinkVersion = 1
  _Parent = -> Constraint066
FEATURE [Part::FeaturePython] _Element134  # link proxy (typed FeaturePython)
  Detach = false
  InvalidShape = false
  LinkTransform = true
  LinkedObject = -> Link065 [Edge10]
  TreeRank = 468
  ValidateShape = true
  _LinkVersion = 1
  _Parent = -> Elements001
FEATURE [App::FeaturePython] ElementLink135  label="_Element135"  # link proxy (typed FeaturePython)
  LinkTransform = true
  LinkedObject = -> _Element135
  TreeRank = 469
  _LinkVersion = 1
  _Parent = -> Constraint066
FEATURE [Part::FeaturePython] _Element135  # link proxy (typed FeaturePython)
  Detach = false
  InvalidShape = false
  LinkTransform = true
  LinkedObject = -> Link037 [Edge3]
  TreeRank = 470
  ValidateShape = true
  _LinkVersion = 1
  _Parent = -> Elements001
FEATURE [App::FeaturePython] Constraint067  label="Attachment002"  # WARN: FeaturePython — macro-defined, semantics opaque (R4)
  Cascade = false
  Disabled = false
  Group = -> [ElementLink136,ElementLink137]
  Multiply = false
  TreeRank = 471
  _ConstraintType = 45
  _LinkVersion = 1
  _Parent = -> Constraints001
FEATURE [App::FeaturePython] ElementLink136  label="_Element136"  # link proxy (typed FeaturePython)
  LinkTransform = true
  LinkedObject = -> _Element136
  TreeRank = 472
  _LinkVersion = 1
  _Parent = -> Constraint067
FEATURE [Part::FeaturePython] _Element136  # link proxy (typed FeaturePython)
  Detach = false
  InvalidShape = false
  LinkTransform = true
  LinkedObject = -> Link067 [Edge25]
  TreeRank = 473
  ValidateShape = true
  _LinkVersion = 1
  _Parent = -> Elements001
FEATURE [App::FeaturePython] ElementLink137  label="_Element137"  # link proxy (typed FeaturePython)
  LinkTransform = true
  LinkedObject = -> _Element137
  TreeRank = 474
  _LinkVersion = 1
  _Parent = -> Constraint067
FEATURE [Part::FeaturePython] _Element137  # link proxy (typed FeaturePython)
  Detach = false
  InvalidShape = false
  LinkTransform = true
  LinkedObject = -> Link066 [Edge10]
  TreeRank = 475
  ValidateShape = true
  _LinkVersion = 1
  _Parent = -> Elements001
FEATURE [Part::FeaturePython] _Element138  # WARN: FeaturePython — macro-defined, semantics opaque (R4)
  Detach = false
  InvalidShape = false
  LinkTransform = true
  TreeRank = 478
  ValidateShape = true
  _LinkVersion = 1
  _Parent = -> Elements001
FEATURE [Part::FeaturePython] _Element139  # link proxy (typed FeaturePython)
  Detach = false
  InvalidShape = false
  LinkTransform = true
  LinkedObject = -> Link066 [Face2]
  TreeRank = 480
  ValidateShape = true
  _LinkVersion = 1
  _Parent = -> Elements001
FEATURE [Part::FeaturePython] Element021  # link proxy (typed FeaturePython)
  Detach = false
  InvalidShape = false
  LinkTransform = true
  LinkedObject = -> Link021 [Face2]
  TreeRank = 483
  ValidateShape = true
  _LinkVersion = 1
  _Parent = -> Elements
FEATURE [Part::FeaturePython] _Element140  # link proxy (typed FeaturePython)
  Detach = false
  InvalidShape = false
  LinkTransform = true
  LinkedObject = -> Assembly [1.$Element021.]
  TreeRank = 484
  ValidateShape = true
  _LinkVersion = 1
  _Parent = -> Elements001
FEATURE [Part::FeaturePython] _Element141  # WARN: FeaturePython — macro-defined, semantics opaque (R4)
  Detach = false
  InvalidShape = false
  LinkTransform = true
  TreeRank = 486
  ValidateShape = true
  _LinkVersion = 1
  _Parent = -> Elements001
FEATURE [App::FeaturePython] Constraint068  label="PlaneCoincident036"  # WARN: FeaturePython — macro-defined, semantics opaque (R4)
  Angle = 0
  AnglePitch = 0
  AngleRoll = 0
  Cascade = false
  Disabled = false
  Group = -> [ElementLink138,ElementLink139]
  LockAngle = false
  Multiply = false
  OffsetX = 0
  OffsetY = 0
  TreeRank = 494
  _ConstraintType = 35
  _LinkVersion = 1
  _Parent = -> Constraints001
FEATURE [App::FeaturePython] ElementLink138  label="_Element142"  # link proxy (typed FeaturePython)
  LinkTransform = true
  LinkedObject = -> _Element142
  TreeRank = 495
  _LinkVersion = 1
  _Parent = -> Constraint068
FEATURE [Part::FeaturePython] _Element142  # link proxy (typed FeaturePython)
  Detach = false
  InvalidShape = false
  LinkTransform = true
  LinkedObject = -> Link070 [0.Edge54]
  TreeRank = 496
  ValidateShape = true
  _LinkVersion = 1
  _Parent = -> Elements001
FEATURE [App::FeaturePython] ElementLink139  label="_Element131"  # link proxy (typed FeaturePython)
  LinkTransform = true
  LinkedObject = -> _Element131
  TreeRank = 497
  _LinkVersion = 1
  _Parent = -> Constraint068
FEATURE [App::FeaturePython] Constraint069  label="PointsCoincident005"  # WARN: FeaturePython — macro-defined, semantics opaque (R4)
  Disabled = false
  Group = -> [ElementLink140,ElementLink141]
  TreeRank = 498
  _ConstraintType = 1
  _LinkVersion = 1
  _Parent = -> Constraints001
FEATURE [App::FeaturePython] ElementLink140  label="_Element143"  # link proxy (typed FeaturePython)
  LinkTransform = true
  LinkedObject = -> _Element143
  TreeRank = 499
  _LinkVersion = 1
  _Parent = -> Constraint069
FEATURE [Part::FeaturePython] _Element143  # link proxy (typed FeaturePython)
  Detach = false
  InvalidShape = false
  LinkTransform = true
  LinkedObject = -> Link068 [0.Face2]
  TreeRank = 500
  ValidateShape = true
  _LinkVersion = 1
  _Parent = -> Elements001
FEATURE [App::FeaturePython] ElementLink141  label="_Element001"  # link proxy (typed FeaturePython)
  LinkTransform = true
  LinkedObject = -> _Element145
  TreeRank = 501
  _LinkVersion = 1
  _Parent = -> Constraint069
FEATURE [Part::FeaturePython] _Element144  # link proxy (typed FeaturePython)
  Detach = false
  InvalidShape = false
  LinkTransform = true
  LinkedObject = -> Link070 [0.Face38]
  TreeRank = 502
  ValidateShape = true
  _LinkVersion = 1
  _Parent = -> Elements001
FEATURE [Part::FeaturePython] _Element145  label="_Element001"  # link proxy (typed FeaturePython)
  Detach = false
  InvalidShape = false
  LinkTransform = true
  LinkedObject = -> Link070 [Link002.Face1]
  TreeRank = 503
  ValidateShape = true
  _LinkVersion = 1
  _Parent = -> Elements001
FEATURE [App::FeaturePython] Constraint070  label="PointsCoincident006"  # WARN: FeaturePython — macro-defined, semantics opaque (R4)
  Disabled = false
  Group = -> [ElementLink142,ElementLink143]
  TreeRank = 504
  _ConstraintType = 1
  _LinkVersion = 1
  _Parent = -> Constraints001
FEATURE [App::FeaturePython] ElementLink142  label="_Element146"  # link proxy (typed FeaturePython)
  LinkTransform = true
  LinkedObject = -> _Element146
  TreeRank = 505
  _LinkVersion = 1
  _Parent = -> Constraint070
FEATURE [Part::FeaturePython] _Element146  # link proxy (typed FeaturePython)
  Detach = false
  InvalidShape = false
  LinkTransform = true
  LinkedObject = -> Link072 [0.Face2]
  TreeRank = 506
  ValidateShape = true
  _LinkVersion = 1
  _Parent = -> Elements001
FEATURE [App::FeaturePython] ElementLink143  label="_Element143"  # link proxy (typed FeaturePython)
  LinkTransform = true
  LinkedObject = -> _Element143
  TreeRank = 507
  _LinkVersion = 1
  _Parent = -> Constraint070
FEATURE [App::FeaturePython] Constraint071  label="AxialAlignment"  # WARN: FeaturePython — macro-defined, semantics opaque (R4)
  Angle = 0
  AnglePitch = 0
  AngleRoll = 0
  Disabled = false
  Group = -> [ElementLink144,ElementLink145]
  LockAngle = false
  Multiply = false
  TreeRank = 508
  _ConstraintType = 36
  _LinkVersion = 1
  _Parent = -> Constraints001
FEATURE [App::FeaturePython] ElementLink144  label="_Element147"  # link proxy (typed FeaturePython)
  LinkTransform = true
  LinkedObject = -> _Element147
  TreeRank = 509
  _LinkVersion = 1
  _Parent = -> Constraint071
FEATURE [Part::FeaturePython] _Element147  # link proxy (typed FeaturePython)
  Detach = false
  InvalidShape = false
  LinkTransform = true
  LinkedObject = -> Link072 [0.Face21]
  TreeRank = 510
  ValidateShape = true
  _LinkVersion = 1
  _Parent = -> Elements001
FEATURE [App::FeaturePython] ElementLink145  label="_Element148"  # link proxy (typed FeaturePython)
  LinkTransform = true
  LinkedObject = -> _Element148
  TreeRank = 511
  _LinkVersion = 1
  _Parent = -> Constraint071
FEATURE [Part::FeaturePython] _Element148  # link proxy (typed FeaturePython)
  Detach = false
  InvalidShape = false
  LinkTransform = true
  LinkedObject = -> Link073 [0.Face96]
  TreeRank = 512
  ValidateShape = true
  _LinkVersion = 1
  _Parent = -> Elements001
FEATURE [App::FeaturePython] Constraint072  label="AxialAlignment001"  # WARN: FeaturePython — macro-defined, semantics opaque (R4)
  Angle = 0
  AnglePitch = 0
  AngleRoll = 0
  Disabled = false
  Group = -> [ElementLink146,ElementLink147]
  LockAngle = false
  Multiply = false
  TreeRank = 513
  _ConstraintType = 36
  _LinkVersion = 1
  _Parent = -> Constraints001
FEATURE [App::FeaturePython] ElementLink146  label="_Element149"  # link proxy (typed FeaturePython)
  LinkTransform = true
  LinkedObject = -> _Element149
  TreeRank = 514
  _LinkVersion = 1
  _Parent = -> Constraint072
FEATURE [Part::FeaturePython] _Element149  # link proxy (typed FeaturePython)
  Detach = false
  InvalidShape = false
  LinkTransform = true
  LinkedObject = -> Link073 [0.Face27]
  TreeRank = 515
  ValidateShape = true
  _LinkVersion = 1
  _Parent = -> Elements001
FEATURE [App::FeaturePython] ElementLink147  label="_Element150"  # link proxy (typed FeaturePython)
  LinkTransform = true
  LinkedObject = -> _Element150
  TreeRank = 516
  _LinkVersion = 1
  _Parent = -> Constraint072
FEATURE [Part::FeaturePython] _Element150  # link proxy (typed FeaturePython)
  Detach = false
  InvalidShape = false
  LinkTransform = true
  LinkedObject = -> Link071 [0.Face21]
  TreeRank = 517
  ValidateShape = true
  _LinkVersion = 1
  _Parent = -> Elements001
FEATURE [App::FeaturePython] Constraint073  label="PointInPlane"  # WARN: FeaturePython — macro-defined, semantics opaque (R4)
  Disabled = false
  Group = -> [ElementLink148,ElementLink149]
  TreeRank = 518
  _ConstraintType = 3
  _LinkVersion = 1
  _Parent = -> Constraints001
FEATURE [App::FeaturePython] ElementLink148  label="_Element151"  # link proxy (typed FeaturePython)
  LinkTransform = true
  LinkedObject = -> _Element151
  TreeRank = 519
  _LinkVersion = 1
  _Parent = -> Constraint073
FEATURE [Part::FeaturePython] _Element151  # link proxy (typed FeaturePython)
  Detach = false
  InvalidShape = false
  LinkTransform = true
  LinkedObject = -> Link071 [0.Vertex42]
  TreeRank = 520
  ValidateShape = true
  _LinkVersion = 1
  _Parent = -> Elements001
FEATURE [App::FeaturePython] ElementLink149  label="_Element152"  # link proxy (typed FeaturePython)
  LinkTransform = true
  LinkedObject = -> _Element152
  TreeRank = 521
  _LinkVersion = 1
  _Parent = -> Constraint073
FEATURE [Part::FeaturePython] _Element152  # link proxy (typed FeaturePython)
  Detach = false
  InvalidShape = false
  LinkTransform = true
  LinkedObject = -> Link073 [0.Face4]
  TreeRank = 522
  ValidateShape = true
  _LinkVersion = 1
  _Parent = -> Elements001
FEATURE [App::FeaturePython] Constraint074  label="PointsCoincident007"  # WARN: FeaturePython — macro-defined, semantics opaque (R4)
  Disabled = false
  Group = -> [ElementLink150,ElementLink151]
  TreeRank = 523
  _ConstraintType = 1
  _LinkVersion = 1
  _Parent = -> Constraints001
FEATURE [App::FeaturePython] ElementLink150  label="_Element153"  # link proxy (typed FeaturePython)
  LinkTransform = true
  LinkedObject = -> _Element153
  TreeRank = 524
  _LinkVersion = 1
  _Parent = -> Constraint074
FEATURE [Part::FeaturePython] _Element153  # link proxy (typed FeaturePython)
  Detach = false
  InvalidShape = false
  LinkTransform = true
  LinkedObject = -> Link074 [0.Face2]
  TreeRank = 525
  ValidateShape = true
  _LinkVersion = 1
  _Parent = -> Elements001
FEATURE [App::FeaturePython] ElementLink151  label="_Element154"  # link proxy (typed FeaturePython)
  LinkTransform = true
  LinkedObject = -> _Element154
  TreeRank = 526
  _LinkVersion = 1
  _Parent = -> Constraint074
FEATURE [Part::FeaturePython] _Element154  # link proxy (typed FeaturePython)
  Detach = false
  InvalidShape = false
  LinkTransform = true
  LinkedObject = -> Link071 [0.Face3]
  TreeRank = 527
  ValidateShape = true
  _LinkVersion = 1
  _Parent = -> Elements001
FEATURE [App::FeaturePython] Constraint075  label="PointsCoincident008"  # WARN: FeaturePython — macro-defined, semantics opaque (R4)
  Disabled = false
  Group = -> [ElementLink152,ElementLink153]
  TreeRank = 528
  _ConstraintType = 1
  _LinkVersion = 1
  _Parent = -> Constraints001
FEATURE [App::FeaturePython] ElementLink152  label="_Element155"  # link proxy (typed FeaturePython)
  LinkTransform = true
  LinkedObject = -> _Element155
  TreeRank = 529
  _LinkVersion = 1
  _Parent = -> Constraint075
FEATURE [Part::FeaturePython] _Element155  # link proxy (typed FeaturePython)
  Detach = false
  InvalidShape = false
  LinkTransform = true
  LinkedObject = -> Link069 [0.Face1]
  TreeRank = 530
  ValidateShape = true
  _LinkVersion = 1
  _Parent = -> Elements001
FEATURE [App::FeaturePython] ElementLink153  label="_Element153"  # link proxy (typed FeaturePython)
  LinkTransform = true
  LinkedObject = -> _Element153
  TreeRank = 531
  _LinkVersion = 1
  _Parent = -> Constraint075
FEATURE [App::FeaturePython] Constraint076  label="Attachment003"  # WARN: FeaturePython — macro-defined, semantics opaque (R4)
  Cascade = false
  Disabled = false
  Group = -> [ElementLink154,ElementLink155]
  Multiply = false
  TreeRank = 532
  _ConstraintType = 45
  _LinkVersion = 1
  _Parent = -> Constraints001
FEATURE [App::FeaturePython] ElementLink154  label="_Element156"  # link proxy (typed FeaturePython)
  LinkTransform = true
  LinkedObject = -> _Element156
  TreeRank = 533
  _LinkVersion = 1
  _Parent = -> Constraint076
FEATURE [Part::FeaturePython] _Element156  # link proxy (typed FeaturePython)
  Detach = false
  InvalidShape = false
  LinkTransform = true
  LinkedObject = -> Link069 [0.Edge50]
  TreeRank = 534
  ValidateShape = true
  _LinkVersion = 1
  _Parent = -> Elements001
FEATURE [App::FeaturePython] ElementLink155  label="_Element157"  # link proxy (typed FeaturePython)
  LinkTransform = true
  LinkedObject = -> _Element157
  TreeRank = 535
  _LinkVersion = 1
  _Parent = -> Constraint076
FEATURE [Part::FeaturePython] _Element157  # link proxy (typed FeaturePython)
  Detach = false
  InvalidShape = false
  LinkTransform = true
  LinkedObject = -> Link065 [Edge8]
  TreeRank = 536
  ValidateShape = true
  _LinkVersion = 1
  _Parent = -> Elements001
FEATURE [App::FeaturePython] Constraint077  label="PlaneCoincident037"  # WARN: FeaturePython — macro-defined, semantics opaque (R4)
  Angle = 0
  AnglePitch = 0
  AngleRoll = 0
  Cascade = false
  Disabled = false
  Group = -> [ElementLink156,ElementLink157]
  LockAngle = false
  Multiply = false
  OffsetX = 0
  OffsetY = 0
  TreeRank = 537
  _ConstraintType = 35
  _LinkVersion = 1
  _Parent = -> Constraints001
FEATURE [App::FeaturePython] ElementLink156  label="_Element158"  # link proxy (typed FeaturePython)
  LinkTransform = true
  LinkedObject = -> _Element158
  TreeRank = 538
  _LinkVersion = 1
  _Parent = -> Constraint077
FEATURE [Part::FeaturePython] _Element158  # link proxy (typed FeaturePython)
  Detach = false
  InvalidShape = false
  LinkTransform = true
  LinkedObject = -> Link069 [1.Edge50]
  TreeRank = 539
  ValidateShape = true
  _LinkVersion = 1
  _Parent = -> Elements001
FEATURE [App::FeaturePython] ElementLink157  label="_Element159"  # link proxy (typed FeaturePython)
  LinkTransform = true
  LinkedObject = -> _Element159
  TreeRank = 540
  _LinkVersion = 1
  _Parent = -> Constraint077
FEATURE [Part::FeaturePython] Element022  # link proxy (typed FeaturePython)
  Detach = false
  InvalidShape = false
  LinkTransform = true
  LinkedObject = -> Link022 [Edge10]
  TreeRank = 541
  ValidateShape = true
  _LinkVersion = 1
  _Parent = -> Elements
FEATURE [Part::FeaturePython] _Element159  # link proxy (typed FeaturePython)
  Detach = false
  InvalidShape = false
  LinkTransform = true
  LinkedObject = -> Assembly [1.$Element022.]
  TreeRank = 542
  ValidateShape = true
  _LinkVersion = 1
  _Parent = -> Elements001
FEATURE [App::FeaturePython] Constraint078  label="Attachment004"  # WARN: FeaturePython — macro-defined, semantics opaque (R4)
  Cascade = false
  Disabled = false
  Group = -> [ElementLink158,ElementLink159]
  Multiply = false
  TreeRank = 545
  _ConstraintType = 45
  _LinkVersion = 1
  _Parent = -> Constraints001
FEATURE [App::FeaturePython] ElementLink158  label="_Element160"  # link proxy (typed FeaturePython)
  LinkTransform = true
  LinkedObject = -> _Element160
  TreeRank = 546
  _LinkVersion = 1
  _Parent = -> Constraint078
FEATURE [Part::FeaturePython] _Element160  # link proxy (typed FeaturePython)
  Detach = false
  InvalidShape = false
  LinkTransform = true
  LinkedObject = -> Link076 [Edge8]
  TreeRank = 547
  ValidateShape = true
  _LinkVersion = 1
  _Parent = -> Elements001
FEATURE [App::FeaturePython] ElementLink159  label="_Element002"  # link proxy (typed FeaturePython)
  LinkTransform = true
  LinkedObject = -> _Element164
  TreeRank = 548
  _LinkVersion = 1
  _Parent = -> Constraint078
FEATURE [Part::FeaturePython] _Element161  # link proxy (typed FeaturePython)
  Detach = false
  InvalidShape = false
  LinkTransform = true
  LinkedObject = -> Link029 [Edge207]
  TreeRank = 549
  ValidateShape = true
  _LinkVersion = 1
  _Parent = -> Elements001
FEATURE [App::FeaturePython] Constraint079  label="Attachment005"  # WARN: FeaturePython — macro-defined, semantics opaque (R4)
  Cascade = false
  Disabled = false
  Group = -> [ElementLink160,ElementLink161]
  Multiply = false
  TreeRank = 550
  _ConstraintType = 45
  _LinkVersion = 1
  _Parent = -> Constraints001
FEATURE [App::FeaturePython] ElementLink160  label="_Element162"  # link proxy (typed FeaturePython)
  LinkTransform = true
  LinkedObject = -> _Element162
  TreeRank = 551
  _LinkVersion = 1
  _Parent = -> Constraint079
FEATURE [Part::FeaturePython] _Element162  # link proxy (typed FeaturePython)
  Detach = false
  InvalidShape = false
  LinkTransform = true
  LinkedObject = -> Link075 [Edge8]
  TreeRank = 552
  ValidateShape = true
  _LinkVersion = 1
  _Parent = -> Elements001
FEATURE [App::FeaturePython] ElementLink161  label="_Element163"  # link proxy (typed FeaturePython)
  LinkTransform = true
  LinkedObject = -> _Element163
  TreeRank = 553
  _LinkVersion = 1
  _Parent = -> Constraint079
FEATURE [Part::FeaturePython] _Element163  # link proxy (typed FeaturePython)
  Detach = false
  InvalidShape = false
  LinkTransform = true
  LinkedObject = -> Link029 [Edge159]
  TreeRank = 554
  ValidateShape = true
  _LinkVersion = 1
  _Parent = -> Elements001
FEATURE [Part::FeaturePython] _Element164  label="_Element002"  # link proxy (typed FeaturePython)
  Detach = false
  InvalidShape = false
  LinkTransform = true
  LinkedObject = -> Link029 [Edge3]
  TreeRank = 555
  ValidateShape = true
  _LinkVersion = 1
  _Parent = -> Elements001
FEATURE [App::FeaturePython] Constraint080  label="Attachment006"  # WARN: FeaturePython — macro-defined, semantics opaque (R4)
  Cascade = false
  Disabled = false
  Group = -> [ElementLink162,ElementLink163]
  Multiply = false
  TreeRank = 556
  _ConstraintType = 45
  _LinkVersion = 1
  _Parent = -> Constraints001
FEATURE [App::FeaturePython] ElementLink162  label="_Element165"  # link proxy (typed FeaturePython)
  LinkTransform = true
  LinkedObject = -> _Element165
  TreeRank = 557
  _LinkVersion = 1
  _Parent = -> Constraint080
FEATURE [Part::FeaturePython] _Element165  # link proxy (typed FeaturePython)
  Detach = false
  InvalidShape = false
  LinkTransform = true
  LinkedObject = -> Link070 [1.Edge54]
  TreeRank = 558
  ValidateShape = true
  _LinkVersion = 1
  _Parent = -> Elements001
FEATURE [App::FeaturePython] ElementLink163  label="_Element166"  # link proxy (typed FeaturePython)
  LinkTransform = true
  LinkedObject = -> _Element166
  TreeRank = 559
  _LinkVersion = 1
  _Parent = -> Constraint080
FEATURE [Part::FeaturePython] _Element166  # link proxy (typed FeaturePython)
  Detach = false
  InvalidShape = false
  LinkTransform = true
  LinkedObject = -> Link076 [Edge10]
  TreeRank = 560
  ValidateShape = true
  _LinkVersion = 1
  _Parent = -> Elements001
FEATURE [App::FeaturePython] Constraint081  label="PointsCoincident009"  # WARN: FeaturePython — macro-defined, semantics opaque (R4)
  Disabled = false
  Group = -> [ElementLink164,ElementLink165]
  TreeRank = 561
  _ConstraintType = 1
  _LinkVersion = 1
  _Parent = -> Constraints001
FEATURE [App::FeaturePython] ElementLink164  label="_Element167"  # link proxy (typed FeaturePython)
  LinkTransform = true
  LinkedObject = -> _Element167
  TreeRank = 562
  _LinkVersion = 1
  _Parent = -> Constraint081
FEATURE [Part::FeaturePython] _Element167  # link proxy (typed FeaturePython)
  Detach = false
  InvalidShape = false
  LinkTransform = true
  LinkedObject = -> Link070 [1.Face1]
  TreeRank = 563
  ValidateShape = true
  _LinkVersion = 1
  _Parent = -> Elements001
FEATURE [App::FeaturePython] ElementLink165  label="_Element168"  # link proxy (typed FeaturePython)
  LinkTransform = true
  LinkedObject = -> _Element168
  TreeRank = 564
  _LinkVersion = 1
  _Parent = -> Constraint081
FEATURE [Part::FeaturePython] _Element168  # link proxy (typed FeaturePython)
  Detach = false
  InvalidShape = false
  LinkTransform = true
  LinkedObject = -> Link074 [1.Face2]
  TreeRank = 565
  ValidateShape = true
  _LinkVersion = 1
  _Parent = -> Elements001
FEATURE [App::FeaturePython] Constraint082  label="PointsCoincident010"  # WARN: FeaturePython — macro-defined, semantics opaque (R4)
  Disabled = false
  Group = -> [ElementLink166,ElementLink167]
  TreeRank = 566
  _ConstraintType = 1
  _LinkVersion = 1
  _Parent = -> Constraints001
FEATURE [App::FeaturePython] ElementLink166  label="_Element169"  # link proxy (typed FeaturePython)
  LinkTransform = true
  LinkedObject = -> _Element169
  TreeRank = 567
  _LinkVersion = 1
  _Parent = -> Constraint082
FEATURE [Part::FeaturePython] _Element169  # link proxy (typed FeaturePython)
  Detach = false
  InvalidShape = false
  LinkTransform = true
  LinkedObject = -> Link068 [1.Face2]
  TreeRank = 568
  ValidateShape = true
  _LinkVersion = 1
  _Parent = -> Elements001
FEATURE [App::FeaturePython] ElementLink167  label="_Element170"  # link proxy (typed FeaturePython)
  LinkTransform = true
  LinkedObject = -> _Element170
  TreeRank = 569
  _LinkVersion = 1
  _Parent = -> Constraint082
FEATURE [Part::FeaturePython] _Element170  # link proxy (typed FeaturePython)
  Detach = false
  InvalidShape = false
  LinkTransform = true
  LinkedObject = -> Link069 [1.Face1]
  TreeRank = 570
  ValidateShape = true
  _LinkVersion = 1
  _Parent = -> Elements001
FEATURE [App::FeaturePython] Constraint083  label="PointsCoincident011"  # WARN: FeaturePython — macro-defined, semantics opaque (R4)
  Disabled = false
  Group = -> [ElementLink168,ElementLink169]
  TreeRank = 571
  _ConstraintType = 1
  _LinkVersion = 1
  _Parent = -> Constraints001
FEATURE [App::FeaturePython] ElementLink168  label="_Element171"  # link proxy (typed FeaturePython)
  LinkTransform = true
  LinkedObject = -> _Element171
  TreeRank = 572
  _LinkVersion = 1
  _Parent = -> Constraint083
FEATURE [Part::FeaturePython] _Element171  # link proxy (typed FeaturePython)
  Detach = false
  InvalidShape = false
  LinkTransform = true
  LinkedObject = -> Link071 [1.Face1]
  TreeRank = 573
  ValidateShape = true
  _LinkVersion = 1
  _Parent = -> Elements001
FEATURE [App::FeaturePython] ElementLink169  label="_Element170"  # link proxy (typed FeaturePython)
  LinkTransform = true
  LinkedObject = -> _Element170
  TreeRank = 574
  _LinkVersion = 1
  _Parent = -> Constraint083
FEATURE [App::FeaturePython] Constraint084  label="PointsCoincident012"  # WARN: FeaturePython — macro-defined, semantics opaque (R4)
  Disabled = false
  Group = -> [ElementLink170,ElementLink171]
  TreeRank = 575
  _ConstraintType = 1
  _LinkVersion = 1
  _Parent = -> Constraints001
FEATURE [App::FeaturePython] ElementLink170  label="_Element172"  # link proxy (typed FeaturePython)
  LinkTransform = true
  LinkedObject = -> _Element172
  TreeRank = 576
  _LinkVersion = 1
  _Parent = -> Constraint084
FEATURE [Part::FeaturePython] _Element172  # link proxy (typed FeaturePython)
  Detach = false
  InvalidShape = false
  LinkTransform = true
  LinkedObject = -> Link072 [1.Face3]
  TreeRank = 577
  ValidateShape = true
  _LinkVersion = 1
  _Parent = -> Elements001
FEATURE [App::FeaturePython] ElementLink171  label="_Element168"  # link proxy (typed FeaturePython)
  LinkTransform = true
  LinkedObject = -> _Element168
  TreeRank = 578
  _LinkVersion = 1
  _Parent = -> Constraint084
FEATURE [App::FeaturePython] Constraint085  label="Attachment007"  # WARN: FeaturePython — macro-defined, semantics opaque (R4)
  Cascade = false
  Disabled = false
  Group = -> [ElementLink172,ElementLink173]
  Multiply = false
  TreeRank = 579
  _ConstraintType = 45
  _LinkVersion = 1
  _Parent = -> Constraints001
FEATURE [App::FeaturePython] ElementLink172  label="_Element173"  # link proxy (typed FeaturePython)
  LinkTransform = true
  LinkedObject = -> _Element173
  TreeRank = 580
  _LinkVersion = 1
  _Parent = -> Constraint085
FEATURE [Part::FeaturePython] _Element173  # link proxy (typed FeaturePython)
  Detach = false
  InvalidShape = false
  LinkTransform = true
  LinkedObject = -> Link067 [1.Edge27]
  TreeRank = 581
  ValidateShape = true
  _LinkVersion = 1
  _Parent = -> Elements001
FEATURE [App::FeaturePython] ElementLink173  label="_Element174"  # link proxy (typed FeaturePython)
  LinkTransform = true
  LinkedObject = -> _Element174
  TreeRank = 582
  _LinkVersion = 1
  _Parent = -> Constraint085
FEATURE [Part::FeaturePython] _Element174  # link proxy (typed FeaturePython)
  Detach = false
  InvalidShape = false
  LinkTransform = true
  LinkedObject = -> Link075 [Edge10]
  TreeRank = 583
  ValidateShape = true
  _LinkVersion = 1
  _Parent = -> Elements001
FEATURE [App::FeaturePython] Constraint086  label="AxialAlignment002"  # WARN: FeaturePython — macro-defined, semantics opaque (R4)
  Angle = 0
  AnglePitch = 0
  AngleRoll = 0
  Disabled = false
  Group = -> [ElementLink174,ElementLink175]
  LockAngle = false
  Multiply = false
  TreeRank = 584
  _ConstraintType = 36
  _LinkVersion = 1
  _Parent = -> Constraints001
FEATURE [App::FeaturePython] ElementLink174  label="_Element175"  # link proxy (typed FeaturePython)
  LinkTransform = true
  LinkedObject = -> _Element175
  TreeRank = 585
  _LinkVersion = 1
  _Parent = -> Constraint086
FEATURE [Part::FeaturePython] _Element175  # link proxy (typed FeaturePython)
  Detach = false
  InvalidShape = false
  LinkTransform = true
  LinkedObject = -> Link071 [1.Face21]
  TreeRank = 586
  ValidateShape = true
  _LinkVersion = 1
  _Parent = -> Elements001
FEATURE [App::FeaturePython] ElementLink175  label="_Element176"  # link proxy (typed FeaturePython)
  LinkTransform = true
  LinkedObject = -> _Element176
  TreeRank = 587
  _LinkVersion = 1
  _Parent = -> Constraint086
FEATURE [Part::FeaturePython] _Element176  # link proxy (typed FeaturePython)
  Detach = false
  InvalidShape = false
  LinkTransform = true
  LinkedObject = -> Link073 [1.Edge55]
  TreeRank = 588
  ValidateShape = true
  _LinkVersion = 1
  _Parent = -> Elements001
FEATURE [App::FeaturePython] Constraint087  label="AxialAlignment003"  # WARN: FeaturePython — macro-defined, semantics opaque (R4)
  Angle = 0
  AnglePitch = 0
  AngleRoll = 0
  Disabled = false
  Group = -> [ElementLink176,ElementLink177]
  LockAngle = false
  Multiply = false
  TreeRank = 589
  _ConstraintType = 36
  _LinkVersion = 1
  _Parent = -> Constraints001
FEATURE [App::FeaturePython] ElementLink176  label="_Element177"  # link proxy (typed FeaturePython)
  LinkTransform = true
  LinkedObject = -> _Element177
  TreeRank = 590
  _LinkVersion = 1
  _Parent = -> Constraint087
FEATURE [Part::FeaturePython] _Element177  # link proxy (typed FeaturePython)
  Detach = false
  InvalidShape = false
  LinkTransform = true
  LinkedObject = -> Link073 [1.Face95]
  TreeRank = 591
  ValidateShape = true
  _LinkVersion = 1
  _Parent = -> Elements001
FEATURE [App::FeaturePython] ElementLink177  label="_Element178"  # link proxy (typed FeaturePython)
  LinkTransform = true
  LinkedObject = -> _Element178
  TreeRank = 592
  _LinkVersion = 1
  _Parent = -> Constraint087
FEATURE [Part::FeaturePython] _Element178  # link proxy (typed FeaturePython)
  Detach = false
  InvalidShape = false
  LinkTransform = true
  LinkedObject = -> Link072 [1.Face21]
  TreeRank = 593
  ValidateShape = true
  _LinkVersion = 1
  _Parent = -> Elements001
FEATURE [App::FeaturePython] Constraint088  label="PointInPlane001"  # WARN: FeaturePython — macro-defined, semantics opaque (R4)
  Disabled = false
  Group = -> [ElementLink178,ElementLink179]
  TreeRank = 594
  _ConstraintType = 3
  _LinkVersion = 1
  _Parent = -> Constraints001
FEATURE [App::FeaturePython] ElementLink178  label="_Element179"  # link proxy (typed FeaturePython)
  LinkTransform = true
  LinkedObject = -> _Element179
  TreeRank = 595
  _LinkVersion = 1
  _Parent = -> Constraint088
FEATURE [Part::FeaturePython] _Element179  # link proxy (typed FeaturePython)
  Detach = false
  InvalidShape = false
  LinkTransform = true
  LinkedObject = -> Link072 [1.Vertex77]
  TreeRank = 596
  ValidateShape = true
  _LinkVersion = 1
  _Parent = -> Elements001
FEATURE [App::FeaturePython] ElementLink179  label="_Element180"  # link proxy (typed FeaturePython)
  LinkTransform = true
  LinkedObject = -> _Element180
  TreeRank = 597
  _LinkVersion = 1
  _Parent = -> Constraint088
FEATURE [Part::FeaturePython] _Element180  # link proxy (typed FeaturePython)
  Detach = false
  InvalidShape = false
  LinkTransform = true
  LinkedObject = -> Link073 [1.Face79]
  TreeRank = 598
  ValidateShape = true
  _LinkVersion = 1
  _Parent = -> Elements001
FEATURE [App::DocumentObjectGroupPython] Group011  label="dogbones"  # scripted group (container) (typed FeaturePython)
  ClaimAllChildren = true
  ExportMode = 0
  Group = -> [Link076,Link067,Link068,Link069,Link070,Link071,Link072,Link073,Link074,Link075]
  TreeRank = 600
  _GroupVersion = 1
  _Parent = -> Parts001
FEATURE [App::DocumentObjectGroupPython] Group012  label="DogBone"  # scripted group (container) (typed FeaturePython)
  ClaimAllChildren = true
  ExportMode = 0
  Group = -> [Constraint068,Constraint069,Constraint070,Constraint071,Constraint072,Constraint073,Constraint074,Constraint075,Constraint076,Constraint077,Constraint078,Constraint079,Constraint080,Constraint081,Constraint082,Constraint083,Constraint084,Constraint085,Constraint086,Constraint087,Constraint088]
  TreeRank = 611
  _GroupVersion = 1
  _Parent = -> Constraints001
FEATURE [App::FeaturePython] Constraint089  label="Attachment009"  # WARN: FeaturePython — macro-defined, semantics opaque (R4)
  Cascade = false
  Disabled = false
  Group = -> [ElementLink180,ElementLink181]
  Multiply = false
  TreeRank = 617
  _ConstraintType = 45
  _LinkVersion = 1
  _Parent = -> Constraints001
FEATURE [App::FeaturePython] ElementLink180  label="_Element181"  # link proxy (typed FeaturePython)
  LinkTransform = true
  LinkedObject = -> _Element181
  TreeRank = 618
  _LinkVersion = 1
  _Parent = -> Constraint089
FEATURE [Part::FeaturePython] _Element181  # link proxy (typed FeaturePython)
  Detach = false
  InvalidShape = false
  LinkTransform = true
  LinkedObject = -> Link078 [0.Edge30]
  TreeRank = 619
  ValidateShape = true
  _LinkVersion = 1
  _Parent = -> Elements001
FEATURE [App::FeaturePython] ElementLink181  label="_Element182"  # link proxy (typed FeaturePython)
  LinkTransform = true
  LinkedObject = -> _Element182
  TreeRank = 620
  _LinkVersion = 1
  _Parent = -> Constraint089
FEATURE [Part::FeaturePython] _Element182  # link proxy (typed FeaturePython)
  Detach = false
  InvalidShape = false
  LinkTransform = true
  LinkedObject = -> Link039 [Edge126]
  TreeRank = 621
  ValidateShape = true
  _LinkVersion = 1
  _Parent = -> Elements001
FEATURE [Part::FeaturePython] _Element183  # link proxy (typed FeaturePython)
  Detach = false
  InvalidShape = false
  LinkTransform = true
  LinkedObject = -> Link078 [1.Edge27]
  TreeRank = 624
  ValidateShape = true
  _LinkVersion = 1
  _Parent = -> Elements001
FEATURE [Part::FeaturePython] _Element184  # link proxy (typed FeaturePython)
  Detach = false
  InvalidShape = false
  LinkTransform = true
  LinkedObject = -> Link043 [Edge4]
  TreeRank = 626
  ValidateShape = true
  _LinkVersion = 1
  _Parent = -> Elements001
FEATURE [App::FeaturePython] Constraint090  label="Attachment008"  # WARN: FeaturePython — macro-defined, semantics opaque (R4)
  Cascade = false
  Disabled = false
  Group = -> [ElementLink182,ElementLink183]
  Multiply = false
  TreeRank = 627
  _ConstraintType = 45
  _LinkVersion = 1
  _Parent = -> Constraints001
FEATURE [App::FeaturePython] ElementLink182  label="_Element183"  # link proxy (typed FeaturePython)
  LinkTransform = true
  LinkedObject = -> _Element183
  TreeRank = 628
  _LinkVersion = 1
  _Parent = -> Constraint090
FEATURE [App::FeaturePython] ElementLink183  label="_Element184"  # link proxy (typed FeaturePython)
  LinkTransform = true
  LinkedObject = -> _Element184
  TreeRank = 629
  _LinkVersion = 1
  _Parent = -> Constraint090
FEATURE [App::FeaturePython] Constraint091  label="Attachment010"  # WARN: FeaturePython — macro-defined, semantics opaque (R4)
  Cascade = false
  Disabled = false
  Group = -> [ElementLink184,ElementLink185]
  Multiply = false
  TreeRank = 630
  _ConstraintType = 45
  _LinkVersion = 1
  _Parent = -> Constraints001
FEATURE [App::FeaturePython] ElementLink184  label="_Element185"  # link proxy (typed FeaturePython)
  LinkTransform = true
  LinkedObject = -> _Element185
  TreeRank = 631
  _LinkVersion = 1
  _Parent = -> Constraint091
FEATURE [Part::FeaturePython] _Element185  # link proxy (typed FeaturePython)
  Detach = false
  InvalidShape = false
  LinkTransform = true
  LinkedObject = -> Link038 [Edge126]
  TreeRank = 632
  ValidateShape = true
  _LinkVersion = 1
  _Parent = -> Elements001
FEATURE [App::FeaturePython] ElementLink185  label="_Element186"  # link proxy (typed FeaturePython)
  LinkTransform = true
  LinkedObject = -> _Element186
  TreeRank = 633
  _LinkVersion = 1
  _Parent = -> Constraint091
FEATURE [Part::FeaturePython] _Element186  # link proxy (typed FeaturePython)
  Detach = false
  InvalidShape = false
  LinkTransform = true
  LinkedObject = -> Link078 [2.Edge32]
  TreeRank = 634
  ValidateShape = true
  _LinkVersion = 1
  _Parent = -> Elements001
FEATURE [App::FeaturePython] Constraint092  label="Attachment011"  # WARN: FeaturePython — macro-defined, semantics opaque (R4)
  Cascade = false
  Disabled = false
  Group = -> [ElementLink186,ElementLink187]
  Multiply = false
  TreeRank = 635
  _ConstraintType = 45
  _LinkVersion = 1
  _Parent = -> Constraints001
FEATURE [App::FeaturePython] ElementLink186  label="_Element187"  # link proxy (typed FeaturePython)
  LinkTransform = true
  LinkedObject = -> _Element187
  TreeRank = 636
  _LinkVersion = 1
  _Parent = -> Constraint092
FEATURE [Part::FeaturePython] _Element187  # link proxy (typed FeaturePython)
  Detach = false
  InvalidShape = false
  LinkTransform = true
  LinkedObject = -> Link078 [3.Edge30]
  TreeRank = 637
  ValidateShape = true
  _LinkVersion = 1
  _Parent = -> Elements001
FEATURE [App::FeaturePython] ElementLink187  label="_Element188"  # link proxy (typed FeaturePython)
  LinkTransform = true
  LinkedObject = -> _Element188
  TreeRank = 638
  _LinkVersion = 1
  _Parent = -> Constraint092
FEATURE [Part::FeaturePython] _Element188  # link proxy (typed FeaturePython)
  Detach = false
  InvalidShape = false
  LinkTransform = true
  LinkedObject = -> Link047 [Edge4]
  TreeRank = 639
  ValidateShape = true
  _LinkVersion = 1
  _Parent = -> Elements001
FEATURE [App::FeaturePython] Constraint093  label="Attachment012"  # WARN: FeaturePython — macro-defined, semantics opaque (R4)
  Cascade = false
  Disabled = false
  Group = -> [ElementLink188,ElementLink189]
  Multiply = false
  TreeRank = 646
  _ConstraintType = 45
  _LinkVersion = 1
  _Parent = -> Constraints001
FEATURE [App::FeaturePython] ElementLink188  label="_Element189"  # link proxy (typed FeaturePython)
  LinkTransform = true
  LinkedObject = -> _Element189
  TreeRank = 647
  _LinkVersion = 1
  _Parent = -> Constraint093
FEATURE [Part::FeaturePython] _Element189  # link proxy (typed FeaturePython)
  Detach = false
  InvalidShape = false
  LinkTransform = true
  LinkedObject = -> Link079 [0.Edge9]
  TreeRank = 648
  ValidateShape = true
  _LinkVersion = 1
  _Parent = -> Elements001
FEATURE [App::FeaturePython] ElementLink189  label="_Element190"  # link proxy (typed FeaturePython)
  LinkTransform = true
  LinkedObject = -> _Element190
  TreeRank = 649
  _LinkVersion = 1
  _Parent = -> Constraint093
FEATURE [Part::FeaturePython] _Element190  # link proxy (typed FeaturePython)
  Detach = false
  InvalidShape = false
  LinkTransform = true
  LinkedObject = -> Link056 [Edge33]
  TreeRank = 650
  ValidateShape = true
  _LinkVersion = 1
  _Parent = -> Elements001
FEATURE [App::FeaturePython] Constraint094  label="Attachment013"  # WARN: FeaturePython — macro-defined, semantics opaque (R4)
  Cascade = false
  Disabled = false
  Group = -> [ElementLink190,ElementLink191]
  Multiply = false
  TreeRank = 651
  _ConstraintType = 45
  _LinkVersion = 1
  _Parent = -> Constraints001
FEATURE [App::FeaturePython] ElementLink190  label="_Element191"  # link proxy (typed FeaturePython)
  LinkTransform = true
  LinkedObject = -> _Element191
  TreeRank = 652
  _LinkVersion = 1
  _Parent = -> Constraint094
FEATURE [Part::FeaturePython] _Element191  # link proxy (typed FeaturePython)
  Detach = false
  InvalidShape = false
  LinkTransform = true
  LinkedObject = -> Link079 [1.Edge9]
  TreeRank = 653
  ValidateShape = true
  _LinkVersion = 1
  _Parent = -> Elements001
FEATURE [App::FeaturePython] ElementLink191  label="_Element192"  # link proxy (typed FeaturePython)
  LinkTransform = true
  LinkedObject = -> _Element192
  TreeRank = 654
  _LinkVersion = 1
  _Parent = -> Constraint094
FEATURE [Part::FeaturePython] _Element192  # link proxy (typed FeaturePython)
  Detach = false
  InvalidShape = false
  LinkTransform = true
  LinkedObject = -> Link067 [1.Edge25]
  TreeRank = 655
  ValidateShape = true
  _LinkVersion = 1
  _Parent = -> Elements001
FEATURE [App::FeaturePython] Constraint095  label="Attachment014"  # WARN: FeaturePython — macro-defined, semantics opaque (R4)
  Cascade = false
  Disabled = false
  Group = -> [ElementLink192,ElementLink193]
  Multiply = false
  TreeRank = 656
  _ConstraintType = 45
  _LinkVersion = 1
  _Parent = -> Constraints001
FEATURE [App::FeaturePython] ElementLink192  label="_Element193"  # link proxy (typed FeaturePython)
  LinkTransform = true
  LinkedObject = -> _Element193
  TreeRank = 657
  _LinkVersion = 1
  _Parent = -> Constraint095
FEATURE [Part::FeaturePython] _Element193  # link proxy (typed FeaturePython)
  Detach = false
  InvalidShape = false
  LinkTransform = true
  LinkedObject = -> Link079 [2.Edge9]
  TreeRank = 658
  ValidateShape = true
  _LinkVersion = 1
  _Parent = -> Elements001
FEATURE [App::FeaturePython] ElementLink193  label="_Element194"  # link proxy (typed FeaturePython)
  LinkTransform = true
  LinkedObject = -> _Element194
  TreeRank = 659
  _LinkVersion = 1
  _Parent = -> Constraint095
FEATURE [Part::FeaturePython] _Element194  # link proxy (typed FeaturePython)
  Detach = false
  InvalidShape = false
  LinkTransform = true
  LinkedObject = -> Link054 [Edge33]
  TreeRank = 660
  ValidateShape = true
  _LinkVersion = 1
  _Parent = -> Elements001
FEATURE [App::FeaturePython] Constraint096  label="Attachment015"  # WARN: FeaturePython — macro-defined, semantics opaque (R4)
  Cascade = false
  Disabled = false
  Group = -> [ElementLink194,ElementLink195]
  Multiply = false
  TreeRank = 661
  _ConstraintType = 45
  _LinkVersion = 1
  _Parent = -> Constraints001
FEATURE [App::FeaturePython] ElementLink194  label="_Element195"  # link proxy (typed FeaturePython)
  LinkTransform = true
  LinkedObject = -> _Element195
  TreeRank = 662
  _LinkVersion = 1
  _Parent = -> Constraint096
FEATURE [Part::FeaturePython] _Element195  # link proxy (typed FeaturePython)
  Detach = false
  InvalidShape = false
  LinkTransform = true
  LinkedObject = -> Link079 [3.Edge9]
  TreeRank = 663
  ValidateShape = true
  _LinkVersion = 1
  _Parent = -> Elements001
FEATURE [App::FeaturePython] ElementLink195  label="_Element196"  # link proxy (typed FeaturePython)
  LinkTransform = true
  LinkedObject = -> _Element196
  TreeRank = 664
  _LinkVersion = 1
  _Parent = -> Constraint096
FEATURE [Part::FeaturePython] _Element196  # link proxy (typed FeaturePython)
  Detach = false
  InvalidShape = false
  LinkTransform = true
  LinkedObject = -> Link069 [0.Edge171]
  TreeRank = 665
  ValidateShape = true
  _LinkVersion = 1
  _Parent = -> Elements001
FEATURE [Part::FeaturePython] Element023  # link proxy (typed FeaturePython)
  Detach = false
  InvalidShape = false
  LinkTransform = true
  LinkedObject = -> Link017 [Edge56]
  TreeRank = 676
  ValidateShape = true
  _LinkVersion = 1
  _Parent = -> Elements
FEATURE [App::FeaturePython] Constraint097  label="Attachment016"  # WARN: FeaturePython — macro-defined, semantics opaque (R4)
  Cascade = false
  Disabled = false
  Group = -> [ElementLink196,ElementLink197]
  Multiply = true
  TreeRank = 677
  _ConstraintType = 45
  _LinkVersion = 1
  _Parent = -> Constraints001
FEATURE [App::FeaturePython] ElementLink196  label="_Element197"  # link proxy (typed FeaturePython)
  AutoCount = true
  Count = 5
  LinkTransform = true
  LinkedObject = -> _Element197
  PlacementList = 5 placements: [(-2.84217e-14,7.10543e-15,-3.55271e-15),(3.97904e-13,-11,-4.26326e-14),(7.67386e-13,-22,-8.17124e-14),(-7.24444,-16.5,-1.94114),(-7.24444,-5.5,-1.94114)]
  ShowElement = false
  TreeRank = 678
  _LinkVersion = 1
  _Parent = -> Constraint097
FEATURE [Part::FeaturePython] _Element197  # link proxy (typed FeaturePython)
  Detach = false
  InvalidShape = false
  LinkTransform = true
  LinkedObject = -> Link080 [0.Edge30]
  TreeRank = 679
  ValidateShape = true
  _LinkVersion = 1
  _Parent = -> Elements001
FEATURE [App::FeaturePython] ElementLink197  label="_Element003"  # link proxy (typed FeaturePython)
  LinkTransform = true
  LinkedObject = -> _Element199
  NoExpand = false
  TreeRank = 680
  _LinkVersion = 1
  _Parent = -> Constraint097
FEATURE [Part::FeaturePython] _Element198  # link proxy (typed FeaturePython)
  Detach = false
  InvalidShape = false
  LinkTransform = true
  LinkedObject = -> Assembly [1.$Element023.]
  TreeRank = 681
  ValidateShape = true
  _LinkVersion = 1
  _Parent = -> Elements001
FEATURE [Part::FeaturePython] Element024  # link proxy (typed FeaturePython)
  Detach = false
  InvalidShape = false
  LinkTransform = true
  LinkedObject = -> Link017 [Edge56]
  Radius = 2.1
  TreeRank = 682
  ValidateShape = true
  _LinkVersion = 1
  _Parent = -> Elements
FEATURE [Part::FeaturePython] _Element199  label="_Element003"  # link proxy (typed FeaturePython)
  Detach = false
  InvalidShape = false
  LinkTransform = true
  LinkedObject = -> Assembly [1.$Element024.]
  TreeRank = 683
  ValidateShape = true
  _LinkVersion = 1
  _Parent = -> Elements001
FEATURE [Part::FeaturePython] _Element200  # link proxy (typed FeaturePython)
  Detach = false
  InvalidShape = false
  LinkTransform = true
  LinkedObject = -> Link015 [Vertex68]
  TreeRank = 686
  ValidateShape = true
  _LinkVersion = 1
  _Parent = -> Elements
FEATURE [Part::FeaturePython] _Element201  # link proxy (typed FeaturePython)
  Detach = false
  InvalidShape = false
  LinkTransform = true
  LinkedObject = -> Link014 [Vertex5]
  TreeRank = 688
  ValidateShape = true
  _LinkVersion = 1
  _Parent = -> Elements
FEATURE [App::DocumentObjectGroupPython] Group013  label="Fasteners"  # scripted group (container) (typed FeaturePython)
  ClaimAllChildren = true
  ExportMode = 0
  Group = -> [Link078,Link079,Link080,Link081,Link082,Link083,Link084,Link085]
  TreeRank = 690
  _GroupVersion = 1
  _Parent = -> Parts001
FEATURE [Part::FeaturePython] _Element202  # link proxy (typed FeaturePython)
  Detach = false
  InvalidShape = false
  LinkTransform = true
  LinkedObject = -> Link081 [0.Edge27]
  TreeRank = 693
  ValidateShape = true
  _LinkVersion = 1
  _Parent = -> Elements001
FEATURE [Part::FeaturePython] Element025  # link proxy (typed FeaturePython)
  Detach = false
  InvalidShape = false
  LinkTransform = true
  LinkedObject = -> Link015 [Edge86]
  TreeRank = 695
  ValidateShape = true
  _LinkVersion = 1
  _Parent = -> Elements
FEATURE [Part::FeaturePython] _Element203  # link proxy (typed FeaturePython)
  Detach = false
  InvalidShape = false
  LinkTransform = true
  LinkedObject = -> Assembly [1.$Element025.]
  TreeRank = 696
  ValidateShape = true
  _LinkVersion = 1
  _Parent = -> Elements001
FEATURE [Part::FeaturePython] Element026  # link proxy (typed FeaturePython)
  Detach = false
  InvalidShape = false
  LinkTransform = true
  LinkedObject = -> Link015 [Edge86]
  Radius = 4.125
  TreeRank = 697
  ValidateShape = true
  _LinkVersion = 1
  _Parent = -> Elements
FEATURE [Part::FeaturePython] _Element204  label="_Element004"  # link proxy (typed FeaturePython)
  Detach = false
  InvalidShape = false
  LinkTransform = true
  LinkedObject = -> Assembly [1.$Element026.]
  TreeRank = 698
  ValidateShape = true
  _LinkVersion = 1
  _Parent = -> Elements001
FEATURE [App::FeaturePython] Constraint099  label="PlaneAlignment003"  # WARN: FeaturePython — macro-defined, semantics opaque (R4)
  Angle = 0
  AnglePitch = 0
  AngleRoll = 0
  Cascade = false
  Disabled = false
  Group = -> [ElementLink200,ElementLink201]
  LockAngle = false
  TreeRank = 699
  _ConstraintType = 37
  _LinkVersion = 1
  _Parent = -> Constraints001
FEATURE [App::FeaturePython] ElementLink200  label="_Element205"  # link proxy (typed FeaturePython)
  LinkTransform = true
  LinkedObject = -> _Element205
  TreeRank = 700
  _LinkVersion = 1
  _Parent = -> Constraint099
FEATURE [Part::FeaturePython] _Element205  # link proxy (typed FeaturePython)
  Detach = false
  InvalidShape = false
  LinkTransform = true
  LinkedObject = -> Link081 [3.Edge27]
  TreeRank = 701
  ValidateShape = true
  _LinkVersion = 1
  _Parent = -> Elements001
FEATURE [App::FeaturePython] ElementLink201  label="_Element206"  # link proxy (typed FeaturePython)
  LinkTransform = true
  LinkedObject = -> _Element206
  TreeRank = 702
  _LinkVersion = 1
  _Parent = -> Constraint099
FEATURE [Part::FeaturePython] Element027  # link proxy (typed FeaturePython)
  Detach = false
  InvalidShape = false
  LinkTransform = true
  LinkedObject = -> Link015 [Edge82]
  TreeRank = 703
  ValidateShape = true
  _LinkVersion = 1
  _Parent = -> Elements
FEATURE [Part::FeaturePython] _Element206  # link proxy (typed FeaturePython)
  Detach = false
  InvalidShape = false
  LinkTransform = true
  LinkedObject = -> Assembly [1.$Element027.]
  TreeRank = 704
  ValidateShape = true
  _LinkVersion = 1
  _Parent = -> Elements001
FEATURE [App::FeaturePython] Constraint100  label="PlaneAlignment002"  # WARN: FeaturePython — macro-defined, semantics opaque (R4)
  Angle = 0
  AnglePitch = 0
  AngleRoll = 0
  Cascade = false
  Disabled = false
  Group = -> [ElementLink202,ElementLink203]
  LockAngle = false
  TreeRank = 705
  _ConstraintType = 37
  _LinkVersion = 1
  _Parent = -> Constraints001
FEATURE [App::FeaturePython] ElementLink202  label="_Element202"  # link proxy (typed FeaturePython)
  LinkTransform = true
  LinkedObject = -> _Element202
  TreeRank = 706
  _LinkVersion = 1
  _Parent = -> Constraint100
FEATURE [App::FeaturePython] ElementLink203  label="_Element203"  # link proxy (typed FeaturePython)
  LinkTransform = true
  LinkedObject = -> _Element203
  TreeRank = 707
  _LinkVersion = 1
  _Parent = -> Constraint100
FEATURE [App::FeaturePython] Constraint101  label="PlaneAlignment001"  # WARN: FeaturePython — macro-defined, semantics opaque (R4)
  Angle = 0
  AnglePitch = 0
  AngleRoll = 0
  Cascade = false
  Disabled = false
  Group = -> [ElementLink204,ElementLink205]
  LockAngle = false
  TreeRank = 708
  _ConstraintType = 37
  _LinkVersion = 1
  _Parent = -> Constraints001
FEATURE [App::FeaturePython] ElementLink204  label="_Element207"  # link proxy (typed FeaturePython)
  LinkTransform = true
  LinkedObject = -> _Element207
  TreeRank = 709
  _LinkVersion = 1
  _Parent = -> Constraint101
FEATURE [Part::FeaturePython] _Element207  # link proxy (typed FeaturePython)
  Detach = false
  InvalidShape = false
  LinkTransform = true
  LinkedObject = -> Link081 [1.Edge27]
  TreeRank = 710
  ValidateShape = true
  _LinkVersion = 1
  _Parent = -> Elements001
FEATURE [App::FeaturePython] ElementLink205  label="_Element208"  # link proxy (typed FeaturePython)
  LinkTransform = true
  LinkedObject = -> _Element208
  TreeRank = 711
  _LinkVersion = 1
  _Parent = -> Constraint101
FEATURE [Part::FeaturePython] Element028  # link proxy (typed FeaturePython)
  Detach = false
  InvalidShape = false
  LinkTransform = true
  LinkedObject = -> Link015 [Edge100]
  TreeRank = 712
  ValidateShape = true
  _LinkVersion = 1
  _Parent = -> Elements
FEATURE [Part::FeaturePython] _Element208  # link proxy (typed FeaturePython)
  Detach = false
  InvalidShape = false
  LinkTransform = true
  LinkedObject = -> Assembly [1.$Element028.]
  TreeRank = 713
  ValidateShape = true
  _LinkVersion = 1
  _Parent = -> Elements001
FEATURE [App::FeaturePython] Constraint102  label="PlaneAlignment"  # WARN: FeaturePython — macro-defined, semantics opaque (R4)
  Angle = 0
  AnglePitch = 0
  AngleRoll = 0
  Cascade = false
  Disabled = false
  Group = -> [ElementLink206,ElementLink207]
  LockAngle = false
  TreeRank = 714
  _ConstraintType = 37
  _LinkVersion = 1
  _Parent = -> Constraints001
FEATURE [App::FeaturePython] ElementLink206  label="_Element209"  # link proxy (typed FeaturePython)
  LinkTransform = true
  LinkedObject = -> _Element209
  TreeRank = 715
  _LinkVersion = 1
  _Parent = -> Constraint102
FEATURE [Part::FeaturePython] _Element209  # link proxy (typed FeaturePython)
  Detach = false
  InvalidShape = false
  LinkTransform = true
  LinkedObject = -> Link081 [2.Edge27]
  TreeRank = 716
  ValidateShape = true
  _LinkVersion = 1
  _Parent = -> Elements001
FEATURE [App::FeaturePython] ElementLink207  label="_Element210"  # link proxy (typed FeaturePython)
  LinkTransform = true
  LinkedObject = -> _Element210
  TreeRank = 717
  _LinkVersion = 1
  _Parent = -> Constraint102
FEATURE [Part::FeaturePython] Element029  # link proxy (typed FeaturePython)
  Detach = false
  InvalidShape = false
  LinkTransform = true
  LinkedObject = -> Link015 [Edge104]
  TreeRank = 718
  ValidateShape = true
  _LinkVersion = 1
  _Parent = -> Elements
FEATURE [Part::FeaturePython] _Element210  # link proxy (typed FeaturePython)
  Detach = false
  InvalidShape = false
  LinkTransform = true
  LinkedObject = -> Assembly [1.$Element029.]
  TreeRank = 719
  ValidateShape = true
  _LinkVersion = 1
  _Parent = -> Elements001
FEATURE [App::FeaturePython] Constraint103  label="PlaneCoincident038"  # WARN: FeaturePython — macro-defined, semantics opaque (R4)
  Angle = 0
  AnglePitch = 0
  AngleRoll = 180
  Cascade = false
  Disabled = false
  Group = -> [ElementLink208,ElementLink209]
  LockAngle = true
  Multiply = true
  OffsetX = 0
  OffsetY = 0
  TreeRank = 721
  _ConstraintType = 35
  _LinkVersion = 1
  _Parent = -> Constraints001
FEATURE [App::FeaturePython] ElementLink208  label="_Element211"  # link proxy (typed FeaturePython)
  AutoCount = true
  Count = 4
  LinkTransform = true
  LinkedObject = -> _Element211
  PlacementList = 4 placements: [(1.42109e-14,0,0),(-8.52651e-14,2.84217e-14,-34),(2.81375e-12,-78,-7.81597e-14),(2.71427e-12,-78,-34)]
  ShowElement = false
  TreeRank = 722
  _LinkVersion = 1
  _Parent = -> Constraint103
FEATURE [Part::FeaturePython] _Element211  # link proxy (typed FeaturePython)
  Detach = false
  InvalidShape = false
  LinkTransform = true
  LinkedObject = -> Link082 [0.Edge30]
  TreeRank = 723
  ValidateShape = true
  _LinkVersion = 1
  _Parent = -> Elements001
FEATURE [App::FeaturePython] ElementLink209  label="_Element005"  # link proxy (typed FeaturePython)
  LinkTransform = true
  LinkedObject = -> _Element213
  NoExpand = false
  TreeRank = 724
  _LinkVersion = 1
  _Parent = -> Constraint103
FEATURE [Part::FeaturePython] Element030  # link proxy (typed FeaturePython)
  Detach = false
  InvalidShape = false
  LinkTransform = true
  LinkedObject = -> Link011 [Edge106]
  TreeRank = 725
  ValidateShape = true
  _LinkVersion = 1
  _Parent = -> Elements
FEATURE [Part::FeaturePython] _Element212  # link proxy (typed FeaturePython)
  Detach = false
  InvalidShape = false
  LinkTransform = true
  LinkedObject = -> Assembly [1.$Element030.]
  TreeRank = 726
  ValidateShape = true
  _LinkVersion = 1
  _Parent = -> Elements001
FEATURE [Part::FeaturePython] Element031  # link proxy (typed FeaturePython)
  Detach = false
  InvalidShape = false
  LinkTransform = true
  LinkedObject = -> Link011 [Edge106]
  Radius = 2.25
  TreeRank = 727
  ValidateShape = true
  _LinkVersion = 1
  _Parent = -> Elements
FEATURE [Part::FeaturePython] _Element213  label="_Element005"  # link proxy (typed FeaturePython)
  Detach = false
  InvalidShape = false
  LinkTransform = true
  LinkedObject = -> Assembly [1.$Element031.]
  TreeRank = 728
  ValidateShape = true
  _LinkVersion = 1
  _Parent = -> Elements001
FEATURE [Part::FeaturePython] _Element214  # link proxy (typed FeaturePython)
  Detach = false
  InvalidShape = false
  LinkTransform = true
  LinkedObject = -> Link011 [Vertex79]
  TreeRank = 735
  ValidateShape = true
  _LinkVersion = 1
  _Parent = -> Elements
FEATURE [Part::FeaturePython] _Element215  # link proxy (typed FeaturePython)
  Detach = false
  InvalidShape = false
  LinkTransform = true
  LinkedObject = -> Link012 [Vertex60]
  TreeRank = 737
  ValidateShape = true
  _LinkVersion = 1
  _Parent = -> Elements
FEATURE [App::FeaturePython] Constraint104  label="Attachment017"  # WARN: FeaturePython — macro-defined, semantics opaque (R4)
  Cascade = false
  Disabled = false
  Group = -> [ElementLink210,ElementLink211]
  Multiply = true
  TreeRank = 739
  _ConstraintType = 45
  _LinkVersion = 1
  _Parent = -> Constraints001
FEATURE [App::FeaturePython] ElementLink210  label="_Element216"  # link proxy (typed FeaturePython)
  AutoCount = true
  Count = 3
  LinkTransform = true
  LinkedObject = -> _Element216
  PlacementList = 3 placements: [(0,0,-3.55271e-15),(-7.67386e-13,20,-2.13163e-14),(-1.4353e-12,40,7.4607e-14)]
  ShowElement = false
  TreeRank = 740
  _LinkVersion = 1
  _Parent = -> Constraint104
FEATURE [Part::FeaturePython] _Element216  # link proxy (typed FeaturePython)
  Detach = false
  InvalidShape = false
  LinkTransform = true
  LinkedObject = -> Link083 [0.Edge30]
  TreeRank = 741
  ValidateShape = true
  _LinkVersion = 1
  _Parent = -> Elements001
FEATURE [App::FeaturePython] ElementLink211  label="_Element006"  # link proxy (typed FeaturePython)
  LinkTransform = true
  LinkedObject = -> _Element218
  NoExpand = false
  TreeRank = 742
  _LinkVersion = 1
  _Parent = -> Constraint104
FEATURE [Part::FeaturePython] Element032  # link proxy (typed FeaturePython)
  Detach = false
  InvalidShape = false
  LinkTransform = true
  LinkedObject = -> Link009 [Edge92]
  TreeRank = 743
  ValidateShape = true
  _LinkVersion = 1
  _Parent = -> Elements
FEATURE [Part::FeaturePython] _Element217  # link proxy (typed FeaturePython)
  Detach = false
  InvalidShape = false
  LinkTransform = true
  LinkedObject = -> Assembly [1.$Element032.]
  TreeRank = 744
  ValidateShape = true
  _LinkVersion = 1
  _Parent = -> Elements001
FEATURE [Part::FeaturePython] Element033  # link proxy (typed FeaturePython)
  Detach = false
  InvalidShape = false
  LinkTransform = true
  LinkedObject = -> Link009 [Edge92]
  Radius = 2.3
  TreeRank = 745
  ValidateShape = true
  _LinkVersion = 1
  _Parent = -> Elements
FEATURE [Part::FeaturePython] _Element218  label="_Element006"  # link proxy (typed FeaturePython)
  Detach = false
  InvalidShape = false
  LinkTransform = true
  LinkedObject = -> Assembly [1.$Element033.]
  TreeRank = 746
  ValidateShape = true
  _LinkVersion = 1
  _Parent = -> Elements001
FEATURE [App::FeaturePython] Constraint105  label="Attachment018"  # WARN: FeaturePython — macro-defined, semantics opaque (R4)
  Cascade = false
  Disabled = false
  Group = -> [ElementLink212,ElementLink213]
  Multiply = true
  TreeRank = 748
  _ConstraintType = 45
  _LinkVersion = 1
  _Parent = -> Constraints001
FEATURE [App::FeaturePython] ElementLink212  label="_Element219"  # link proxy (typed FeaturePython)
  AutoCount = true
  Count = 3
  LinkTransform = true
  LinkedObject = -> _Element219
  PlacementList = 3 placements: [(-2.84217e-14,0,-3.55271e-15),(7.67386e-13,-20,-1.3145e-13),(1.39266e-12,-40,-1.27898e-13)]
  ShowElement = false
  TreeRank = 749
  _LinkVersion = 1
  _Parent = -> Constraint105
FEATURE [Part::FeaturePython] _Element219  # link proxy (typed FeaturePython)
  Detach = false
  InvalidShape = false
  LinkTransform = true
  LinkedObject = -> Link084 [0.Edge30]
  TreeRank = 750
  ValidateShape = true
  _LinkVersion = 1
  _Parent = -> Elements001
FEATURE [App::FeaturePython] ElementLink213  label="_Element007"  # link proxy (typed FeaturePython)
  LinkTransform = true
  LinkedObject = -> _Element221
  NoExpand = false
  TreeRank = 751
  _LinkVersion = 1
  _Parent = -> Constraint105
FEATURE [Part::FeaturePython] Element034  # link proxy (typed FeaturePython)
  Detach = false
  InvalidShape = false
  LinkTransform = true
  LinkedObject = -> Link010 [Edge100]
  TreeRank = 752
  ValidateShape = true
  _LinkVersion = 1
  _Parent = -> Elements
FEATURE [Part::FeaturePython] _Element220  # link proxy (typed FeaturePython)
  Detach = false
  InvalidShape = false
  LinkTransform = true
  LinkedObject = -> Assembly [1.$Element034.]
  TreeRank = 753
  ValidateShape = true
  _LinkVersion = 1
  _Parent = -> Elements001
FEATURE [Part::FeaturePython] Element035  # link proxy (typed FeaturePython)
  Detach = false
  InvalidShape = false
  LinkTransform = true
  LinkedObject = -> Link010 [Edge100]
  Radius = 2.3
  TreeRank = 754
  ValidateShape = true
  _LinkVersion = 1
  _Parent = -> Elements
FEATURE [Part::FeaturePython] _Element221  label="_Element007"  # link proxy (typed FeaturePython)
  Detach = false
  InvalidShape = false
  LinkTransform = true
  LinkedObject = -> Assembly [1.$Element035.]
  TreeRank = 755
  ValidateShape = true
  _LinkVersion = 1
  _Parent = -> Elements001
FEATURE [App::DocumentObjectGroupPython] Group014  label="fasteners Cstr"  # scripted group (container) (typed FeaturePython)
  ClaimAllChildren = true
  ExportMode = 0
  Group = -> [Constraint089,Constraint090,Constraint091,Constraint092,Constraint093,Constraint094,Constraint095,Constraint096,Constraint097,Constraint099,Constraint100,Constraint101,Constraint102,Constraint103,Constraint104,Constraint105]
  TreeRank = 756
  _GroupVersion = 1
  _Parent = -> Constraints001
FEATURE [Part::FeaturePython] _Element222  label="_Element008"  # link proxy (typed FeaturePython)
  Detach = false
  InvalidShape = false
  LinkTransform = true
  LinkedObject = -> Link028 [Edge98]
  TreeRank = 757
  ValidateShape = true
  _LinkVersion = 1
  _Parent = -> Elements001
FEATURE [Part::FeaturePython] _Element223  # link proxy (typed FeaturePython)
  Detach = false
  InvalidShape = false
  LinkTransform = true
  LinkedObject = -> Link085 [Edge3]
  TreeRank = 763
  ValidateShape = true
  _LinkVersion = 1
  _Parent = -> Elements001
FEATURE [Part::FeaturePython] Element036  # link proxy (typed FeaturePython)
  Detach = false
  InvalidShape = false
  LinkTransform = true
  LinkedObject = -> Link005 [Edge48]
  TreeRank = 765
  ValidateShape = true
  _LinkVersion = 1
  _Parent = -> Elements
FEATURE [Part::FeaturePython] _Element224  # link proxy (typed FeaturePython)
  Detach = false
  InvalidShape = false
  LinkTransform = true
  LinkedObject = -> Assembly [1.$Element036.]
  TreeRank = 766
  ValidateShape = true
  _LinkVersion = 1
  _Parent = -> Elements001
FEATURE [Part::FeaturePython] _Element225  label="_Element010"  # link proxy (typed FeaturePython)
  Detach = false
  InvalidShape = false
  LinkTransform = true
  LinkedObject = -> Link085 [0.Edge13]
  TreeRank = 767
  ValidateShape = true
  _LinkVersion = 1
  _Parent = -> Elements001
FEATURE [Part::FeaturePython] Element037  # link proxy (typed FeaturePython)
  Detach = false
  InvalidShape = false
  LinkTransform = true
  LinkedObject = -> Link005 [Edge48]
  Radius = 2
  TreeRank = 768
  ValidateShape = true
  _LinkVersion = 1
  _Parent = -> Elements
FEATURE [Part::FeaturePython] _Element226  label="_Element011"  # link proxy (typed FeaturePython)
  Detach = false
  InvalidShape = false
  LinkTransform = true
  LinkedObject = -> Assembly [1.$Element037.]
  TreeRank = 769
  ValidateShape = true
  _LinkVersion = 1
  _Parent = -> Elements001
FEATURE [App::FeaturePython] Constraint107  label="Attachment020"  # WARN: FeaturePython — macro-defined, semantics opaque (R4)
  Cascade = false
  Disabled = false
  Group = -> [ElementLink216,ElementLink217]
  Multiply = false
  TreeRank = 775
  _ConstraintType = 45
  _LinkVersion = 1
  _Parent = -> Constraints001
FEATURE [App::FeaturePython] ElementLink216  label="_Element010"  # link proxy (typed FeaturePython)
  LinkTransform = true
  LinkedObject = -> _Element225
  TreeRank = 776
  _LinkVersion = 1
  _Parent = -> Constraint107
FEATURE [App::FeaturePython] ElementLink217  label="_Element227"  # link proxy (typed FeaturePython)
  LinkTransform = true
  LinkedObject = -> _Element227
  TreeRank = 777
  _LinkVersion = 1
  _Parent = -> Constraint107
FEATURE [Part::FeaturePython] Element038  # link proxy (typed FeaturePython)
  Detach = false
  InvalidShape = false
  LinkTransform = true
  LinkedObject = -> Link005 [Edge47]
  TreeRank = 778
  ValidateShape = true
  _LinkVersion = 1
  _Parent = -> Elements
FEATURE [Part::FeaturePython] _Element227  # link proxy (typed FeaturePython)
  Detach = false
  InvalidShape = false
  LinkTransform = true
  LinkedObject = -> Assembly [1.$Element038.]
  TreeRank = 779
  ValidateShape = true
  _LinkVersion = 1
  _Parent = -> Elements001
FEATURE [Part::FeaturePython] Element039  # link proxy (typed FeaturePython)
  Detach = false
  InvalidShape = false
  LinkTransform = true
  LinkedObject = -> Link005 [Edge50]
  TreeRank = 788
  ValidateShape = true
  _LinkVersion = 1
  _Parent = -> Elements
FEATURE [Part::FeaturePython] _Element230  # link proxy (typed FeaturePython)
  Detach = false
  InvalidShape = false
  LinkTransform = true
  LinkedObject = -> Assembly [1.$Element039.]
  TreeRank = 789
  ValidateShape = true
  _LinkVersion = 1
  _Parent = -> Elements001
FEATURE [App::FeaturePython] Constraint110  label="Attachment023"  # WARN: FeaturePython — macro-defined, semantics opaque (R4)
  Cascade = false
  Disabled = false
  Group = -> [ElementLink222,ElementLink223]
  Multiply = false
  TreeRank = 790
  _ConstraintType = 45
  _LinkVersion = 1
  _Parent = -> Constraints001
FEATURE [App::FeaturePython] ElementLink222  label="_Element231"  # link proxy (typed FeaturePython)
  LinkTransform = true
  LinkedObject = -> _Element231
  TreeRank = 791
  _LinkVersion = 1
  _Parent = -> Constraint110
FEATURE [Part::FeaturePython] _Element231  # link proxy (typed FeaturePython)
  Detach = false
  InvalidShape = false
  LinkTransform = true
  LinkedObject = -> Link085 [2.Edge13]
  TreeRank = 792
  ValidateShape = true
  _LinkVersion = 1
  _Parent = -> Elements001
FEATURE [App::FeaturePython] ElementLink223  label="_Element232"  # link proxy (typed FeaturePython)
  LinkTransform = true
  LinkedObject = -> _Element232
  TreeRank = 793
  _LinkVersion = 1
  _Parent = -> Constraint110
FEATURE [Part::FeaturePython] Element040  # link proxy (typed FeaturePython)
  Detach = false
  InvalidShape = false
  LinkTransform = true
  LinkedObject = -> Link005 [Edge51]
  TreeRank = 794
  ValidateShape = true
  _LinkVersion = 1
  _Parent = -> Elements
FEATURE [Part::FeaturePython] _Element232  # link proxy (typed FeaturePython)
  Detach = false
  InvalidShape = false
  LinkTransform = true
  LinkedObject = -> Assembly [1.$Element040.]
  TreeRank = 795
  ValidateShape = true
  _LinkVersion = 1
  _Parent = -> Elements001
FEATURE [App::FeaturePython] Constraint111  label="Attachment024"  # WARN: FeaturePython — macro-defined, semantics opaque (R4)
  Cascade = false
  Disabled = false
  Group = -> [ElementLink224,ElementLink225]
  Multiply = false
  TreeRank = 796
  _ConstraintType = 45
  _LinkVersion = 1
  _Parent = -> Constraints001
FEATURE [App::FeaturePython] ElementLink224  label="_Element233"  # link proxy (typed FeaturePython)
  LinkTransform = true
  LinkedObject = -> _Element233
  TreeRank = 797
  _LinkVersion = 1
  _Parent = -> Constraint111
FEATURE [Part::FeaturePython] _Element233  # link proxy (typed FeaturePython)
  Detach = false
  InvalidShape = false
  LinkTransform = true
  LinkedObject = -> Link085 [1.Edge13]
  TreeRank = 798
  ValidateShape = true
  _LinkVersion = 1
  _Parent = -> Elements001
FEATURE [App::FeaturePython] ElementLink225  label="_Element234"  # link proxy (typed FeaturePython)
  LinkTransform = true
  LinkedObject = -> _Element234
  TreeRank = 799
  _LinkVersion = 1
  _Parent = -> Constraint111
FEATURE [Part::FeaturePython] Element041  # link proxy (typed FeaturePython)
  Detach = false
  InvalidShape = false
  LinkTransform = true
  LinkedObject = -> Link005 [Edge53]
  TreeRank = 800
  ValidateShape = true
  _LinkVersion = 1
  _Parent = -> Elements
FEATURE [Part::FeaturePython] _Element234  # link proxy (typed FeaturePython)
  Detach = false
  InvalidShape = false
  LinkTransform = true
  LinkedObject = -> Assembly [1.$Element041.]
  TreeRank = 801
  ValidateShape = true
  _LinkVersion = 1
  _Parent = -> Elements001

RESOLVED EXTERNAL PARTS (link-assembly join: the EXTERNAL_REF files above that resolve inside this repo's crawl, each included once):
---- part Tarmo5_parts/Fasteners/M3_Nut.FCStd = doc fcstd_00b6d367ec32 ----
FCSTD DOCUMENT  (FreeCAD 2022.1021R26244 +5249 (Git))
Label: M3_Nut
License: All rights reserved
LicenseURL: http://en.wikipedia.org/wiki/All_rights_reserved
objects: Part::FeaturePython×1
note: 1 computed .brp shape members not serialized (recipe doc carries the construction recipe); baked Part::Feature solids carry a one-line shape summary decoded from their .brp

FEATURE [Part::FeaturePython] Nut  label="M3-Nut"  # Fasteners workbench fastener (typed FeaturePython)
  TreeRank = 1
  diameter = 4
  invert = false
  leftHanded = false
  matchOuter = false
  offset = 0
  thread = false
  type = 22
---- part Tarmo5_parts/Fasteners/M4x16Screws.FCStd = doc fcstd_408e8ff70556 ----
FCSTD DOCUMENT  (FreeCAD 2022.1021R26244 +5249 (Git))
Label: M4x16Screws
License: All rights reserved
LicenseURL: http://en.wikipedia.org/wiki/All_rights_reserved
objects: Part::FeaturePython×1, App::Link×1
note: 1 computed .brp shape members not serialized (recipe doc carries the construction recipe); baked Part::Feature solids carry a one-line shape summary decoded from their .brp

FEATURE [Part::FeaturePython] Screw  label="M4x16-Screw"  # Fasteners workbench fastener (typed FeaturePython)
  TreeRank = 1
  diameter = 5
  invert = false
  leftHanded = false
  length = 5
  lengthCustom = 16
  matchOuter = false
  offset = 0
  thread = false
  type = 45
FEATURE [App::Link] Link  label="Link(M4x16-Screw)"
  AutoLinkLabel = true
  AutoPlacement = true
  LinkedObject = -> Screw
  SyncGroupVisibility = false
  TreeRank = 2
  _LinkVersion = 1
---- part Tarmo5_parts/Fasteners/M4x35Screws.FCStd = doc fcstd_08dbe7a0304b ----
FCSTD DOCUMENT  (FreeCAD 2022.1021R26244 +5249 (Git))
Label: M4x35Screws
License: All rights reserved
LicenseURL: http://en.wikipedia.org/wiki/All_rights_reserved
objects: Part::FeaturePython×1
note: 1 computed .brp shape members not serialized (recipe doc carries the construction recipe); baked Part::Feature solids carry a one-line shape summary decoded from their .brp

FEATURE [Part::FeaturePython] Screw  label="M4x35-Screw"  # Fasteners workbench fastener (typed FeaturePython)
  TreeRank = 1
  diameter = 5
  invert = false
  leftHanded = false
  length = 9
  lengthCustom = 35
  matchOuter = false
  offset = 0
  thread = false
  type = 45
---- part Tarmo5_parts/Fasteners/M4x45Screws.FCStd = doc fcstd_4b8e547a66a0 ----
FCSTD DOCUMENT  (FreeCAD 2022.1021R26244 +5249 (Git))
Label: M4x45Screws
License: All rights reserved
LicenseURL: http://en.wikipedia.org/wiki/All_rights_reserved
objects: Part::FeaturePython×1
note: 1 computed .brp shape members not serialized (recipe doc carries the construction recipe); baked Part::Feature solids carry a one-line shape summary decoded from their .brp

FEATURE [Part::FeaturePython] Screw  label="M4x50-Screw"  # Fasteners workbench fastener (typed FeaturePython)
  TreeRank = 1
  diameter = 5
  invert = false
  leftHanded = false
  length = 11
  lengthCustom = 50
  matchOuter = false
  offset = 0
  thread = false
  type = 45
---- part Tarmo5_parts/Fasteners/M4xScrews.FCStd = doc fcstd_01daf6a68c05 ----
FCSTD DOCUMENT  (FreeCAD 2022.1021R26244 +5249 (Git))
Label: M4xScrews
License: All rights reserved
LicenseURL: http://en.wikipedia.org/wiki/All_rights_reserved
objects: Part::FeaturePython×1
note: 1 computed .brp shape members not serialized (recipe doc carries the construction recipe); baked Part::Feature solids carry a one-line shape summary decoded from their .brp

FEATURE [Part::FeaturePython] Screw  label="M4x45-Screw"  # Fasteners workbench fastener (typed FeaturePython)
  Placement = pos=(0,0,0) rot=(0,1,0;3.14159rad)
  TreeRank = 1
  diameter = 5
  invert = false
  leftHanded = false
  length = 11
  lengthCustom = 45
  matchOuter = false
  offset = 0
  thread = false
  type = 45
